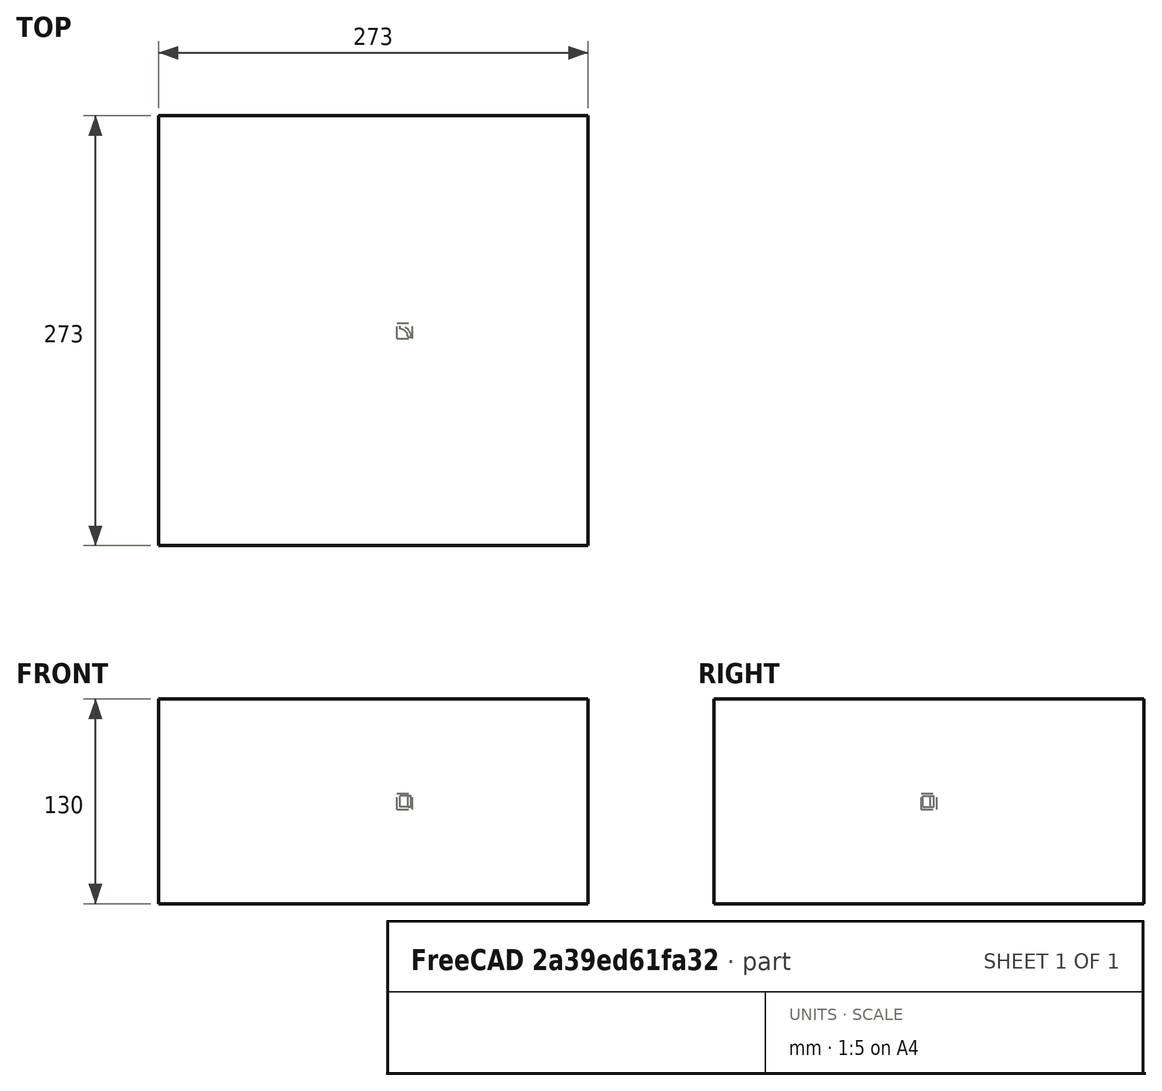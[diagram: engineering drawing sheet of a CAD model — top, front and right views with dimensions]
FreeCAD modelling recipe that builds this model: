
FCSTD DOCUMENT  (FreeCAD 0.20RUnknown)
Label: array-of-array-a
License: All rights reserved
LicenseURL: http://en.wikipedia.org/wiki/All_rights_reserved
objects: App::DocumentObjectGroupPython×1251, Part::FeaturePython×5, App::Part×4
note: 3 computed .brp shape members not serialized (recipe doc carries the construction recipe); baked Part::Feature solids carry a one-line shape summary decoded from their .brp

FEATURE [App::DocumentObjectGroupPython] HALFPI  # scripted group (container) (typed FeaturePython)
  name = HALFPI
  value = pi/2.
FEATURE [App::DocumentObjectGroupPython] PI  # scripted group (container) (typed FeaturePython)
  name = PI
  value = 1.*pi
FEATURE [App::DocumentObjectGroupPython] TWOPI  # scripted group (container) (typed FeaturePython)
  name = TWOPI
  value = 2.*pi
FEATURE [App::DocumentObjectGroupPython] Constants  # scripted group (container) (typed FeaturePython)
  Group = -> [HALFPI,PI,TWOPI]
FEATURE [App::DocumentObjectGroupPython] Variables  # scripted group (container) (typed FeaturePython)
FEATURE [App::DocumentObjectGroupPython] Quantities  # scripted group (container) (typed FeaturePython)
FEATURE [App::DocumentObjectGroupPython] Isotopes  # scripted group (container) (typed FeaturePython)
FEATURE [App::DocumentObjectGroupPython] Elements  # scripted group (container) (typed FeaturePython)
FEATURE [App::DocumentObjectGroupPython] Matrix  # scripted group (container) (typed FeaturePython)
FEATURE [App::DocumentObjectGroupPython] Surfaces  # scripted group (container) (typed FeaturePython)
FEATURE [App::DocumentObjectGroupPython] Opticals  # scripted group (container) (typed FeaturePython)
  Group = -> [Matrix,Surfaces]
FEATURE [App::DocumentObjectGroupPython] G4Isotopes  # scripted group (container) (typed FeaturePython)
FEATURE [App::DocumentObjectGroupPython] H_element  # scripted group (container) (typed FeaturePython)
  Z = 1
  atom_value = 1.008
  formula = H
  name = H_element
FEATURE [App::DocumentObjectGroupPython] He_element  # scripted group (container) (typed FeaturePython)
  Z = 2
  atom_value = 4.0026
  formula = He
  name = He_element
FEATURE [App::DocumentObjectGroupPython] Li_element  # scripted group (container) (typed FeaturePython)
  Z = 3
  atom_value = 6.94
  formula = Li
  name = Li_element
FEATURE [App::DocumentObjectGroupPython] Be_element  # scripted group (container) (typed FeaturePython)
  Z = 4
  atom_value = 9.01218
  formula = Be
  name = Be_element
FEATURE [App::DocumentObjectGroupPython] B_element  # scripted group (container) (typed FeaturePython)
  Z = 5
  atom_value = 10.81
  formula = B
  name = B_element
FEATURE [App::DocumentObjectGroupPython] C_element  # scripted group (container) (typed FeaturePython)
  Z = 6
  atom_value = 12.011
  formula = C
  name = C_element
FEATURE [App::DocumentObjectGroupPython] N_element  # scripted group (container) (typed FeaturePython)
  Z = 7
  atom_value = 14.007
  formula = N
  name = N_element
FEATURE [App::DocumentObjectGroupPython] O_element  # scripted group (container) (typed FeaturePython)
  Z = 8
  atom_value = 15.999
  formula = O
  name = O_element
FEATURE [App::DocumentObjectGroupPython] F_element  # scripted group (container) (typed FeaturePython)
  Z = 9
  atom_value = 18.9984
  formula = F
  name = F_element
FEATURE [App::DocumentObjectGroupPython] Ne_element  # scripted group (container) (typed FeaturePython)
  Z = 10
  atom_value = 20.1797
  formula = Ne
  name = Ne_element
FEATURE [App::DocumentObjectGroupPython] Na_element  # scripted group (container) (typed FeaturePython)
  Z = 11
  atom_value = 22.9898
  formula = Na
  name = Na_element
FEATURE [App::DocumentObjectGroupPython] Mg_element  # scripted group (container) (typed FeaturePython)
  Z = 12
  atom_value = 24.305
  formula = Mg
  name = Mg_element
FEATURE [App::DocumentObjectGroupPython] Al_element  # scripted group (container) (typed FeaturePython)
  Z = 13
  atom_value = 26.9815
  formula = Al
  name = Al_element
FEATURE [App::DocumentObjectGroupPython] Si_element  # scripted group (container) (typed FeaturePython)
  Z = 14
  atom_value = 28.085
  formula = Si
  name = Si_element
FEATURE [App::DocumentObjectGroupPython] P_element  # scripted group (container) (typed FeaturePython)
  Z = 15
  atom_value = 30.9738
  formula = P
  name = P_element
FEATURE [App::DocumentObjectGroupPython] S_element  # scripted group (container) (typed FeaturePython)
  Z = 16
  atom_value = 32.06
  formula = S
  name = S_element
FEATURE [App::DocumentObjectGroupPython] Cl_element  # scripted group (container) (typed FeaturePython)
  Z = 17
  atom_value = 35.45
  formula = Cl
  name = Cl_element
FEATURE [App::DocumentObjectGroupPython] Ar_element  # scripted group (container) (typed FeaturePython)
  Z = 18
  atom_value = 39.95
  formula = Ar
  name = Ar_element
FEATURE [App::DocumentObjectGroupPython] K_element  # scripted group (container) (typed FeaturePython)
  Z = 19
  atom_value = 39.0983
  formula = K
  name = K_element
FEATURE [App::DocumentObjectGroupPython] Ca_element  # scripted group (container) (typed FeaturePython)
  Z = 20
  atom_value = 40.078
  formula = Ca
  name = Ca_element
FEATURE [App::DocumentObjectGroupPython] Sc_element  # scripted group (container) (typed FeaturePython)
  Z = 21
  atom_value = 44.9559
  formula = Sc
  name = Sc_element
FEATURE [App::DocumentObjectGroupPython] Ti_element  # scripted group (container) (typed FeaturePython)
  Z = 22
  atom_value = 47.867
  formula = Ti
  name = Ti_element
FEATURE [App::DocumentObjectGroupPython] V_element  # scripted group (container) (typed FeaturePython)
  Z = 23
  atom_value = 50.9415
  formula = V
  name = V_element
FEATURE [App::DocumentObjectGroupPython] Cr_element  # scripted group (container) (typed FeaturePython)
  Z = 24
  atom_value = 51.9961
  formula = Cr
  name = Cr_element
FEATURE [App::DocumentObjectGroupPython] Mn_element  # scripted group (container) (typed FeaturePython)
  Z = 25
  atom_value = 54.938
  formula = Mn
  name = Mn_element
FEATURE [App::DocumentObjectGroupPython] Fe_element  # scripted group (container) (typed FeaturePython)
  Z = 26
  atom_value = 55.845
  formula = Fe
  name = Fe_element
FEATURE [App::DocumentObjectGroupPython] Co_element  # scripted group (container) (typed FeaturePython)
  Z = 27
  atom_value = 58.9332
  formula = Co
  name = Co_element
FEATURE [App::DocumentObjectGroupPython] Ni_element  # scripted group (container) (typed FeaturePython)
  Z = 28
  atom_value = 58.6934
  formula = Ni
  name = Ni_element
FEATURE [App::DocumentObjectGroupPython] Cu_element  # scripted group (container) (typed FeaturePython)
  Z = 29
  atom_value = 63.546
  formula = Cu
  name = Cu_element
FEATURE [App::DocumentObjectGroupPython] Zn_element  # scripted group (container) (typed FeaturePython)
  Z = 30
  atom_value = 65.38
  formula = Zn
  name = Zn_element
FEATURE [App::DocumentObjectGroupPython] Ga_element  # scripted group (container) (typed FeaturePython)
  Z = 31
  atom_value = 69.723
  formula = Ga
  name = Ga_element
FEATURE [App::DocumentObjectGroupPython] Ge_element  # scripted group (container) (typed FeaturePython)
  Z = 32
  atom_value = 72.63
  formula = Ge
  name = Ge_element
FEATURE [App::DocumentObjectGroupPython] As_element  # scripted group (container) (typed FeaturePython)
  Z = 33
  atom_value = 74.9216
  formula = As
  name = As_element
FEATURE [App::DocumentObjectGroupPython] Se_element  # scripted group (container) (typed FeaturePython)
  Z = 34
  atom_value = 78.971
  formula = Se
  name = Se_element
FEATURE [App::DocumentObjectGroupPython] Br_element  # scripted group (container) (typed FeaturePython)
  Z = 35
  atom_value = 79.904
  formula = Br
  name = Br_element
FEATURE [App::DocumentObjectGroupPython] Kr_element  # scripted group (container) (typed FeaturePython)
  Z = 36
  atom_value = 83.798
  formula = Kr
  name = Kr_element
FEATURE [App::DocumentObjectGroupPython] Rb_element  # scripted group (container) (typed FeaturePython)
  Z = 37
  atom_value = 85.4678
  formula = Rb
  name = Rb_element
FEATURE [App::DocumentObjectGroupPython] Sr_element  # scripted group (container) (typed FeaturePython)
  Z = 38
  atom_value = 87.62
  formula = Sr
  name = Sr_element
FEATURE [App::DocumentObjectGroupPython] Y_element  # scripted group (container) (typed FeaturePython)
  Z = 39
  atom_value = 88.9058
  formula = Y
  name = Y_element
FEATURE [App::DocumentObjectGroupPython] Zr_element  # scripted group (container) (typed FeaturePython)
  Z = 40
  atom_value = 91.224
  formula = Zr
  name = Zr_element
FEATURE [App::DocumentObjectGroupPython] Nb_element  # scripted group (container) (typed FeaturePython)
  Z = 41
  atom_value = 92.9064
  formula = Nb
  name = Nb_element
FEATURE [App::DocumentObjectGroupPython] Mo_element  # scripted group (container) (typed FeaturePython)
  Z = 42
  atom_value = 95.95
  formula = Mo
  name = Mo_element
FEATURE [App::DocumentObjectGroupPython] Tc_element  # scripted group (container) (typed FeaturePython)
  Z = 43
  atom_value = 97
  formula = Tc
  name = Tc_element
FEATURE [App::DocumentObjectGroupPython] Ru_element  # scripted group (container) (typed FeaturePython)
  Z = 44
  atom_value = 101.07
  formula = Ru
  name = Ru_element
FEATURE [App::DocumentObjectGroupPython] Rh_element  # scripted group (container) (typed FeaturePython)
  Z = 45
  atom_value = 102.905
  formula = Rh
  name = Rh_element
FEATURE [App::DocumentObjectGroupPython] Pd_element  # scripted group (container) (typed FeaturePython)
  Z = 46
  atom_value = 106.42
  formula = Pd
  name = Pd_element
FEATURE [App::DocumentObjectGroupPython] Ag_element  # scripted group (container) (typed FeaturePython)
  Z = 47
  atom_value = 107.868
  formula = Ag
  name = Ag_element
FEATURE [App::DocumentObjectGroupPython] Cd_element  # scripted group (container) (typed FeaturePython)
  Z = 48
  atom_value = 112.414
  formula = Cd
  name = Cd_element
FEATURE [App::DocumentObjectGroupPython] In_element  # scripted group (container) (typed FeaturePython)
  Z = 49
  atom_value = 114.818
  formula = In
  name = In_element
FEATURE [App::DocumentObjectGroupPython] Sn_element  # scripted group (container) (typed FeaturePython)
  Z = 50
  atom_value = 118.71
  formula = Sn
  name = Sn_element
FEATURE [App::DocumentObjectGroupPython] Sb_element  # scripted group (container) (typed FeaturePython)
  Z = 51
  atom_value = 121.76
  formula = Sb
  name = Sb_element
FEATURE [App::DocumentObjectGroupPython] Te_element  # scripted group (container) (typed FeaturePython)
  Z = 52
  atom_value = 127.6
  formula = Te
  name = Te_element
FEATURE [App::DocumentObjectGroupPython] I_element  # scripted group (container) (typed FeaturePython)
  Z = 53
  atom_value = 126.904
  formula = I
  name = I_element
FEATURE [App::DocumentObjectGroupPython] Xe_element  # scripted group (container) (typed FeaturePython)
  Z = 54
  atom_value = 131.293
  formula = Xe
  name = Xe_element
FEATURE [App::DocumentObjectGroupPython] Cs_element  # scripted group (container) (typed FeaturePython)
  Z = 55
  atom_value = 132.905
  formula = Cs
  name = Cs_element
FEATURE [App::DocumentObjectGroupPython] Ba_element  # scripted group (container) (typed FeaturePython)
  Z = 56
  atom_value = 137.327
  formula = Ba
  name = Ba_element
FEATURE [App::DocumentObjectGroupPython] La_element  # scripted group (container) (typed FeaturePython)
  Z = 57
  atom_value = 138.905
  formula = La
  name = La_element
FEATURE [App::DocumentObjectGroupPython] Ce_element  # scripted group (container) (typed FeaturePython)
  Z = 58
  atom_value = 140.116
  formula = Ce
  name = Ce_element
FEATURE [App::DocumentObjectGroupPython] Pr_element  # scripted group (container) (typed FeaturePython)
  Z = 59
  atom_value = 140.908
  formula = Pr
  name = Pr_element
FEATURE [App::DocumentObjectGroupPython] Nd_element  # scripted group (container) (typed FeaturePython)
  Z = 60
  atom_value = 144.242
  formula = Nd
  name = Nd_element
FEATURE [App::DocumentObjectGroupPython] Pm_element  # scripted group (container) (typed FeaturePython)
  Z = 61
  atom_value = 145
  formula = Pm
  name = Pm_element
FEATURE [App::DocumentObjectGroupPython] Sm_element  # scripted group (container) (typed FeaturePython)
  Z = 62
  atom_value = 150.36
  formula = Sm
  name = Sm_element
FEATURE [App::DocumentObjectGroupPython] Eu_element  # scripted group (container) (typed FeaturePython)
  Z = 63
  atom_value = 151.964
  formula = Eu
  name = Eu_element
FEATURE [App::DocumentObjectGroupPython] Gd_element  # scripted group (container) (typed FeaturePython)
  Z = 64
  atom_value = 157.25
  formula = Gd
  name = Gd_element
FEATURE [App::DocumentObjectGroupPython] Tb_element  # scripted group (container) (typed FeaturePython)
  Z = 65
  atom_value = 158.925
  formula = Tb
  name = Tb_element
FEATURE [App::DocumentObjectGroupPython] Dy_element  # scripted group (container) (typed FeaturePython)
  Z = 66
  atom_value = 162.5
  formula = Dy
  name = Dy_element
FEATURE [App::DocumentObjectGroupPython] Ho_element  # scripted group (container) (typed FeaturePython)
  Z = 67
  atom_value = 164.93
  formula = Ho
  name = Ho_element
FEATURE [App::DocumentObjectGroupPython] Er_element  # scripted group (container) (typed FeaturePython)
  Z = 68
  atom_value = 167.259
  formula = Er
  name = Er_element
FEATURE [App::DocumentObjectGroupPython] Tm_element  # scripted group (container) (typed FeaturePython)
  Z = 69
  atom_value = 168.934
  formula = Tm
  name = Tm_element
FEATURE [App::DocumentObjectGroupPython] Yb_element  # scripted group (container) (typed FeaturePython)
  Z = 70
  atom_value = 173.045
  formula = Yb
  name = Yb_element
FEATURE [App::DocumentObjectGroupPython] Lu_element  # scripted group (container) (typed FeaturePython)
  Z = 71
  atom_value = 174.967
  formula = Lu
  name = Lu_element
FEATURE [App::DocumentObjectGroupPython] Hf_element  # scripted group (container) (typed FeaturePython)
  Z = 72
  atom_value = 178.49
  formula = Hf
  name = Hf_element
FEATURE [App::DocumentObjectGroupPython] Ta_element  # scripted group (container) (typed FeaturePython)
  Z = 73
  atom_value = 180.948
  formula = Ta
  name = Ta_element
FEATURE [App::DocumentObjectGroupPython] W_element  # scripted group (container) (typed FeaturePython)
  Z = 74
  atom_value = 183.84
  formula = W
  name = W_element
FEATURE [App::DocumentObjectGroupPython] Re_element  # scripted group (container) (typed FeaturePython)
  Z = 75
  atom_value = 186.207
  formula = Re
  name = Re_element
FEATURE [App::DocumentObjectGroupPython] Os_element  # scripted group (container) (typed FeaturePython)
  Z = 76
  atom_value = 190.23
  formula = Os
  name = Os_element
FEATURE [App::DocumentObjectGroupPython] Ir_element  # scripted group (container) (typed FeaturePython)
  Z = 77
  atom_value = 192.217
  formula = Ir
  name = Ir_element
FEATURE [App::DocumentObjectGroupPython] Pt_element  # scripted group (container) (typed FeaturePython)
  Z = 78
  atom_value = 195.084
  formula = Pt
  name = Pt_element
FEATURE [App::DocumentObjectGroupPython] Au_element  # scripted group (container) (typed FeaturePython)
  Z = 79
  atom_value = 196.967
  formula = Au
  name = Au_element
FEATURE [App::DocumentObjectGroupPython] Hg_element  # scripted group (container) (typed FeaturePython)
  Z = 80
  atom_value = 200.592
  formula = Hg
  name = Hg_element
FEATURE [App::DocumentObjectGroupPython] Tl_element  # scripted group (container) (typed FeaturePython)
  Z = 81
  atom_value = 204.38
  formula = Tl
  name = Tl_element
FEATURE [App::DocumentObjectGroupPython] Pb_element  # scripted group (container) (typed FeaturePython)
  Z = 82
  atom_value = 207.2
  formula = Pb
  name = Pb_element
FEATURE [App::DocumentObjectGroupPython] Bi_element  # scripted group (container) (typed FeaturePython)
  Z = 83
  atom_value = 208.98
  formula = Bi
  name = Bi_element
FEATURE [App::DocumentObjectGroupPython] Po_element  # scripted group (container) (typed FeaturePython)
  Z = 84
  atom_value = 209
  formula = Po
  name = Po_element
FEATURE [App::DocumentObjectGroupPython] At_element  # scripted group (container) (typed FeaturePython)
  Z = 85
  atom_value = 210
  formula = At
  name = At_element
FEATURE [App::DocumentObjectGroupPython] Rn_element  # scripted group (container) (typed FeaturePython)
  Z = 86
  atom_value = 222
  formula = Rn
  name = Rn_element
FEATURE [App::DocumentObjectGroupPython] Fr_element  # scripted group (container) (typed FeaturePython)
  Z = 87
  atom_value = 223
  formula = Fr
  name = Fr_element
FEATURE [App::DocumentObjectGroupPython] Ra_element  # scripted group (container) (typed FeaturePython)
  Z = 88
  atom_value = 226
  formula = Ra
  name = Ra_element
FEATURE [App::DocumentObjectGroupPython] Ac_element  # scripted group (container) (typed FeaturePython)
  Z = 89
  atom_value = 227
  formula = Ac
  name = Ac_element
FEATURE [App::DocumentObjectGroupPython] Th_element  # scripted group (container) (typed FeaturePython)
  Z = 90
  atom_value = 232.038
  formula = Th
  name = Th_element
FEATURE [App::DocumentObjectGroupPython] Pa_element  # scripted group (container) (typed FeaturePython)
  Z = 91
  atom_value = 231.036
  formula = Pa
  name = Pa_element
FEATURE [App::DocumentObjectGroupPython] U_element  # scripted group (container) (typed FeaturePython)
  Z = 92
  atom_value = 238.029
  formula = U
  name = U_element
FEATURE [App::DocumentObjectGroupPython] Np_element  # scripted group (container) (typed FeaturePython)
  Z = 93
  atom_value = 237
  formula = Np
  name = Np_element
FEATURE [App::DocumentObjectGroupPython] Pu_element  # scripted group (container) (typed FeaturePython)
  Z = 94
  atom_value = 244
  formula = Pu
  name = Pu_element
FEATURE [App::DocumentObjectGroupPython] Am_element  # scripted group (container) (typed FeaturePython)
  Z = 95
  atom_value = 243
  formula = Am
  name = Am_element
FEATURE [App::DocumentObjectGroupPython] Cm_element  # scripted group (container) (typed FeaturePython)
  Z = 96
  atom_value = 247
  formula = Cm
  name = Cm_element
FEATURE [App::DocumentObjectGroupPython] Bk_element  # scripted group (container) (typed FeaturePython)
  Z = 97
  atom_value = 247
  formula = Bk
  name = Bk_element
FEATURE [App::DocumentObjectGroupPython] Cf_element  # scripted group (container) (typed FeaturePython)
  Z = 98
  atom_value = 251
  formula = Cf
  name = Cf_element
FEATURE [App::DocumentObjectGroupPython] G4Elements  # scripted group (container) (typed FeaturePython)
  Group = -> [H_element,He_element,Li_element,Be_element,B_element,C_element,N_element,O_element,F_element,Ne_element,Na_element,Mg_element,Al_element,Si_element,P_element,S_element,Cl_element,Ar_element,K_element,Ca_element,Sc_element,Ti_element,V_element,Cr_element,Mn_element,Fe_element,Co_element,Ni_element,Cu_element,Zn_element,Ga_element,Ge_element,As_element,Se_element,Br_element,Kr_element,Rb_element,+61 more]
FEATURE [App::DocumentObjectGroupPython] H_element001  label="H_element : 0.101"  # scripted group (container) (typed FeaturePython)
  n = 0.101327
FEATURE [App::DocumentObjectGroupPython] C_element001  label="C_element : 0.775"  # scripted group (container) (typed FeaturePython)
  n = 0.7755
FEATURE [App::DocumentObjectGroupPython] N_element001  label="N_element : 0.035"  # scripted group (container) (typed FeaturePython)
  n = 0.035057
FEATURE [App::DocumentObjectGroupPython] O_element001  label="O_element : 0.052"  # scripted group (container) (typed FeaturePython)
  n = 0.0523159
FEATURE [App::DocumentObjectGroupPython] F_element001  label="F_element : 0.017"  # scripted group (container) (typed FeaturePython)
  n = 0.017422
FEATURE [App::DocumentObjectGroupPython] Ca_element001  label="Ca_element : 0.018"  # scripted group (container) (typed FeaturePython)
  n = 0.018378
FEATURE [App::DocumentObjectGroupPython] G4_A_150_TISSUE  label="G4_A-150_TISSUE"  # scripted group (container) (typed FeaturePython)
  Dunit = g/cm3
  Dvalue = 1.127
  Group = -> [H_element001,C_element001,N_element001,O_element001,F_element001,Ca_element001]
  conduct = 2
  density = 1
  expand = 3
  formula = G4_A-150_TISSUE
  name = G4_A-150_TISSUE
  specific = 4
FEATURE [App::DocumentObjectGroupPython] C_element002  label="C_element : 3"  # scripted group (container) (typed FeaturePython)
  n = 3
  ref = C_element
FEATURE [App::DocumentObjectGroupPython] H_element002  label="H_element : 6"  # scripted group (container) (typed FeaturePython)
  n = 6
  ref = H_element
FEATURE [App::DocumentObjectGroupPython] O_element002  label="O_element : 1"  # scripted group (container) (typed FeaturePython)
  n = 1
  ref = O_element
FEATURE [App::DocumentObjectGroupPython] G4_ACETONE  # scripted group (container) (typed FeaturePython)
  Dunit = g/cm3
  Dvalue = 0.7899
  Group = -> [C_element002,H_element002,O_element002]
  conduct = 2
  density = 1
  expand = 3
  formula = G4_ACETONE
  name = G4_ACETONE
  specific = 4
FEATURE [App::DocumentObjectGroupPython] C_element003  label="C_element : 2"  # scripted group (container) (typed FeaturePython)
  n = 2
  ref = C_element
FEATURE [App::DocumentObjectGroupPython] H_element003  label="H_element : 2"  # scripted group (container) (typed FeaturePython)
  n = 2
  ref = H_element
FEATURE [App::DocumentObjectGroupPython] G4_ACETYLENE  # scripted group (container) (typed FeaturePython)
  Dunit = g/cm3
  Dvalue = 0.0010967
  Group = -> [C_element003,H_element003]
  conduct = 2
  density = 1
  expand = 3
  formula = G4_ACETYLENE
  name = G4_ACETYLENE
  specific = 4
FEATURE [App::DocumentObjectGroupPython] C_element004  label="C_element : 5"  # scripted group (container) (typed FeaturePython)
  n = 5
  ref = C_element
FEATURE [App::DocumentObjectGroupPython] H_element004  label="H_element : 5"  # scripted group (container) (typed FeaturePython)
  n = 5
  ref = H_element
FEATURE [App::DocumentObjectGroupPython] N_element002  label="N_element : 5"  # scripted group (container) (typed FeaturePython)
  n = 5
  ref = N_element
FEATURE [App::DocumentObjectGroupPython] G4_ADENINE  # scripted group (container) (typed FeaturePython)
  Dunit = g/cm3
  Dvalue = 1.6
  Group = -> [C_element004,H_element004,N_element002]
  conduct = 2
  density = 1
  expand = 3
  formula = G4_ADENINE
  name = G4_ADENINE
  specific = 4
FEATURE [App::DocumentObjectGroupPython] H_element005  label="H_element : 0.114"  # scripted group (container) (typed FeaturePython)
  n = 0.114
FEATURE [App::DocumentObjectGroupPython] C_element005  label="C_element : 0.598"  # scripted group (container) (typed FeaturePython)
  n = 0.598
FEATURE [App::DocumentObjectGroupPython] N_element003  label="N_element : 0.007"  # scripted group (container) (typed FeaturePython)
  n = 0.007
FEATURE [App::DocumentObjectGroupPython] O_element003  label="O_element : 0.278"  # scripted group (container) (typed FeaturePython)
  n = 0.278
FEATURE [App::DocumentObjectGroupPython] Na_element001  label="Na_element : 0.001"  # scripted group (container) (typed FeaturePython)
  n = 0.001
FEATURE [App::DocumentObjectGroupPython] S_element001  label="S_element : 0.001"  # scripted group (container) (typed FeaturePython)
  n = 0.001
FEATURE [App::DocumentObjectGroupPython] Cl_element001  label="Cl_element : 0.001"  # scripted group (container) (typed FeaturePython)
  n = 0.001
FEATURE [App::DocumentObjectGroupPython] G4_ADIPOSE_TISSUE_ICRP  # scripted group (container) (typed FeaturePython)
  Dunit = g/cm3
  Dvalue = 0.95
  Group = -> [H_element005,C_element005,N_element003,O_element003,Na_element001,S_element001,Cl_element001]
  conduct = 2
  density = 1
  expand = 3
  formula = G4_ADIPOSE_TISSUE_ICRP
  name = G4_ADIPOSE_TISSUE_ICRP
  specific = 4
FEATURE [App::DocumentObjectGroupPython] C_element006  label="C_element : 0.000"  # scripted group (container) (typed FeaturePython)
  n = 0.000124
FEATURE [App::DocumentObjectGroupPython] N_element004  label="N_element : 0.755"  # scripted group (container) (typed FeaturePython)
  n = 0.755268
FEATURE [App::DocumentObjectGroupPython] O_element004  label="O_element : 0.232"  # scripted group (container) (typed FeaturePython)
  n = 0.231781
FEATURE [App::DocumentObjectGroupPython] Ar_element001  label="Ar_element : 0.013"  # scripted group (container) (typed FeaturePython)
  n = 0.012827
FEATURE [App::DocumentObjectGroupPython] G4_AIR  # scripted group (container) (typed FeaturePython)
  Dunit = g/cm3
  Dvalue = 0.00120479
  Group = -> [C_element006,N_element004,O_element004,Ar_element001]
  conduct = 2
  density = 1
  expand = 3
  formula = G4_AIR
  name = G4_AIR
  specific = 4
FEATURE [App::DocumentObjectGroupPython] C_element007  label="C_element : 006"  # scripted group (container) (typed FeaturePython)
  n = 3
  ref = C_element
FEATURE [App::DocumentObjectGroupPython] H_element006  label="H_element : 7"  # scripted group (container) (typed FeaturePython)
  n = 7
  ref = H_element
FEATURE [App::DocumentObjectGroupPython] N_element005  label="N_element : 1"  # scripted group (container) (typed FeaturePython)
  n = 1
  ref = N_element
FEATURE [App::DocumentObjectGroupPython] O_element005  label="O_element : 2"  # scripted group (container) (typed FeaturePython)
  n = 2
  ref = O_element
FEATURE [App::DocumentObjectGroupPython] G4_ALANINE  # scripted group (container) (typed FeaturePython)
  Dunit = g/cm3
  Dvalue = 1.42
  Group = -> [C_element007,H_element006,N_element005,O_element005]
  conduct = 2
  density = 1
  expand = 3
  formula = G4_ALANINE
  name = G4_ALANINE
  specific = 4
FEATURE [App::DocumentObjectGroupPython] Al_element001  label="Al_element : 2"  # scripted group (container) (typed FeaturePython)
  n = 2
  ref = Al_element
FEATURE [App::DocumentObjectGroupPython] O_element006  label="O_element : 3"  # scripted group (container) (typed FeaturePython)
  n = 3
  ref = O_element
FEATURE [App::DocumentObjectGroupPython] G4_ALUMINUM_OXIDE  # scripted group (container) (typed FeaturePython)
  Dunit = g/cm3
  Dvalue = 3.97
  Group = -> [Al_element001,O_element006]
  conduct = 2
  density = 1
  expand = 3
  formula = G4_ALUMINUM_OXIDE
  name = G4_ALUMINUM_OXIDE
  specific = 4
FEATURE [App::DocumentObjectGroupPython] H_element007  label="H_element : 0.106"  # scripted group (container) (typed FeaturePython)
  n = 0.10593
FEATURE [App::DocumentObjectGroupPython] C_element008  label="C_element : 0.789"  # scripted group (container) (typed FeaturePython)
  n = 0.788974
FEATURE [App::DocumentObjectGroupPython] O_element007  label="O_element : 0.105"  # scripted group (container) (typed FeaturePython)
  n = 0.105096
FEATURE [App::DocumentObjectGroupPython] G4_AMBER  # scripted group (container) (typed FeaturePython)
  Dunit = g/cm3
  Dvalue = 1.1
  Group = -> [H_element007,C_element008,O_element007]
  conduct = 2
  density = 1
  expand = 3
  formula = G4_AMBER
  name = G4_AMBER
  specific = 4
FEATURE [App::DocumentObjectGroupPython] N_element006  label="N_element : 006"  # scripted group (container) (typed FeaturePython)
  n = 1
  ref = N_element
FEATURE [App::DocumentObjectGroupPython] H_element008  label="H_element : 3"  # scripted group (container) (typed FeaturePython)
  n = 3
  ref = H_element
FEATURE [App::DocumentObjectGroupPython] G4_AMMONIA  # scripted group (container) (typed FeaturePython)
  Dunit = g/cm3
  Dvalue = 0.000826019
  Group = -> [N_element006,H_element008]
  conduct = 2
  density = 1
  expand = 3
  formula = G4_AMMONIA
  name = G4_AMMONIA
  specific = 4
FEATURE [App::DocumentObjectGroupPython] C_element009  label="C_element : 6"  # scripted group (container) (typed FeaturePython)
  n = 6
  ref = C_element
FEATURE [App::DocumentObjectGroupPython] H_element009  label="H_element : 008"  # scripted group (container) (typed FeaturePython)
  n = 7
  ref = H_element
FEATURE [App::DocumentObjectGroupPython] N_element007  label="N_element : 007"  # scripted group (container) (typed FeaturePython)
  n = 1
  ref = N_element
FEATURE [App::DocumentObjectGroupPython] G4_ANILINE  # scripted group (container) (typed FeaturePython)
  Dunit = g/cm3
  Dvalue = 1.0235
  Group = -> [C_element009,H_element009,N_element007]
  conduct = 2
  density = 1
  expand = 3
  formula = G4_ANILINE
  name = G4_ANILINE
  specific = 4
FEATURE [App::DocumentObjectGroupPython] C_element010  label="C_element : 14"  # scripted group (container) (typed FeaturePython)
  n = 14
  ref = C_element
FEATURE [App::DocumentObjectGroupPython] H_element010  label="H_element : 10"  # scripted group (container) (typed FeaturePython)
  n = 10
  ref = H_element
FEATURE [App::DocumentObjectGroupPython] G4_ANTHRACENE  # scripted group (container) (typed FeaturePython)
  Dunit = g/cm3
  Dvalue = 1.283
  Group = -> [C_element010,H_element010]
  conduct = 2
  density = 1
  expand = 3
  formula = G4_ANTHRACENE
  name = G4_ANTHRACENE
  specific = 4
FEATURE [App::DocumentObjectGroupPython] H_element011  label="H_element : 0.065"  # scripted group (container) (typed FeaturePython)
  n = 0.0654709
FEATURE [App::DocumentObjectGroupPython] C_element011  label="C_element : 0.537"  # scripted group (container) (typed FeaturePython)
  n = 0.536944
FEATURE [App::DocumentObjectGroupPython] N_element008  label="N_element : 0.021"  # scripted group (container) (typed FeaturePython)
  n = 0.0215
FEATURE [App::DocumentObjectGroupPython] O_element008  label="O_element : 0.032"  # scripted group (container) (typed FeaturePython)
  n = 0.032085
FEATURE [App::DocumentObjectGroupPython] F_element002  label="F_element : 0.167"  # scripted group (container) (typed FeaturePython)
  n = 0.167411
FEATURE [App::DocumentObjectGroupPython] Ca_element002  label="Ca_element : 0.177"  # scripted group (container) (typed FeaturePython)
  n = 0.176589
FEATURE [App::DocumentObjectGroupPython] G4_B_100_BONE  label="G4_B-100_BONE"  # scripted group (container) (typed FeaturePython)
  Dunit = g/cm3
  Dvalue = 1.45
  Group = -> [H_element011,C_element011,N_element008,O_element008,F_element002,Ca_element002]
  conduct = 2
  density = 1
  expand = 3
  formula = G4_B-100_BONE
  name = G4_B-100_BONE
  specific = 4
FEATURE [App::DocumentObjectGroupPython] H_element012  label="H_element : 0.057"  # scripted group (container) (typed FeaturePython)
  n = 0.057441
FEATURE [App::DocumentObjectGroupPython] C_element012  label="C_element : 0.790"  # scripted group (container) (typed FeaturePython)
  n = 0.774591
FEATURE [App::DocumentObjectGroupPython] O_element009  label="O_element : 0.168"  # scripted group (container) (typed FeaturePython)
  n = 0.167968
FEATURE [App::DocumentObjectGroupPython] G4_BAKELITE  # scripted group (container) (typed FeaturePython)
  Dunit = g/cm3
  Dvalue = 1.25
  Group = -> [H_element012,C_element012,O_element009]
  conduct = 2
  density = 1
  expand = 3
  formula = G4_BAKELITE
  name = G4_BAKELITE
  specific = 4
FEATURE [App::DocumentObjectGroupPython] Ba_element001  label="Ba_element : 1"  # scripted group (container) (typed FeaturePython)
  n = 1
  ref = Ba_element
FEATURE [App::DocumentObjectGroupPython] F_element003  label="F_element : 2"  # scripted group (container) (typed FeaturePython)
  n = 2
  ref = F_element
FEATURE [App::DocumentObjectGroupPython] G4_BARIUM_FLUORIDE  # scripted group (container) (typed FeaturePython)
  Dunit = g/cm3
  Dvalue = 4.89
  Group = -> [Ba_element001,F_element003]
  conduct = 2
  density = 1
  expand = 3
  formula = G4_BARIUM_FLUORIDE
  name = G4_BARIUM_FLUORIDE
  specific = 4
FEATURE [App::DocumentObjectGroupPython] Ba_element002  label="Ba_element : 002"  # scripted group (container) (typed FeaturePython)
  n = 1
  ref = Ba_element
FEATURE [App::DocumentObjectGroupPython] S_element002  label="S_element : 1"  # scripted group (container) (typed FeaturePython)
  n = 1
  ref = S_element
FEATURE [App::DocumentObjectGroupPython] O_element010  label="O_element : 4"  # scripted group (container) (typed FeaturePython)
  n = 4
  ref = O_element
FEATURE [App::DocumentObjectGroupPython] G4_BARIUM_SULFATE  # scripted group (container) (typed FeaturePython)
  Dunit = g/cm3
  Dvalue = 4.5
  Group = -> [Ba_element002,S_element002,O_element010]
  conduct = 2
  density = 1
  expand = 3
  formula = G4_BARIUM_SULFATE
  name = G4_BARIUM_SULFATE
  specific = 4
FEATURE [App::DocumentObjectGroupPython] C_element013  label="C_element : 007"  # scripted group (container) (typed FeaturePython)
  n = 6
  ref = C_element
FEATURE [App::DocumentObjectGroupPython] H_element013  label="H_element : 009"  # scripted group (container) (typed FeaturePython)
  n = 6
  ref = H_element
FEATURE [App::DocumentObjectGroupPython] G4_BENZENE  # scripted group (container) (typed FeaturePython)
  Dunit = g/cm3
  Dvalue = 0.87865
  Group = -> [C_element013,H_element013]
  conduct = 2
  density = 1
  expand = 3
  formula = G4_BENZENE
  name = G4_BENZENE
  specific = 4
FEATURE [App::DocumentObjectGroupPython] Be_element001  label="Be_element : 1"  # scripted group (container) (typed FeaturePython)
  n = 1
  ref = Be_element
FEATURE [App::DocumentObjectGroupPython] O_element011  label="O_element : 005"  # scripted group (container) (typed FeaturePython)
  n = 1
  ref = O_element
FEATURE [App::DocumentObjectGroupPython] G4_BERYLLIUM_OXIDE  # scripted group (container) (typed FeaturePython)
  Dunit = g/cm3
  Dvalue = 3.01
  Group = -> [Be_element001,O_element011]
  conduct = 2
  density = 1
  expand = 3
  formula = G4_BERYLLIUM_OXIDE
  name = G4_BERYLLIUM_OXIDE
  specific = 4
FEATURE [App::DocumentObjectGroupPython] Bi_element001  label="Bi_element : 4"  # scripted group (container) (typed FeaturePython)
  n = 4
  ref = Bi_element
FEATURE [App::DocumentObjectGroupPython] Ge_element001  label="Ge_element : 3"  # scripted group (container) (typed FeaturePython)
  n = 3
  ref = Ge_element
FEATURE [App::DocumentObjectGroupPython] O_element012  label="O_element : 12"  # scripted group (container) (typed FeaturePython)
  n = 12
  ref = O_element
FEATURE [App::DocumentObjectGroupPython] G4_BGO  # scripted group (container) (typed FeaturePython)
  Dunit = g/cm3
  Dvalue = 7.13
  Group = -> [Bi_element001,Ge_element001,O_element012]
  conduct = 2
  density = 1
  expand = 3
  formula = G4_BGO
  name = G4_BGO
  specific = 4
FEATURE [App::DocumentObjectGroupPython] H_element014  label="H_element : 0.102"  # scripted group (container) (typed FeaturePython)
  n = 0.102
FEATURE [App::DocumentObjectGroupPython] C_element014  label="C_element : 0.110"  # scripted group (container) (typed FeaturePython)
  n = 0.11
FEATURE [App::DocumentObjectGroupPython] N_element009  label="N_element : 0.033"  # scripted group (container) (typed FeaturePython)
  n = 0.033
FEATURE [App::DocumentObjectGroupPython] O_element013  label="O_element : 0.745"  # scripted group (container) (typed FeaturePython)
  n = 0.745
FEATURE [App::DocumentObjectGroupPython] Na_element002  label="Na_element : 0.002"  # scripted group (container) (typed FeaturePython)
  n = 0.001
FEATURE [App::DocumentObjectGroupPython] P_element001  label="P_element : 0.001"  # scripted group (container) (typed FeaturePython)
  n = 0.001
FEATURE [App::DocumentObjectGroupPython] S_element003  label="S_element : 0.002"  # scripted group (container) (typed FeaturePython)
  n = 0.002
FEATURE [App::DocumentObjectGroupPython] Cl_element002  label="Cl_element : 0.003"  # scripted group (container) (typed FeaturePython)
  n = 0.003
FEATURE [App::DocumentObjectGroupPython] K_element001  label="K_element : 0.002"  # scripted group (container) (typed FeaturePython)
  n = 0.002
FEATURE [App::DocumentObjectGroupPython] Fe_element001  label="Fe_element : 0.001"  # scripted group (container) (typed FeaturePython)
  n = 0.001
FEATURE [App::DocumentObjectGroupPython] G4_BLOOD_ICRP  # scripted group (container) (typed FeaturePython)
  Dunit = g/cm3
  Dvalue = 1.06
  Group = -> [H_element014,C_element014,N_element009,O_element013,Na_element002,P_element001,S_element003,Cl_element002,K_element001,Fe_element001]
  conduct = 2
  density = 1
  expand = 3
  formula = G4_BLOOD_ICRP
  name = G4_BLOOD_ICRP
  specific = 4
FEATURE [App::DocumentObjectGroupPython] H_element015  label="H_element : 0.064"  # scripted group (container) (typed FeaturePython)
  n = 0.064
FEATURE [App::DocumentObjectGroupPython] C_element015  label="C_element : 0.278"  # scripted group (container) (typed FeaturePython)
  n = 0.278
FEATURE [App::DocumentObjectGroupPython] N_element010  label="N_element : 0.027"  # scripted group (container) (typed FeaturePython)
  n = 0.027
FEATURE [App::DocumentObjectGroupPython] O_element014  label="O_element : 0.410"  # scripted group (container) (typed FeaturePython)
  n = 0.41
FEATURE [App::DocumentObjectGroupPython] Mg_element001  label="Mg_element : 0.002"  # scripted group (container) (typed FeaturePython)
  n = 0.002
FEATURE [App::DocumentObjectGroupPython] P_element002  label="P_element : 0.070"  # scripted group (container) (typed FeaturePython)
  n = 0.07
FEATURE [App::DocumentObjectGroupPython] S_element004  label="S_element : 0.003"  # scripted group (container) (typed FeaturePython)
  n = 0.002
FEATURE [App::DocumentObjectGroupPython] Ca_element003  label="Ca_element : 0.147"  # scripted group (container) (typed FeaturePython)
  n = 0.147
FEATURE [App::DocumentObjectGroupPython] G4_BONE_COMPACT_ICRU  # scripted group (container) (typed FeaturePython)
  Dunit = g/cm3
  Dvalue = 1.85
  Group = -> [H_element015,C_element015,N_element010,O_element014,Mg_element001,P_element002,S_element004,Ca_element003]
  conduct = 2
  density = 1
  expand = 3
  formula = G4_BONE_COMPACT_ICRU
  name = G4_BONE_COMPACT_ICRU
  specific = 4
FEATURE [App::DocumentObjectGroupPython] H_element016  label="H_element : 0.034"  # scripted group (container) (typed FeaturePython)
  n = 0.034
FEATURE [App::DocumentObjectGroupPython] C_element016  label="C_element : 0.155"  # scripted group (container) (typed FeaturePython)
  n = 0.155
FEATURE [App::DocumentObjectGroupPython] N_element011  label="N_element : 0.042"  # scripted group (container) (typed FeaturePython)
  n = 0.042
FEATURE [App::DocumentObjectGroupPython] O_element015  label="O_element : 0.435"  # scripted group (container) (typed FeaturePython)
  n = 0.435
FEATURE [App::DocumentObjectGroupPython] Na_element003  label="Na_element : 0.003"  # scripted group (container) (typed FeaturePython)
  n = 0.001
FEATURE [App::DocumentObjectGroupPython] Mg_element002  label="Mg_element : 0.003"  # scripted group (container) (typed FeaturePython)
  n = 0.002
FEATURE [App::DocumentObjectGroupPython] P_element003  label="P_element : 0.103"  # scripted group (container) (typed FeaturePython)
  n = 0.103
FEATURE [App::DocumentObjectGroupPython] S_element005  label="S_element : 0.004"  # scripted group (container) (typed FeaturePython)
  n = 0.003
FEATURE [App::DocumentObjectGroupPython] Ca_element004  label="Ca_element : 0.225"  # scripted group (container) (typed FeaturePython)
  n = 0.225
FEATURE [App::DocumentObjectGroupPython] G4_BONE_CORTICAL_ICRP  # scripted group (container) (typed FeaturePython)
  Dunit = g/cm3
  Dvalue = 1.92
  Group = -> [H_element016,C_element016,N_element011,O_element015,Na_element003,Mg_element002,P_element003,S_element005,Ca_element004]
  conduct = 2
  density = 1
  expand = 3
  formula = G4_BONE_CORTICAL_ICRP
  name = G4_BONE_CORTICAL_ICRP
  specific = 4
FEATURE [App::DocumentObjectGroupPython] B_element001  label="B_element : 4"  # scripted group (container) (typed FeaturePython)
  n = 4
  ref = B_element
FEATURE [App::DocumentObjectGroupPython] C_element017  label="C_element : 1"  # scripted group (container) (typed FeaturePython)
  n = 1
  ref = C_element
FEATURE [App::DocumentObjectGroupPython] G4_BORON_CARBIDE  # scripted group (container) (typed FeaturePython)
  Dunit = g/cm3
  Dvalue = 2.52
  Group = -> [B_element001,C_element017]
  conduct = 2
  density = 1
  expand = 3
  formula = G4_BORON_CARBIDE
  name = G4_BORON_CARBIDE
  specific = 4
FEATURE [App::DocumentObjectGroupPython] B_element002  label="B_element : 2"  # scripted group (container) (typed FeaturePython)
  n = 2
  ref = B_element
FEATURE [App::DocumentObjectGroupPython] O_element016  label="O_element : 006"  # scripted group (container) (typed FeaturePython)
  n = 3
  ref = O_element
FEATURE [App::DocumentObjectGroupPython] G4_BORON_OXIDE  # scripted group (container) (typed FeaturePython)
  Dunit = g/cm3
  Dvalue = 1.812
  Group = -> [B_element002,O_element016]
  conduct = 2
  density = 1
  expand = 3
  formula = G4_BORON_OXIDE
  name = G4_BORON_OXIDE
  specific = 4
FEATURE [App::DocumentObjectGroupPython] H_element017  label="H_element : 0.107"  # scripted group (container) (typed FeaturePython)
  n = 0.107
FEATURE [App::DocumentObjectGroupPython] C_element018  label="C_element : 0.145"  # scripted group (container) (typed FeaturePython)
  n = 0.145
FEATURE [App::DocumentObjectGroupPython] N_element012  label="N_element : 0.022"  # scripted group (container) (typed FeaturePython)
  n = 0.022
FEATURE [App::DocumentObjectGroupPython] O_element017  label="O_element : 0.712"  # scripted group (container) (typed FeaturePython)
  n = 0.712
FEATURE [App::DocumentObjectGroupPython] Na_element004  label="Na_element : 0.004"  # scripted group (container) (typed FeaturePython)
  n = 0.002
FEATURE [App::DocumentObjectGroupPython] P_element004  label="P_element : 0.004"  # scripted group (container) (typed FeaturePython)
  n = 0.004
FEATURE [App::DocumentObjectGroupPython] S_element006  label="S_element : 0.005"  # scripted group (container) (typed FeaturePython)
  n = 0.002
FEATURE [App::DocumentObjectGroupPython] Cl_element003  label="Cl_element : 0.004"  # scripted group (container) (typed FeaturePython)
  n = 0.003
FEATURE [App::DocumentObjectGroupPython] K_element002  label="K_element : 0.003"  # scripted group (container) (typed FeaturePython)
  n = 0.003
FEATURE [App::DocumentObjectGroupPython] G4_BRAIN_ICRP  # scripted group (container) (typed FeaturePython)
  Dunit = g/cm3
  Dvalue = 1.04
  Group = -> [H_element017,C_element018,N_element012,O_element017,Na_element004,P_element004,S_element006,Cl_element003,K_element002]
  conduct = 2
  density = 1
  expand = 3
  formula = G4_BRAIN_ICRP
  name = G4_BRAIN_ICRP
  specific = 4
FEATURE [App::DocumentObjectGroupPython] C_element019  label="C_element : 4"  # scripted group (container) (typed FeaturePython)
  n = 4
  ref = C_element
FEATURE [App::DocumentObjectGroupPython] H_element018  label="H_element : 010"  # scripted group (container) (typed FeaturePython)
  n = 10
  ref = H_element
FEATURE [App::DocumentObjectGroupPython] G4_BUTANE  # scripted group (container) (typed FeaturePython)
  Dunit = g/cm3
  Dvalue = 0.00249343
  Group = -> [C_element019,H_element018]
  conduct = 2
  density = 1
  expand = 3
  formula = G4_BUTANE
  name = G4_BUTANE
  specific = 4
FEATURE [App::DocumentObjectGroupPython] C_element020  label="C_element : 008"  # scripted group (container) (typed FeaturePython)
  n = 4
  ref = C_element
FEATURE [App::DocumentObjectGroupPython] H_element019  label="H_element : 011"  # scripted group (container) (typed FeaturePython)
  n = 10
  ref = H_element
FEATURE [App::DocumentObjectGroupPython] O_element018  label="O_element : 007"  # scripted group (container) (typed FeaturePython)
  n = 1
  ref = O_element
FEATURE [App::DocumentObjectGroupPython] G4_N_BUTYL_ALCOHOL  label="G4_N-BUTYL_ALCOHOL"  # scripted group (container) (typed FeaturePython)
  Dunit = g/cm3
  Dvalue = 0.8098
  Group = -> [C_element020,H_element019,O_element018]
  conduct = 2
  density = 1
  expand = 3
  formula = G4_N-BUTYL_ALCOHOL
  name = G4_N-BUTYL_ALCOHOL
  specific = 4
FEATURE [App::DocumentObjectGroupPython] H_element020  label="H_element : 0.025"  # scripted group (container) (typed FeaturePython)
  n = 0.02468
FEATURE [App::DocumentObjectGroupPython] C_element021  label="C_element : 0.502"  # scripted group (container) (typed FeaturePython)
  n = 0.501611
FEATURE [App::DocumentObjectGroupPython] O_element019  label="O_element : 0.005"  # scripted group (container) (typed FeaturePython)
  n = 0.004527
FEATURE [App::DocumentObjectGroupPython] F_element004  label="F_element : 0.465"  # scripted group (container) (typed FeaturePython)
  n = 0.465209
FEATURE [App::DocumentObjectGroupPython] Si_element001  label="Si_element : 0.004"  # scripted group (container) (typed FeaturePython)
  n = 0.003973
FEATURE [App::DocumentObjectGroupPython] G4_C_552  label="G4_C-552"  # scripted group (container) (typed FeaturePython)
  Dunit = g/cm3
  Dvalue = 1.76
  Group = -> [H_element020,C_element021,O_element019,F_element004,Si_element001]
  conduct = 2
  density = 1
  expand = 3
  formula = G4_C-552
  name = G4_C-552
  specific = 4
FEATURE [App::DocumentObjectGroupPython] Cd_element001  label="Cd_element : 1"  # scripted group (container) (typed FeaturePython)
  n = 1
  ref = Cd_element
FEATURE [App::DocumentObjectGroupPython] Te_element001  label="Te_element : 1"  # scripted group (container) (typed FeaturePython)
  n = 1
  ref = Te_element
FEATURE [App::DocumentObjectGroupPython] G4_CADMIUM_TELLURIDE  # scripted group (container) (typed FeaturePython)
  Dunit = g/cm3
  Dvalue = 6.2
  Group = -> [Cd_element001,Te_element001]
  conduct = 2
  density = 1
  expand = 3
  formula = G4_CADMIUM_TELLURIDE
  name = G4_CADMIUM_TELLURIDE
  specific = 4
FEATURE [App::DocumentObjectGroupPython] Cd_element002  label="Cd_element : 002"  # scripted group (container) (typed FeaturePython)
  n = 1
  ref = Cd_element
FEATURE [App::DocumentObjectGroupPython] W_element001  label="W_element : 1"  # scripted group (container) (typed FeaturePython)
  n = 1
  ref = W_element
FEATURE [App::DocumentObjectGroupPython] O_element020  label="O_element : 008"  # scripted group (container) (typed FeaturePython)
  n = 4
  ref = O_element
FEATURE [App::DocumentObjectGroupPython] G4_CADMIUM_TUNGSTATE  # scripted group (container) (typed FeaturePython)
  Dunit = g/cm3
  Dvalue = 7.9
  Group = -> [Cd_element002,W_element001,O_element020]
  conduct = 2
  density = 1
  expand = 3
  formula = G4_CADMIUM_TUNGSTATE
  name = G4_CADMIUM_TUNGSTATE
  specific = 4
FEATURE [App::DocumentObjectGroupPython] Ca_element005  label="Ca_element : 1"  # scripted group (container) (typed FeaturePython)
  n = 1
  ref = Ca_element
FEATURE [App::DocumentObjectGroupPython] C_element022  label="C_element : 009"  # scripted group (container) (typed FeaturePython)
  n = 1
  ref = C_element
FEATURE [App::DocumentObjectGroupPython] O_element021  label="O_element : 009"  # scripted group (container) (typed FeaturePython)
  n = 3
  ref = O_element
FEATURE [App::DocumentObjectGroupPython] G4_CALCIUM_CARBONATE  # scripted group (container) (typed FeaturePython)
  Dunit = g/cm3
  Dvalue = 2.8
  Group = -> [Ca_element005,C_element022,O_element021]
  conduct = 2
  density = 1
  expand = 3
  formula = G4_CALCIUM_CARBONATE
  name = G4_CALCIUM_CARBONATE
  specific = 4
FEATURE [App::DocumentObjectGroupPython] Ca_element006  label="Ca_element : 002"  # scripted group (container) (typed FeaturePython)
  n = 1
  ref = Ca_element
FEATURE [App::DocumentObjectGroupPython] F_element005  label="F_element : 003"  # scripted group (container) (typed FeaturePython)
  n = 2
  ref = F_element
FEATURE [App::DocumentObjectGroupPython] G4_CALCIUM_FLUORIDE  # scripted group (container) (typed FeaturePython)
  Dunit = g/cm3
  Dvalue = 3.18
  Group = -> [Ca_element006,F_element005]
  conduct = 2
  density = 1
  expand = 3
  formula = G4_CALCIUM_FLUORIDE
  name = G4_CALCIUM_FLUORIDE
  specific = 4
FEATURE [App::DocumentObjectGroupPython] Ca_element007  label="Ca_element : 003"  # scripted group (container) (typed FeaturePython)
  n = 1
  ref = Ca_element
FEATURE [App::DocumentObjectGroupPython] O_element022  label="O_element : 010"  # scripted group (container) (typed FeaturePython)
  n = 1
  ref = O_element
FEATURE [App::DocumentObjectGroupPython] G4_CALCIUM_OXIDE  # scripted group (container) (typed FeaturePython)
  Dunit = g/cm3
  Dvalue = 3.3
  Group = -> [Ca_element007,O_element022]
  conduct = 2
  density = 1
  expand = 3
  formula = G4_CALCIUM_OXIDE
  name = G4_CALCIUM_OXIDE
  specific = 4
FEATURE [App::DocumentObjectGroupPython] Ca_element008  label="Ca_element : 004"  # scripted group (container) (typed FeaturePython)
  n = 1
  ref = Ca_element
FEATURE [App::DocumentObjectGroupPython] S_element007  label="S_element : 002"  # scripted group (container) (typed FeaturePython)
  n = 1
  ref = S_element
FEATURE [App::DocumentObjectGroupPython] O_element023  label="O_element : 011"  # scripted group (container) (typed FeaturePython)
  n = 4
  ref = O_element
FEATURE [App::DocumentObjectGroupPython] G4_CALCIUM_SULFATE  # scripted group (container) (typed FeaturePython)
  Dunit = g/cm3
  Dvalue = 2.96
  Group = -> [Ca_element008,S_element007,O_element023]
  conduct = 2
  density = 1
  expand = 3
  formula = G4_CALCIUM_SULFATE
  name = G4_CALCIUM_SULFATE
  specific = 4
FEATURE [App::DocumentObjectGroupPython] Ca_element009  label="Ca_element : 005"  # scripted group (container) (typed FeaturePython)
  n = 1
  ref = Ca_element
FEATURE [App::DocumentObjectGroupPython] W_element002  label="W_element : 002"  # scripted group (container) (typed FeaturePython)
  n = 1
  ref = W_element
FEATURE [App::DocumentObjectGroupPython] O_element024  label="O_element : 012"  # scripted group (container) (typed FeaturePython)
  n = 4
  ref = O_element
FEATURE [App::DocumentObjectGroupPython] G4_CALCIUM_TUNGSTATE  # scripted group (container) (typed FeaturePython)
  Dunit = g/cm3
  Dvalue = 6.062
  Group = -> [Ca_element009,W_element002,O_element024]
  conduct = 2
  density = 1
  expand = 3
  formula = G4_CALCIUM_TUNGSTATE
  name = G4_CALCIUM_TUNGSTATE
  specific = 4
FEATURE [App::DocumentObjectGroupPython] C_element023  label="C_element : 010"  # scripted group (container) (typed FeaturePython)
  n = 1
  ref = C_element
FEATURE [App::DocumentObjectGroupPython] O_element025  label="O_element : 013"  # scripted group (container) (typed FeaturePython)
  n = 2
  ref = O_element
FEATURE [App::DocumentObjectGroupPython] G4_CARBON_DIOXIDE  # scripted group (container) (typed FeaturePython)
  Dunit = g/cm3
  Dvalue = 0.00184212
  Group = -> [C_element023,O_element025]
  conduct = 2
  density = 1
  expand = 3
  formula = G4_CARBON_DIOXIDE
  name = G4_CARBON_DIOXIDE
  specific = 4
FEATURE [App::DocumentObjectGroupPython] C_element024  label="C_element : 011"  # scripted group (container) (typed FeaturePython)
  n = 1
  ref = C_element
FEATURE [App::DocumentObjectGroupPython] Cl_element004  label="Cl_element : 4"  # scripted group (container) (typed FeaturePython)
  n = 4
  ref = Cl_element
FEATURE [App::DocumentObjectGroupPython] G4_CARBON_TETRACHLORIDE  # scripted group (container) (typed FeaturePython)
  Dunit = g/cm3
  Dvalue = 1.594
  Group = -> [C_element024,Cl_element004]
  conduct = 2
  density = 1
  expand = 3
  formula = G4_CARBON_TETRACHLORIDE
  name = G4_CARBON_TETRACHLORIDE
  specific = 4
FEATURE [App::DocumentObjectGroupPython] C_element025  label="C_element : 012"  # scripted group (container) (typed FeaturePython)
  n = 6
  ref = C_element
FEATURE [App::DocumentObjectGroupPython] H_element021  label="H_element : 012"  # scripted group (container) (typed FeaturePython)
  n = 10
  ref = H_element
FEATURE [App::DocumentObjectGroupPython] O_element026  label="O_element : 5"  # scripted group (container) (typed FeaturePython)
  n = 5
  ref = O_element
FEATURE [App::DocumentObjectGroupPython] G4_CELLULOSE_CELLOPHANE  # scripted group (container) (typed FeaturePython)
  Dunit = g/cm3
  Dvalue = 1.42
  Group = -> [C_element025,H_element021,O_element026]
  conduct = 2
  density = 1
  expand = 3
  formula = G4_CELLULOSE_CELLOPHANE
  name = G4_CELLULOSE_CELLOPHANE
  specific = 4
FEATURE [App::DocumentObjectGroupPython] H_element022  label="H_element : 0.067"  # scripted group (container) (typed FeaturePython)
  n = 0.067125
FEATURE [App::DocumentObjectGroupPython] C_element026  label="C_element : 0.545"  # scripted group (container) (typed FeaturePython)
  n = 0.545403
FEATURE [App::DocumentObjectGroupPython] O_element027  label="O_element : 0.387"  # scripted group (container) (typed FeaturePython)
  n = 0.387472
FEATURE [App::DocumentObjectGroupPython] G4_CELLULOSE_BUTYRATE  # scripted group (container) (typed FeaturePython)
  Dunit = g/cm3
  Dvalue = 1.2
  Group = -> [H_element022,C_element026,O_element027]
  conduct = 2
  density = 1
  expand = 3
  formula = G4_CELLULOSE_BUTYRATE
  name = G4_CELLULOSE_BUTYRATE
  specific = 4
FEATURE [App::DocumentObjectGroupPython] H_element023  label="H_element : 0.029"  # scripted group (container) (typed FeaturePython)
  n = 0.029216
FEATURE [App::DocumentObjectGroupPython] C_element027  label="C_element : 0.271"  # scripted group (container) (typed FeaturePython)
  n = 0.271296
FEATURE [App::DocumentObjectGroupPython] N_element013  label="N_element : 0.121"  # scripted group (container) (typed FeaturePython)
  n = 0.121276
FEATURE [App::DocumentObjectGroupPython] O_element028  label="O_element : 0.578"  # scripted group (container) (typed FeaturePython)
  n = 0.578212
FEATURE [App::DocumentObjectGroupPython] G4_CELLULOSE_NITRATE  # scripted group (container) (typed FeaturePython)
  Dunit = g/cm3
  Dvalue = 1.49
  Group = -> [H_element023,C_element027,N_element013,O_element028]
  conduct = 2
  density = 1
  expand = 3
  formula = G4_CELLULOSE_NITRATE
  name = G4_CELLULOSE_NITRATE
  specific = 4
FEATURE [App::DocumentObjectGroupPython] H_element024  label="H_element : 0.108"  # scripted group (container) (typed FeaturePython)
  n = 0.107596
FEATURE [App::DocumentObjectGroupPython] N_element014  label="N_element : 0.001"  # scripted group (container) (typed FeaturePython)
  n = 0.0008
FEATURE [App::DocumentObjectGroupPython] O_element029  label="O_element : 0.875"  # scripted group (container) (typed FeaturePython)
  n = 0.874976
FEATURE [App::DocumentObjectGroupPython] S_element008  label="S_element : 0.015"  # scripted group (container) (typed FeaturePython)
  n = 0.014627
FEATURE [App::DocumentObjectGroupPython] Ce_element001  label="Ce_element : 0.002"  # scripted group (container) (typed FeaturePython)
  n = 0.002001
FEATURE [App::DocumentObjectGroupPython] G4_CERIC_SULFATE  # scripted group (container) (typed FeaturePython)
  Dunit = g/cm3
  Dvalue = 1.03
  Group = -> [H_element024,N_element014,O_element029,S_element008,Ce_element001]
  conduct = 2
  density = 1
  expand = 3
  formula = G4_CERIC_SULFATE
  name = G4_CERIC_SULFATE
  specific = 4
FEATURE [App::DocumentObjectGroupPython] Cs_element001  label="Cs_element : 1"  # scripted group (container) (typed FeaturePython)
  n = 1
  ref = Cs_element
FEATURE [App::DocumentObjectGroupPython] F_element006  label="F_element : 1"  # scripted group (container) (typed FeaturePython)
  n = 1
  ref = F_element
FEATURE [App::DocumentObjectGroupPython] G4_CESIUM_FLUORIDE  # scripted group (container) (typed FeaturePython)
  Dunit = g/cm3
  Dvalue = 4.115
  Group = -> [Cs_element001,F_element006]
  conduct = 2
  density = 1
  expand = 3
  formula = G4_CESIUM_FLUORIDE
  name = G4_CESIUM_FLUORIDE
  specific = 4
FEATURE [App::DocumentObjectGroupPython] Cs_element002  label="Cs_element : 002"  # scripted group (container) (typed FeaturePython)
  n = 1
  ref = Cs_element
FEATURE [App::DocumentObjectGroupPython] I_element001  label="I_element : 1"  # scripted group (container) (typed FeaturePython)
  n = 1
  ref = I_element
FEATURE [App::DocumentObjectGroupPython] G4_CESIUM_IODIDE  # scripted group (container) (typed FeaturePython)
  Dunit = g/cm3
  Dvalue = 4.51
  Group = -> [Cs_element002,I_element001]
  conduct = 2
  density = 1
  expand = 3
  formula = G4_CESIUM_IODIDE
  name = G4_CESIUM_IODIDE
  specific = 4
FEATURE [App::DocumentObjectGroupPython] C_element028  label="C_element : 013"  # scripted group (container) (typed FeaturePython)
  n = 6
  ref = C_element
FEATURE [App::DocumentObjectGroupPython] H_element025  label="H_element : 013"  # scripted group (container) (typed FeaturePython)
  n = 5
  ref = H_element
FEATURE [App::DocumentObjectGroupPython] Cl_element005  label="Cl_element : 1"  # scripted group (container) (typed FeaturePython)
  n = 1
  ref = Cl_element
FEATURE [App::DocumentObjectGroupPython] G4_CHLOROBENZENE  # scripted group (container) (typed FeaturePython)
  Dunit = g/cm3
  Dvalue = 1.1058
  Group = -> [C_element028,H_element025,Cl_element005]
  conduct = 2
  density = 1
  expand = 3
  formula = G4_CHLOROBENZENE
  name = G4_CHLOROBENZENE
  specific = 4
FEATURE [App::DocumentObjectGroupPython] C_element029  label="C_element : 014"  # scripted group (container) (typed FeaturePython)
  n = 1
  ref = C_element
FEATURE [App::DocumentObjectGroupPython] H_element026  label="H_element : 1"  # scripted group (container) (typed FeaturePython)
  n = 1
  ref = H_element
FEATURE [App::DocumentObjectGroupPython] Cl_element006  label="Cl_element : 3"  # scripted group (container) (typed FeaturePython)
  n = 3
  ref = Cl_element
FEATURE [App::DocumentObjectGroupPython] G4_CHLOROFORM  # scripted group (container) (typed FeaturePython)
  Dunit = g/cm3
  Dvalue = 1.4832
  Group = -> [C_element029,H_element026,Cl_element006]
  conduct = 2
  density = 1
  expand = 3
  formula = G4_CHLOROFORM
  name = G4_CHLOROFORM
  specific = 4
FEATURE [App::DocumentObjectGroupPython] H_element027  label="H_element : 0.010"  # scripted group (container) (typed FeaturePython)
  n = 0.01
FEATURE [App::DocumentObjectGroupPython] C_element030  label="C_element : 0.001"  # scripted group (container) (typed FeaturePython)
  n = 0.001
FEATURE [App::DocumentObjectGroupPython] O_element030  label="O_element : 0.529"  # scripted group (container) (typed FeaturePython)
  n = 0.529107
FEATURE [App::DocumentObjectGroupPython] Na_element005  label="Na_element : 0.016"  # scripted group (container) (typed FeaturePython)
  n = 0.016
FEATURE [App::DocumentObjectGroupPython] Mg_element003  label="Mg_element : 0.004"  # scripted group (container) (typed FeaturePython)
  n = 0.002
FEATURE [App::DocumentObjectGroupPython] Al_element002  label="Al_element : 0.034"  # scripted group (container) (typed FeaturePython)
  n = 0.033872
FEATURE [App::DocumentObjectGroupPython] Si_element002  label="Si_element : 0.337"  # scripted group (container) (typed FeaturePython)
  n = 0.337021
FEATURE [App::DocumentObjectGroupPython] K_element003  label="K_element : 0.013"  # scripted group (container) (typed FeaturePython)
  n = 0.013
FEATURE [App::DocumentObjectGroupPython] Ca_element010  label="Ca_element : 0.044"  # scripted group (container) (typed FeaturePython)
  n = 0.044
FEATURE [App::DocumentObjectGroupPython] Fe_element002  label="Fe_element : 0.014"  # scripted group (container) (typed FeaturePython)
  n = 0.014
FEATURE [App::DocumentObjectGroupPython] G4_CONCRETE  # scripted group (container) (typed FeaturePython)
  Dunit = g/cm3
  Dvalue = 2.3
  Group = -> [H_element027,C_element030,O_element030,Na_element005,Mg_element003,Al_element002,Si_element002,K_element003,Ca_element010,Fe_element002]
  conduct = 2
  density = 1
  expand = 3
  formula = G4_CONCRETE
  name = G4_CONCRETE
  specific = 4
FEATURE [App::DocumentObjectGroupPython] C_element031  label="C_element : 015"  # scripted group (container) (typed FeaturePython)
  n = 6
  ref = C_element
FEATURE [App::DocumentObjectGroupPython] H_element028  label="H_element : 12"  # scripted group (container) (typed FeaturePython)
  n = 12
  ref = H_element
FEATURE [App::DocumentObjectGroupPython] G4_CYCLOHEXANE  # scripted group (container) (typed FeaturePython)
  Dunit = g/cm3
  Dvalue = 0.779
  Group = -> [C_element031,H_element028]
  conduct = 2
  density = 1
  expand = 3
  formula = G4_CYCLOHEXANE
  name = G4_CYCLOHEXANE
  specific = 4
FEATURE [App::DocumentObjectGroupPython] C_element032  label="C_element : 016"  # scripted group (container) (typed FeaturePython)
  n = 6
  ref = C_element
FEATURE [App::DocumentObjectGroupPython] H_element029  label="H_element : 4"  # scripted group (container) (typed FeaturePython)
  n = 4
  ref = H_element
FEATURE [App::DocumentObjectGroupPython] Cl_element007  label="Cl_element : 2"  # scripted group (container) (typed FeaturePython)
  n = 2
  ref = Cl_element
FEATURE [App::DocumentObjectGroupPython] G4_1_2_DICHLOROBENZENE  label="G4_1.2-DICHLOROBENZENE"  # scripted group (container) (typed FeaturePython)
  Dunit = g/cm3
  Dvalue = 1.3048
  Group = -> [C_element032,H_element029,Cl_element007]
  conduct = 2
  density = 1
  expand = 3
  formula = G4_1.2-DICHLOROBENZENE
  name = G4_1.2-DICHLOROBENZENE
  specific = 4
FEATURE [App::DocumentObjectGroupPython] C_element033  label="C_element : 017"  # scripted group (container) (typed FeaturePython)
  n = 4
  ref = C_element
FEATURE [App::DocumentObjectGroupPython] H_element030  label="H_element : 8"  # scripted group (container) (typed FeaturePython)
  n = 8
  ref = H_element
FEATURE [App::DocumentObjectGroupPython] O_element031  label="O_element : 014"  # scripted group (container) (typed FeaturePython)
  n = 1
  ref = O_element
FEATURE [App::DocumentObjectGroupPython] Cl_element008  label="Cl_element : 005"  # scripted group (container) (typed FeaturePython)
  n = 2
  ref = Cl_element
FEATURE [App::DocumentObjectGroupPython] G4_DICHLORODIETHYL_ETHER  # scripted group (container) (typed FeaturePython)
  Dunit = g/cm3
  Dvalue = 1.2199
  Group = -> [C_element033,H_element030,O_element031,Cl_element008]
  conduct = 2
  density = 1
  expand = 3
  formula = G4_DICHLORODIETHYL_ETHER
  name = G4_DICHLORODIETHYL_ETHER
  specific = 4
FEATURE [App::DocumentObjectGroupPython] C_element034  label="C_element : 018"  # scripted group (container) (typed FeaturePython)
  n = 2
  ref = C_element
FEATURE [App::DocumentObjectGroupPython] H_element031  label="H_element : 014"  # scripted group (container) (typed FeaturePython)
  n = 4
  ref = H_element
FEATURE [App::DocumentObjectGroupPython] Cl_element009  label="Cl_element : 006"  # scripted group (container) (typed FeaturePython)
  n = 2
  ref = Cl_element
FEATURE [App::DocumentObjectGroupPython] G4_1_2_DICHLOROETHANE  label="G4_1.2-DICHLOROETHANE"  # scripted group (container) (typed FeaturePython)
  Dunit = g/cm3
  Dvalue = 1.2351
  Group = -> [C_element034,H_element031,Cl_element009]
  conduct = 2
  density = 1
  expand = 3
  formula = G4_1.2-DICHLOROETHANE
  name = G4_1.2-DICHLOROETHANE
  specific = 4
FEATURE [App::DocumentObjectGroupPython] C_element035  label="C_element : 019"  # scripted group (container) (typed FeaturePython)
  n = 4
  ref = C_element
FEATURE [App::DocumentObjectGroupPython] H_element032  label="H_element : 015"  # scripted group (container) (typed FeaturePython)
  n = 10
  ref = H_element
FEATURE [App::DocumentObjectGroupPython] O_element032  label="O_element : 015"  # scripted group (container) (typed FeaturePython)
  n = 1
  ref = O_element
FEATURE [App::DocumentObjectGroupPython] G4_DIETHYL_ETHER  # scripted group (container) (typed FeaturePython)
  Dunit = g/cm3
  Dvalue = 0.71378
  Group = -> [C_element035,H_element032,O_element032]
  conduct = 2
  density = 1
  expand = 3
  formula = G4_DIETHYL_ETHER
  name = G4_DIETHYL_ETHER
  specific = 4
FEATURE [App::DocumentObjectGroupPython] C_element036  label="C_element : 020"  # scripted group (container) (typed FeaturePython)
  n = 3
  ref = C_element
FEATURE [App::DocumentObjectGroupPython] H_element033  label="H_element : 016"  # scripted group (container) (typed FeaturePython)
  n = 7
  ref = H_element
FEATURE [App::DocumentObjectGroupPython] N_element015  label="N_element : 008"  # scripted group (container) (typed FeaturePython)
  n = 1
  ref = N_element
FEATURE [App::DocumentObjectGroupPython] O_element033  label="O_element : 016"  # scripted group (container) (typed FeaturePython)
  n = 1
  ref = O_element
FEATURE [App::DocumentObjectGroupPython] G4_N_N_DIMETHYL_FORMAMIDE  label="G4_N.N-DIMETHYL_FORMAMIDE"  # scripted group (container) (typed FeaturePython)
  Dunit = g/cm3
  Dvalue = 0.9487
  Group = -> [C_element036,H_element033,N_element015,O_element033]
  conduct = 2
  density = 1
  expand = 3
  formula = G4_N.N-DIMETHYL_FORMAMIDE
  name = G4_N.N-DIMETHYL_FORMAMIDE
  specific = 4
FEATURE [App::DocumentObjectGroupPython] C_element037  label="C_element : 021"  # scripted group (container) (typed FeaturePython)
  n = 2
  ref = C_element
FEATURE [App::DocumentObjectGroupPython] H_element034  label="H_element : 017"  # scripted group (container) (typed FeaturePython)
  n = 6
  ref = H_element
FEATURE [App::DocumentObjectGroupPython] O_element034  label="O_element : 017"  # scripted group (container) (typed FeaturePython)
  n = 1
  ref = O_element
FEATURE [App::DocumentObjectGroupPython] S_element009  label="S_element : 003"  # scripted group (container) (typed FeaturePython)
  n = 1
  ref = S_element
FEATURE [App::DocumentObjectGroupPython] G4_DIMETHYL_SULFOXIDE  # scripted group (container) (typed FeaturePython)
  Dunit = g/cm3
  Dvalue = 1.1014
  Group = -> [C_element037,H_element034,O_element034,S_element009]
  conduct = 2
  density = 1
  expand = 3
  formula = G4_DIMETHYL_SULFOXIDE
  name = G4_DIMETHYL_SULFOXIDE
  specific = 4
FEATURE [App::DocumentObjectGroupPython] C_element038  label="C_element : 022"  # scripted group (container) (typed FeaturePython)
  n = 2
  ref = C_element
FEATURE [App::DocumentObjectGroupPython] H_element035  label="H_element : 018"  # scripted group (container) (typed FeaturePython)
  n = 6
  ref = H_element
FEATURE [App::DocumentObjectGroupPython] G4_ETHANE  # scripted group (container) (typed FeaturePython)
  Dunit = g/cm3
  Dvalue = 0.00125324
  Group = -> [C_element038,H_element035]
  conduct = 2
  density = 1
  expand = 3
  formula = G4_ETHANE
  name = G4_ETHANE
  specific = 4
FEATURE [App::DocumentObjectGroupPython] C_element039  label="C_element : 023"  # scripted group (container) (typed FeaturePython)
  n = 2
  ref = C_element
FEATURE [App::DocumentObjectGroupPython] H_element036  label="H_element : 019"  # scripted group (container) (typed FeaturePython)
  n = 6
  ref = H_element
FEATURE [App::DocumentObjectGroupPython] O_element035  label="O_element : 018"  # scripted group (container) (typed FeaturePython)
  n = 1
  ref = O_element
FEATURE [App::DocumentObjectGroupPython] G4_ETHYL_ALCOHOL  # scripted group (container) (typed FeaturePython)
  Dunit = g/cm3
  Dvalue = 0.7893
  Group = -> [C_element039,H_element036,O_element035]
  conduct = 2
  density = 1
  expand = 3
  formula = G4_ETHYL_ALCOHOL
  name = G4_ETHYL_ALCOHOL
  specific = 4
FEATURE [App::DocumentObjectGroupPython] H_element037  label="H_element : 0.090"  # scripted group (container) (typed FeaturePython)
  n = 0.090027
FEATURE [App::DocumentObjectGroupPython] C_element040  label="C_element : 0.585"  # scripted group (container) (typed FeaturePython)
  n = 0.585182
FEATURE [App::DocumentObjectGroupPython] O_element036  label="O_element : 0.325"  # scripted group (container) (typed FeaturePython)
  n = 0.324791
FEATURE [App::DocumentObjectGroupPython] G4_ETHYL_CELLULOSE  # scripted group (container) (typed FeaturePython)
  Dunit = g/cm3
  Dvalue = 1.13
  Group = -> [H_element037,C_element040,O_element036]
  conduct = 2
  density = 1
  expand = 3
  formula = G4_ETHYL_CELLULOSE
  name = G4_ETHYL_CELLULOSE
  specific = 4
FEATURE [App::DocumentObjectGroupPython] C_element041  label="C_element : 024"  # scripted group (container) (typed FeaturePython)
  n = 2
  ref = C_element
FEATURE [App::DocumentObjectGroupPython] H_element038  label="H_element : 020"  # scripted group (container) (typed FeaturePython)
  n = 4
  ref = H_element
FEATURE [App::DocumentObjectGroupPython] G4_ETHYLENE  # scripted group (container) (typed FeaturePython)
  Dunit = g/cm3
  Dvalue = 0.00117497
  Group = -> [C_element041,H_element038]
  conduct = 2
  density = 1
  expand = 3
  formula = G4_ETHYLENE
  name = G4_ETHYLENE
  specific = 4
FEATURE [App::DocumentObjectGroupPython] H_element039  label="H_element : 0.096"  # scripted group (container) (typed FeaturePython)
  n = 0.096
FEATURE [App::DocumentObjectGroupPython] C_element042  label="C_element : 0.195"  # scripted group (container) (typed FeaturePython)
  n = 0.195
FEATURE [App::DocumentObjectGroupPython] N_element016  label="N_element : 0.057"  # scripted group (container) (typed FeaturePython)
  n = 0.057
FEATURE [App::DocumentObjectGroupPython] O_element037  label="O_element : 0.646"  # scripted group (container) (typed FeaturePython)
  n = 0.646
FEATURE [App::DocumentObjectGroupPython] Na_element006  label="Na_element : 0.017"  # scripted group (container) (typed FeaturePython)
  n = 0.001
FEATURE [App::DocumentObjectGroupPython] P_element005  label="P_element : 0.104"  # scripted group (container) (typed FeaturePython)
  n = 0.001
FEATURE [App::DocumentObjectGroupPython] S_element010  label="S_element : 0.016"  # scripted group (container) (typed FeaturePython)
  n = 0.003
FEATURE [App::DocumentObjectGroupPython] Cl_element010  label="Cl_element : 0.005"  # scripted group (container) (typed FeaturePython)
  n = 0.001
FEATURE [App::DocumentObjectGroupPython] G4_EYE_LENS_ICRP  # scripted group (container) (typed FeaturePython)
  Dunit = g/cm3
  Dvalue = 1.07
  Group = -> [H_element039,C_element042,N_element016,O_element037,Na_element006,P_element005,S_element010,Cl_element010]
  conduct = 2
  density = 1
  expand = 3
  formula = G4_EYE_LENS_ICRP
  name = G4_EYE_LENS_ICRP
  specific = 4
FEATURE [App::DocumentObjectGroupPython] Fe_element003  label="Fe_element : 2"  # scripted group (container) (typed FeaturePython)
  n = 2
  ref = Fe_element
FEATURE [App::DocumentObjectGroupPython] O_element038  label="O_element : 019"  # scripted group (container) (typed FeaturePython)
  n = 3
  ref = O_element
FEATURE [App::DocumentObjectGroupPython] G4_FERRIC_OXIDE  # scripted group (container) (typed FeaturePython)
  Dunit = g/cm3
  Dvalue = 5.2
  Group = -> [Fe_element003,O_element038]
  conduct = 2
  density = 1
  expand = 3
  formula = G4_FERRIC_OXIDE
  name = G4_FERRIC_OXIDE
  specific = 4
FEATURE [App::DocumentObjectGroupPython] Fe_element004  label="Fe_element : 1"  # scripted group (container) (typed FeaturePython)
  n = 1
  ref = Fe_element
FEATURE [App::DocumentObjectGroupPython] B_element003  label="B_element : 1"  # scripted group (container) (typed FeaturePython)
  n = 1
  ref = B_element
FEATURE [App::DocumentObjectGroupPython] G4_FERROBORIDE  # scripted group (container) (typed FeaturePython)
  Dunit = g/cm3
  Dvalue = 7.15
  Group = -> [Fe_element004,B_element003]
  conduct = 2
  density = 1
  expand = 3
  formula = G4_FERROBORIDE
  name = G4_FERROBORIDE
  specific = 4
FEATURE [App::DocumentObjectGroupPython] Fe_element005  label="Fe_element : 003"  # scripted group (container) (typed FeaturePython)
  n = 1
  ref = Fe_element
FEATURE [App::DocumentObjectGroupPython] O_element039  label="O_element : 020"  # scripted group (container) (typed FeaturePython)
  n = 1
  ref = O_element
FEATURE [App::DocumentObjectGroupPython] G4_FERROUS_OXIDE  # scripted group (container) (typed FeaturePython)
  Dunit = g/cm3
  Dvalue = 5.7
  Group = -> [Fe_element005,O_element039]
  conduct = 2
  density = 1
  expand = 3
  formula = G4_FERROUS_OXIDE
  name = G4_FERROUS_OXIDE
  specific = 4
FEATURE [App::DocumentObjectGroupPython] H_element040  label="H_element : 0.115"  # scripted group (container) (typed FeaturePython)
  n = 0.108259
FEATURE [App::DocumentObjectGroupPython] N_element017  label="N_element : 0.000"  # scripted group (container) (typed FeaturePython)
  n = 2.7e-05
FEATURE [App::DocumentObjectGroupPython] O_element040  label="O_element : 0.879"  # scripted group (container) (typed FeaturePython)
  n = 0.878636
FEATURE [App::DocumentObjectGroupPython] Na_element007  label="Na_element : 0.000"  # scripted group (container) (typed FeaturePython)
  n = 2.2e-05
FEATURE [App::DocumentObjectGroupPython] S_element011  label="S_element : 0.013"  # scripted group (container) (typed FeaturePython)
  n = 0.012968
FEATURE [App::DocumentObjectGroupPython] Cl_element011  label="Cl_element : 0.000"  # scripted group (container) (typed FeaturePython)
  n = 3.4e-05
FEATURE [App::DocumentObjectGroupPython] Fe_element006  label="Fe_element : 0.000"  # scripted group (container) (typed FeaturePython)
  n = 5.4e-05
FEATURE [App::DocumentObjectGroupPython] G4_FERROUS_SULFATE  # scripted group (container) (typed FeaturePython)
  Dunit = g/cm3
  Dvalue = 1.024
  Group = -> [H_element040,N_element017,O_element040,Na_element007,S_element011,Cl_element011,Fe_element006]
  conduct = 2
  density = 1
  expand = 3
  formula = G4_FERROUS_SULFATE
  name = G4_FERROUS_SULFATE
  specific = 4
FEATURE [App::DocumentObjectGroupPython] C_element043  label="C_element : 0.099"  # scripted group (container) (typed FeaturePython)
  n = 0.099335
FEATURE [App::DocumentObjectGroupPython] F_element007  label="F_element : 0.314"  # scripted group (container) (typed FeaturePython)
  n = 0.314247
FEATURE [App::DocumentObjectGroupPython] Cl_element012  label="Cl_element : 0.586"  # scripted group (container) (typed FeaturePython)
  n = 0.586418
FEATURE [App::DocumentObjectGroupPython] G4_FREON_12  label="G4_FREON-12"  # scripted group (container) (typed FeaturePython)
  Dunit = g/cm3
  Dvalue = 1.12
  Group = -> [C_element043,F_element007,Cl_element012]
  conduct = 2
  density = 1
  expand = 3
  formula = G4_FREON-12
  name = G4_FREON-12
  specific = 4
FEATURE [App::DocumentObjectGroupPython] C_element044  label="C_element : 0.057"  # scripted group (container) (typed FeaturePython)
  n = 0.057245
FEATURE [App::DocumentObjectGroupPython] F_element008  label="F_element : 0.181"  # scripted group (container) (typed FeaturePython)
  n = 0.181096
FEATURE [App::DocumentObjectGroupPython] Br_element001  label="Br_element : 0.762"  # scripted group (container) (typed FeaturePython)
  n = 0.761659
FEATURE [App::DocumentObjectGroupPython] G4_FREON_12B2  label="G4_FREON-12B2"  # scripted group (container) (typed FeaturePython)
  Dunit = g/cm3
  Dvalue = 1.8
  Group = -> [C_element044,F_element008,Br_element001]
  conduct = 2
  density = 1
  expand = 3
  formula = G4_FREON-12B2
  name = G4_FREON-12B2
  specific = 4
FEATURE [App::DocumentObjectGroupPython] C_element045  label="C_element : 0.115"  # scripted group (container) (typed FeaturePython)
  n = 0.114983
FEATURE [App::DocumentObjectGroupPython] F_element009  label="F_element : 0.546"  # scripted group (container) (typed FeaturePython)
  n = 0.545621
FEATURE [App::DocumentObjectGroupPython] Cl_element013  label="Cl_element : 0.339"  # scripted group (container) (typed FeaturePython)
  n = 0.339396
FEATURE [App::DocumentObjectGroupPython] G4_FREON_13  label="G4_FREON-13"  # scripted group (container) (typed FeaturePython)
  Dunit = g/cm3
  Dvalue = 0.95
  Group = -> [C_element045,F_element009,Cl_element013]
  conduct = 2
  density = 1
  expand = 3
  formula = G4_FREON-13
  name = G4_FREON-13
  specific = 4
FEATURE [App::DocumentObjectGroupPython] C_element046  label="C_element : 025"  # scripted group (container) (typed FeaturePython)
  n = 1
  ref = C_element
FEATURE [App::DocumentObjectGroupPython] F_element010  label="F_element : 3"  # scripted group (container) (typed FeaturePython)
  n = 3
  ref = F_element
FEATURE [App::DocumentObjectGroupPython] Br_element002  label="Br_element : 1"  # scripted group (container) (typed FeaturePython)
  n = 1
  ref = Br_element
FEATURE [App::DocumentObjectGroupPython] G4_FREON_13B1  label="G4_FREON-13B1"  # scripted group (container) (typed FeaturePython)
  Dunit = g/cm3
  Dvalue = 1.5
  Group = -> [C_element046,F_element010,Br_element002]
  conduct = 2
  density = 1
  expand = 3
  formula = G4_FREON-13B1
  name = G4_FREON-13B1
  specific = 4
FEATURE [App::DocumentObjectGroupPython] C_element047  label="C_element : 0.061"  # scripted group (container) (typed FeaturePython)
  n = 0.061309
FEATURE [App::DocumentObjectGroupPython] F_element011  label="F_element : 0.291"  # scripted group (container) (typed FeaturePython)
  n = 0.290924
FEATURE [App::DocumentObjectGroupPython] I_element002  label="I_element : 0.648"  # scripted group (container) (typed FeaturePython)
  n = 0.647767
FEATURE [App::DocumentObjectGroupPython] G4_FREON_13I1  label="G4_FREON-13I1"  # scripted group (container) (typed FeaturePython)
  Dunit = g/cm3
  Dvalue = 1.8
  Group = -> [C_element047,F_element011,I_element002]
  conduct = 2
  density = 1
  expand = 3
  formula = G4_FREON-13I1
  name = G4_FREON-13I1
  specific = 4
FEATURE [App::DocumentObjectGroupPython] Gd_element001  label="Gd_element : 2"  # scripted group (container) (typed FeaturePython)
  n = 2
  ref = Gd_element
FEATURE [App::DocumentObjectGroupPython] O_element041  label="O_element : 021"  # scripted group (container) (typed FeaturePython)
  n = 2
  ref = O_element
FEATURE [App::DocumentObjectGroupPython] S_element012  label="S_element : 004"  # scripted group (container) (typed FeaturePython)
  n = 1
  ref = S_element
FEATURE [App::DocumentObjectGroupPython] G4_GADOLINIUM_OXYSULFIDE  # scripted group (container) (typed FeaturePython)
  Dunit = g/cm3
  Dvalue = 7.44
  Group = -> [Gd_element001,O_element041,S_element012]
  conduct = 2
  density = 1
  expand = 3
  formula = G4_GADOLINIUM_OXYSULFIDE
  name = G4_GADOLINIUM_OXYSULFIDE
  specific = 4
FEATURE [App::DocumentObjectGroupPython] Ga_element001  label="Ga_element : 1"  # scripted group (container) (typed FeaturePython)
  n = 1
  ref = Ga_element
FEATURE [App::DocumentObjectGroupPython] As_element001  label="As_element : 1"  # scripted group (container) (typed FeaturePython)
  n = 1
  ref = As_element
FEATURE [App::DocumentObjectGroupPython] G4_GALLIUM_ARSENIDE  # scripted group (container) (typed FeaturePython)
  Dunit = g/cm3
  Dvalue = 5.31
  Group = -> [Ga_element001,As_element001]
  conduct = 2
  density = 1
  expand = 3
  formula = G4_GALLIUM_ARSENIDE
  name = G4_GALLIUM_ARSENIDE
  specific = 4
FEATURE [App::DocumentObjectGroupPython] H_element041  label="H_element : 0.081"  # scripted group (container) (typed FeaturePython)
  n = 0.08118
FEATURE [App::DocumentObjectGroupPython] C_element048  label="C_element : 0.416"  # scripted group (container) (typed FeaturePython)
  n = 0.41606
FEATURE [App::DocumentObjectGroupPython] N_element018  label="N_element : 0.111"  # scripted group (container) (typed FeaturePython)
  n = 0.11124
FEATURE [App::DocumentObjectGroupPython] O_element042  label="O_element : 0.381"  # scripted group (container) (typed FeaturePython)
  n = 0.38064
FEATURE [App::DocumentObjectGroupPython] S_element013  label="S_element : 0.011"  # scripted group (container) (typed FeaturePython)
  n = 0.01088
FEATURE [App::DocumentObjectGroupPython] G4_GEL_PHOTO_EMULSION  # scripted group (container) (typed FeaturePython)
  Dunit = g/cm3
  Dvalue = 1.2914
  Group = -> [H_element041,C_element048,N_element018,O_element042,S_element013]
  conduct = 2
  density = 1
  expand = 3
  formula = G4_GEL_PHOTO_EMULSION
  name = G4_GEL_PHOTO_EMULSION
  specific = 4
FEATURE [App::DocumentObjectGroupPython] B_element004  label="B_element : 0.040"  # scripted group (container) (typed FeaturePython)
  n = 0.0400639
FEATURE [App::DocumentObjectGroupPython] O_element043  label="O_element : 0.540"  # scripted group (container) (typed FeaturePython)
  n = 0.539561
FEATURE [App::DocumentObjectGroupPython] Na_element008  label="Na_element : 0.028"  # scripted group (container) (typed FeaturePython)
  n = 0.0281909
FEATURE [App::DocumentObjectGroupPython] Al_element003  label="Al_element : 0.012"  # scripted group (container) (typed FeaturePython)
  n = 0.011644
FEATURE [App::DocumentObjectGroupPython] Si_element003  label="Si_element : 0.377"  # scripted group (container) (typed FeaturePython)
  n = 0.377219
FEATURE [App::DocumentObjectGroupPython] K_element004  label="K_element : 0.014"  # scripted group (container) (typed FeaturePython)
  n = 0.00332099
FEATURE [App::DocumentObjectGroupPython] G4_Pyrex_Glass  # scripted group (container) (typed FeaturePython)
  Dunit = g/cm3
  Dvalue = 2.23
  Group = -> [B_element004,O_element043,Na_element008,Al_element003,Si_element003,K_element004]
  conduct = 2
  density = 1
  expand = 3
  formula = G4_Pyrex_Glass
  name = G4_Pyrex_Glass
  specific = 4
FEATURE [App::DocumentObjectGroupPython] O_element044  label="O_element : 0.156"  # scripted group (container) (typed FeaturePython)
  n = 0.156453
FEATURE [App::DocumentObjectGroupPython] Si_element004  label="Si_element : 0.081"  # scripted group (container) (typed FeaturePython)
  n = 0.080866
FEATURE [App::DocumentObjectGroupPython] Ti_element001  label="Ti_element : 0.008"  # scripted group (container) (typed FeaturePython)
  n = 0.008092
FEATURE [App::DocumentObjectGroupPython] As_element002  label="As_element : 0.003"  # scripted group (container) (typed FeaturePython)
  n = 0.002651
FEATURE [App::DocumentObjectGroupPython] Pb_element001  label="Pb_element : 0.752"  # scripted group (container) (typed FeaturePython)
  n = 0.751938
FEATURE [App::DocumentObjectGroupPython] G4_GLASS_LEAD  # scripted group (container) (typed FeaturePython)
  Dunit = g/cm3
  Dvalue = 6.22
  Group = -> [O_element044,Si_element004,Ti_element001,As_element002,Pb_element001]
  conduct = 2
  density = 1
  expand = 3
  formula = G4_GLASS_LEAD
  name = G4_GLASS_LEAD
  specific = 4
FEATURE [App::DocumentObjectGroupPython] O_element045  label="O_element : 0.460"  # scripted group (container) (typed FeaturePython)
  n = 0.4598
FEATURE [App::DocumentObjectGroupPython] Na_element009  label="Na_element : 0.096"  # scripted group (container) (typed FeaturePython)
  n = 0.0964411
FEATURE [App::DocumentObjectGroupPython] Si_element005  label="Si_element : 0.378"  # scripted group (container) (typed FeaturePython)
  n = 0.336553
FEATURE [App::DocumentObjectGroupPython] Ca_element011  label="Ca_element : 0.107"  # scripted group (container) (typed FeaturePython)
  n = 0.107205
FEATURE [App::DocumentObjectGroupPython] G4_GLASS_PLATE  # scripted group (container) (typed FeaturePython)
  Dunit = g/cm3
  Dvalue = 2.4
  Group = -> [O_element045,Na_element009,Si_element005,Ca_element011]
  conduct = 2
  density = 1
  expand = 3
  formula = G4_GLASS_PLATE
  name = G4_GLASS_PLATE
  specific = 4
FEATURE [App::DocumentObjectGroupPython] C_element049  label="C_element : 026"  # scripted group (container) (typed FeaturePython)
  n = 5
  ref = C_element
FEATURE [App::DocumentObjectGroupPython] H_element042  label="H_element : 021"  # scripted group (container) (typed FeaturePython)
  n = 10
  ref = H_element
FEATURE [App::DocumentObjectGroupPython] N_element019  label="N_element : 2"  # scripted group (container) (typed FeaturePython)
  n = 2
  ref = N_element
FEATURE [App::DocumentObjectGroupPython] O_element046  label="O_element : 022"  # scripted group (container) (typed FeaturePython)
  n = 3
  ref = O_element
FEATURE [App::DocumentObjectGroupPython] G4_GLUTAMINE  # scripted group (container) (typed FeaturePython)
  Dunit = g/cm3
  Dvalue = 1.46
  Group = -> [C_element049,H_element042,N_element019,O_element046]
  conduct = 2
  density = 1
  expand = 3
  formula = G4_GLUTAMINE
  name = G4_GLUTAMINE
  specific = 4
FEATURE [App::DocumentObjectGroupPython] C_element050  label="C_element : 027"  # scripted group (container) (typed FeaturePython)
  n = 3
  ref = C_element
FEATURE [App::DocumentObjectGroupPython] H_element043  label="H_element : 022"  # scripted group (container) (typed FeaturePython)
  n = 8
  ref = H_element
FEATURE [App::DocumentObjectGroupPython] O_element047  label="O_element : 023"  # scripted group (container) (typed FeaturePython)
  n = 3
  ref = O_element
FEATURE [App::DocumentObjectGroupPython] G4_GLYCEROL  # scripted group (container) (typed FeaturePython)
  Dunit = g/cm3
  Dvalue = 1.2613
  Group = -> [C_element050,H_element043,O_element047]
  conduct = 2
  density = 1
  expand = 3
  formula = G4_GLYCEROL
  name = G4_GLYCEROL
  specific = 4
FEATURE [App::DocumentObjectGroupPython] C_element051  label="C_element : 028"  # scripted group (container) (typed FeaturePython)
  n = 5
  ref = C_element
FEATURE [App::DocumentObjectGroupPython] H_element044  label="H_element : 023"  # scripted group (container) (typed FeaturePython)
  n = 5
  ref = H_element
FEATURE [App::DocumentObjectGroupPython] N_element020  label="N_element : 009"  # scripted group (container) (typed FeaturePython)
  n = 5
  ref = N_element
FEATURE [App::DocumentObjectGroupPython] O_element048  label="O_element : 024"  # scripted group (container) (typed FeaturePython)
  n = 1
  ref = O_element
FEATURE [App::DocumentObjectGroupPython] G4_GUANINE  # scripted group (container) (typed FeaturePython)
  Dunit = g/cm3
  Dvalue = 2.2
  Group = -> [C_element051,H_element044,N_element020,O_element048]
  conduct = 2
  density = 1
  expand = 3
  formula = G4_GUANINE
  name = G4_GUANINE
  specific = 4
FEATURE [App::DocumentObjectGroupPython] Ca_element012  label="Ca_element : 006"  # scripted group (container) (typed FeaturePython)
  n = 1
  ref = Ca_element
FEATURE [App::DocumentObjectGroupPython] S_element014  label="S_element : 005"  # scripted group (container) (typed FeaturePython)
  n = 1
  ref = S_element
FEATURE [App::DocumentObjectGroupPython] O_element049  label="O_element : 6"  # scripted group (container) (typed FeaturePython)
  n = 6
  ref = O_element
FEATURE [App::DocumentObjectGroupPython] H_element045  label="H_element : 024"  # scripted group (container) (typed FeaturePython)
  n = 4
  ref = H_element
FEATURE [App::DocumentObjectGroupPython] G4_GYPSUM  # scripted group (container) (typed FeaturePython)
  Dunit = g/cm3
  Dvalue = 2.32
  Group = -> [Ca_element012,S_element014,O_element049,H_element045]
  conduct = 2
  density = 1
  expand = 3
  formula = G4_GYPSUM
  name = G4_GYPSUM
  specific = 4
FEATURE [App::DocumentObjectGroupPython] C_element052  label="C_element : 7"  # scripted group (container) (typed FeaturePython)
  n = 7
  ref = C_element
FEATURE [App::DocumentObjectGroupPython] H_element046  label="H_element : 16"  # scripted group (container) (typed FeaturePython)
  n = 16
  ref = H_element
FEATURE [App::DocumentObjectGroupPython] G4_N_HEPTANE  label="G4_N-HEPTANE"  # scripted group (container) (typed FeaturePython)
  Dunit = g/cm3
  Dvalue = 0.68376
  Group = -> [C_element052,H_element046]
  conduct = 2
  density = 1
  expand = 3
  formula = G4_N-HEPTANE
  name = G4_N-HEPTANE
  specific = 4
FEATURE [App::DocumentObjectGroupPython] C_element053  label="C_element : 029"  # scripted group (container) (typed FeaturePython)
  n = 6
  ref = C_element
FEATURE [App::DocumentObjectGroupPython] H_element047  label="H_element : 14"  # scripted group (container) (typed FeaturePython)
  n = 14
  ref = H_element
FEATURE [App::DocumentObjectGroupPython] G4_N_HEXANE  label="G4_N-HEXANE"  # scripted group (container) (typed FeaturePython)
  Dunit = g/cm3
  Dvalue = 0.6603
  Group = -> [C_element053,H_element047]
  conduct = 2
  density = 1
  expand = 3
  formula = G4_N-HEXANE
  name = G4_N-HEXANE
  specific = 4
FEATURE [App::DocumentObjectGroupPython] C_element054  label="C_element : 22"  # scripted group (container) (typed FeaturePython)
  n = 22
  ref = C_element
FEATURE [App::DocumentObjectGroupPython] H_element048  label="H_element : 025"  # scripted group (container) (typed FeaturePython)
  n = 10
  ref = H_element
FEATURE [App::DocumentObjectGroupPython] N_element021  label="N_element : 010"  # scripted group (container) (typed FeaturePython)
  n = 2
  ref = N_element
FEATURE [App::DocumentObjectGroupPython] O_element050  label="O_element : 025"  # scripted group (container) (typed FeaturePython)
  n = 5
  ref = O_element
FEATURE [App::DocumentObjectGroupPython] G4_KAPTON  # scripted group (container) (typed FeaturePython)
  Dunit = g/cm3
  Dvalue = 1.42
  Group = -> [C_element054,H_element048,N_element021,O_element050]
  conduct = 2
  density = 1
  expand = 3
  formula = G4_KAPTON
  name = G4_KAPTON
  specific = 4
FEATURE [App::DocumentObjectGroupPython] La_element001  label="La_element : 1"  # scripted group (container) (typed FeaturePython)
  n = 1
  ref = La_element
FEATURE [App::DocumentObjectGroupPython] Br_element003  label="Br_element : 002"  # scripted group (container) (typed FeaturePython)
  n = 1
  ref = Br_element
FEATURE [App::DocumentObjectGroupPython] O_element051  label="O_element : 026"  # scripted group (container) (typed FeaturePython)
  n = 1
  ref = O_element
FEATURE [App::DocumentObjectGroupPython] G4_LANTHANUM_OXYBROMIDE  # scripted group (container) (typed FeaturePython)
  Dunit = g/cm3
  Dvalue = 6.28
  Group = -> [La_element001,Br_element003,O_element051]
  conduct = 2
  density = 1
  expand = 3
  formula = G4_LANTHANUM_OXYBROMIDE
  name = G4_LANTHANUM_OXYBROMIDE
  specific = 4
FEATURE [App::DocumentObjectGroupPython] La_element002  label="La_element : 2"  # scripted group (container) (typed FeaturePython)
  n = 2
  ref = La_element
FEATURE [App::DocumentObjectGroupPython] O_element052  label="O_element : 027"  # scripted group (container) (typed FeaturePython)
  n = 2
  ref = O_element
FEATURE [App::DocumentObjectGroupPython] S_element015  label="S_element : 006"  # scripted group (container) (typed FeaturePython)
  n = 1
  ref = S_element
FEATURE [App::DocumentObjectGroupPython] G4_LANTHANUM_OXYSULFIDE  # scripted group (container) (typed FeaturePython)
  Dunit = g/cm3
  Dvalue = 5.86
  Group = -> [La_element002,O_element052,S_element015]
  conduct = 2
  density = 1
  expand = 3
  formula = G4_LANTHANUM_OXYSULFIDE
  name = G4_LANTHANUM_OXYSULFIDE
  specific = 4
FEATURE [App::DocumentObjectGroupPython] O_element053  label="O_element : 0.072"  # scripted group (container) (typed FeaturePython)
  n = 0.071682
FEATURE [App::DocumentObjectGroupPython] Pb_element002  label="Pb_element : 0.928"  # scripted group (container) (typed FeaturePython)
  n = 0.928318
FEATURE [App::DocumentObjectGroupPython] G4_LEAD_OXIDE  # scripted group (container) (typed FeaturePython)
  Dunit = g/cm3
  Dvalue = 9.53
  Group = -> [O_element053,Pb_element002]
  conduct = 2
  density = 1
  expand = 3
  formula = G4_LEAD_OXIDE
  name = G4_LEAD_OXIDE
  specific = 4
FEATURE [App::DocumentObjectGroupPython] Li_element001  label="Li_element : 1"  # scripted group (container) (typed FeaturePython)
  n = 1
  ref = Li_element
FEATURE [App::DocumentObjectGroupPython] N_element022  label="N_element : 011"  # scripted group (container) (typed FeaturePython)
  n = 1
  ref = N_element
FEATURE [App::DocumentObjectGroupPython] H_element049  label="H_element : 026"  # scripted group (container) (typed FeaturePython)
  n = 2
  ref = H_element
FEATURE [App::DocumentObjectGroupPython] G4_LITHIUM_AMIDE  # scripted group (container) (typed FeaturePython)
  Dunit = g/cm3
  Dvalue = 1.178
  Group = -> [Li_element001,N_element022,H_element049]
  conduct = 2
  density = 1
  expand = 3
  formula = G4_LITHIUM_AMIDE
  name = G4_LITHIUM_AMIDE
  specific = 4
FEATURE [App::DocumentObjectGroupPython] Li_element002  label="Li_element : 2"  # scripted group (container) (typed FeaturePython)
  n = 2
  ref = Li_element
FEATURE [App::DocumentObjectGroupPython] C_element055  label="C_element : 030"  # scripted group (container) (typed FeaturePython)
  n = 1
  ref = C_element
FEATURE [App::DocumentObjectGroupPython] O_element054  label="O_element : 028"  # scripted group (container) (typed FeaturePython)
  n = 3
  ref = O_element
FEATURE [App::DocumentObjectGroupPython] G4_LITHIUM_CARBONATE  # scripted group (container) (typed FeaturePython)
  Dunit = g/cm3
  Dvalue = 2.11
  Group = -> [Li_element002,C_element055,O_element054]
  conduct = 2
  density = 1
  expand = 3
  formula = G4_LITHIUM_CARBONATE
  name = G4_LITHIUM_CARBONATE
  specific = 4
FEATURE [App::DocumentObjectGroupPython] Li_element003  label="Li_element : 003"  # scripted group (container) (typed FeaturePython)
  n = 1
  ref = Li_element
FEATURE [App::DocumentObjectGroupPython] F_element012  label="F_element : 004"  # scripted group (container) (typed FeaturePython)
  n = 1
  ref = F_element
FEATURE [App::DocumentObjectGroupPython] G4_LITHIUM_FLUORIDE  # scripted group (container) (typed FeaturePython)
  Dunit = g/cm3
  Dvalue = 2.635
  Group = -> [Li_element003,F_element012]
  conduct = 2
  density = 1
  expand = 3
  formula = G4_LITHIUM_FLUORIDE
  name = G4_LITHIUM_FLUORIDE
  specific = 4
FEATURE [App::DocumentObjectGroupPython] Li_element004  label="Li_element : 004"  # scripted group (container) (typed FeaturePython)
  n = 1
  ref = Li_element
FEATURE [App::DocumentObjectGroupPython] H_element050  label="H_element : 027"  # scripted group (container) (typed FeaturePython)
  n = 1
  ref = H_element
FEATURE [App::DocumentObjectGroupPython] G4_LITHIUM_HYDRIDE  # scripted group (container) (typed FeaturePython)
  Dunit = g/cm3
  Dvalue = 0.82
  Group = -> [Li_element004,H_element050]
  conduct = 2
  density = 1
  expand = 3
  formula = G4_LITHIUM_HYDRIDE
  name = G4_LITHIUM_HYDRIDE
  specific = 4
FEATURE [App::DocumentObjectGroupPython] Li_element005  label="Li_element : 005"  # scripted group (container) (typed FeaturePython)
  n = 1
  ref = Li_element
FEATURE [App::DocumentObjectGroupPython] I_element003  label="I_element : 002"  # scripted group (container) (typed FeaturePython)
  n = 1
  ref = I_element
FEATURE [App::DocumentObjectGroupPython] G4_LITHIUM_IODIDE  # scripted group (container) (typed FeaturePython)
  Dunit = g/cm3
  Dvalue = 3.494
  Group = -> [Li_element005,I_element003]
  conduct = 2
  density = 1
  expand = 3
  formula = G4_LITHIUM_IODIDE
  name = G4_LITHIUM_IODIDE
  specific = 4
FEATURE [App::DocumentObjectGroupPython] Li_element006  label="Li_element : 006"  # scripted group (container) (typed FeaturePython)
  n = 2
  ref = Li_element
FEATURE [App::DocumentObjectGroupPython] O_element055  label="O_element : 029"  # scripted group (container) (typed FeaturePython)
  n = 1
  ref = O_element
FEATURE [App::DocumentObjectGroupPython] G4_LITHIUM_OXIDE  # scripted group (container) (typed FeaturePython)
  Dunit = g/cm3
  Dvalue = 2.013
  Group = -> [Li_element006,O_element055]
  conduct = 2
  density = 1
  expand = 3
  formula = G4_LITHIUM_OXIDE
  name = G4_LITHIUM_OXIDE
  specific = 4
FEATURE [App::DocumentObjectGroupPython] Li_element007  label="Li_element : 007"  # scripted group (container) (typed FeaturePython)
  n = 2
  ref = Li_element
FEATURE [App::DocumentObjectGroupPython] B_element005  label="B_element : 005"  # scripted group (container) (typed FeaturePython)
  n = 4
  ref = B_element
FEATURE [App::DocumentObjectGroupPython] O_element056  label="O_element : 7"  # scripted group (container) (typed FeaturePython)
  n = 7
  ref = O_element
FEATURE [App::DocumentObjectGroupPython] G4_LITHIUM_TETRABORATE  # scripted group (container) (typed FeaturePython)
  Dunit = g/cm3
  Dvalue = 2.44
  Group = -> [Li_element007,B_element005,O_element056]
  conduct = 2
  density = 1
  expand = 3
  formula = G4_LITHIUM_TETRABORATE
  name = G4_LITHIUM_TETRABORATE
  specific = 4
FEATURE [App::DocumentObjectGroupPython] H_element051  label="H_element : 0.105"  # scripted group (container) (typed FeaturePython)
  n = 0.105
FEATURE [App::DocumentObjectGroupPython] C_element056  label="C_element : 0.083"  # scripted group (container) (typed FeaturePython)
  n = 0.083
FEATURE [App::DocumentObjectGroupPython] N_element023  label="N_element : 0.023"  # scripted group (container) (typed FeaturePython)
  n = 0.023
FEATURE [App::DocumentObjectGroupPython] O_element057  label="O_element : 0.779"  # scripted group (container) (typed FeaturePython)
  n = 0.779
FEATURE [App::DocumentObjectGroupPython] Na_element010  label="Na_element : 0.097"  # scripted group (container) (typed FeaturePython)
  n = 0.002
FEATURE [App::DocumentObjectGroupPython] P_element006  label="P_element : 0.105"  # scripted group (container) (typed FeaturePython)
  n = 0.001
FEATURE [App::DocumentObjectGroupPython] S_element016  label="S_element : 0.017"  # scripted group (container) (typed FeaturePython)
  n = 0.002
FEATURE [App::DocumentObjectGroupPython] Cl_element014  label="Cl_element : 0.587"  # scripted group (container) (typed FeaturePython)
  n = 0.003
FEATURE [App::DocumentObjectGroupPython] K_element005  label="K_element : 0.015"  # scripted group (container) (typed FeaturePython)
  n = 0.002
FEATURE [App::DocumentObjectGroupPython] G4_LUNG_ICRP  # scripted group (container) (typed FeaturePython)
  Dunit = g/cm3
  Dvalue = 1.04
  Group = -> [H_element051,C_element056,N_element023,O_element057,Na_element010,P_element006,S_element016,Cl_element014,K_element005]
  conduct = 2
  density = 1
  expand = 3
  formula = G4_LUNG_ICRP
  name = G4_LUNG_ICRP
  specific = 4
FEATURE [App::DocumentObjectGroupPython] H_element052  label="H_element : 0.116"  # scripted group (container) (typed FeaturePython)
  n = 0.114318
FEATURE [App::DocumentObjectGroupPython] C_element057  label="C_element : 0.656"  # scripted group (container) (typed FeaturePython)
  n = 0.655824
FEATURE [App::DocumentObjectGroupPython] O_element058  label="O_element : 0.092"  # scripted group (container) (typed FeaturePython)
  n = 0.0921831
FEATURE [App::DocumentObjectGroupPython] Mg_element004  label="Mg_element : 0.135"  # scripted group (container) (typed FeaturePython)
  n = 0.134792
FEATURE [App::DocumentObjectGroupPython] Ca_element013  label="Ca_element : 0.003"  # scripted group (container) (typed FeaturePython)
  n = 0.002883
FEATURE [App::DocumentObjectGroupPython] G4_M3_WAX  # scripted group (container) (typed FeaturePython)
  Dunit = g/cm3
  Dvalue = 1.05
  Group = -> [H_element052,C_element057,O_element058,Mg_element004,Ca_element013]
  conduct = 2
  density = 1
  expand = 3
  formula = G4_M3_WAX
  name = G4_M3_WAX
  specific = 4
FEATURE [App::DocumentObjectGroupPython] Mg_element005  label="Mg_element : 1"  # scripted group (container) (typed FeaturePython)
  n = 1
  ref = Mg_element
FEATURE [App::DocumentObjectGroupPython] C_element058  label="C_element : 031"  # scripted group (container) (typed FeaturePython)
  n = 1
  ref = C_element
FEATURE [App::DocumentObjectGroupPython] O_element059  label="O_element : 030"  # scripted group (container) (typed FeaturePython)
  n = 3
  ref = O_element
FEATURE [App::DocumentObjectGroupPython] G4_MAGNESIUM_CARBONATE  # scripted group (container) (typed FeaturePython)
  Dunit = g/cm3
  Dvalue = 2.958
  Group = -> [Mg_element005,C_element058,O_element059]
  conduct = 2
  density = 1
  expand = 3
  formula = G4_MAGNESIUM_CARBONATE
  name = G4_MAGNESIUM_CARBONATE
  specific = 4
FEATURE [App::DocumentObjectGroupPython] Mg_element006  label="Mg_element : 002"  # scripted group (container) (typed FeaturePython)
  n = 1
  ref = Mg_element
FEATURE [App::DocumentObjectGroupPython] F_element013  label="F_element : 005"  # scripted group (container) (typed FeaturePython)
  n = 2
  ref = F_element
FEATURE [App::DocumentObjectGroupPython] G4_MAGNESIUM_FLUORIDE  # scripted group (container) (typed FeaturePython)
  Dunit = g/cm3
  Dvalue = 3
  Group = -> [Mg_element006,F_element013]
  conduct = 2
  density = 1
  expand = 3
  formula = G4_MAGNESIUM_FLUORIDE
  name = G4_MAGNESIUM_FLUORIDE
  specific = 4
FEATURE [App::DocumentObjectGroupPython] Mg_element007  label="Mg_element : 003"  # scripted group (container) (typed FeaturePython)
  n = 1
  ref = Mg_element
FEATURE [App::DocumentObjectGroupPython] O_element060  label="O_element : 031"  # scripted group (container) (typed FeaturePython)
  n = 1
  ref = O_element
FEATURE [App::DocumentObjectGroupPython] G4_MAGNESIUM_OXIDE  # scripted group (container) (typed FeaturePython)
  Dunit = g/cm3
  Dvalue = 3.58
  Group = -> [Mg_element007,O_element060]
  conduct = 2
  density = 1
  expand = 3
  formula = G4_MAGNESIUM_OXIDE
  name = G4_MAGNESIUM_OXIDE
  specific = 4
FEATURE [App::DocumentObjectGroupPython] Mg_element008  label="Mg_element : 004"  # scripted group (container) (typed FeaturePython)
  n = 1
  ref = Mg_element
FEATURE [App::DocumentObjectGroupPython] B_element006  label="B_element : 006"  # scripted group (container) (typed FeaturePython)
  n = 4
  ref = B_element
FEATURE [App::DocumentObjectGroupPython] O_element061  label="O_element : 032"  # scripted group (container) (typed FeaturePython)
  n = 7
  ref = O_element
FEATURE [App::DocumentObjectGroupPython] G4_MAGNESIUM_TETRABORATE  # scripted group (container) (typed FeaturePython)
  Dunit = g/cm3
  Dvalue = 2.53
  Group = -> [Mg_element008,B_element006,O_element061]
  conduct = 2
  density = 1
  expand = 3
  formula = G4_MAGNESIUM_TETRABORATE
  name = G4_MAGNESIUM_TETRABORATE
  specific = 4
FEATURE [App::DocumentObjectGroupPython] Hg_element001  label="Hg_element : 1"  # scripted group (container) (typed FeaturePython)
  n = 1
  ref = Hg_element
FEATURE [App::DocumentObjectGroupPython] I_element004  label="I_element : 2"  # scripted group (container) (typed FeaturePython)
  n = 2
  ref = I_element
FEATURE [App::DocumentObjectGroupPython] G4_MERCURIC_IODIDE  # scripted group (container) (typed FeaturePython)
  Dunit = g/cm3
  Dvalue = 6.36
  Group = -> [Hg_element001,I_element004]
  conduct = 2
  density = 1
  expand = 3
  formula = G4_MERCURIC_IODIDE
  name = G4_MERCURIC_IODIDE
  specific = 4
FEATURE [App::DocumentObjectGroupPython] C_element059  label="C_element : 032"  # scripted group (container) (typed FeaturePython)
  n = 1
  ref = C_element
FEATURE [App::DocumentObjectGroupPython] H_element053  label="H_element : 028"  # scripted group (container) (typed FeaturePython)
  n = 4
  ref = H_element
FEATURE [App::DocumentObjectGroupPython] G4_METHANE  # scripted group (container) (typed FeaturePython)
  Dunit = g/cm3
  Dvalue = 0.000667151
  Group = -> [C_element059,H_element053]
  conduct = 2
  density = 1
  expand = 3
  formula = G4_METHANE
  name = G4_METHANE
  specific = 4
FEATURE [App::DocumentObjectGroupPython] C_element060  label="C_element : 033"  # scripted group (container) (typed FeaturePython)
  n = 1
  ref = C_element
FEATURE [App::DocumentObjectGroupPython] H_element054  label="H_element : 029"  # scripted group (container) (typed FeaturePython)
  n = 4
  ref = H_element
FEATURE [App::DocumentObjectGroupPython] O_element062  label="O_element : 033"  # scripted group (container) (typed FeaturePython)
  n = 1
  ref = O_element
FEATURE [App::DocumentObjectGroupPython] G4_METHANOL  # scripted group (container) (typed FeaturePython)
  Dunit = g/cm3
  Dvalue = 0.7914
  Group = -> [C_element060,H_element054,O_element062]
  conduct = 2
  density = 1
  expand = 3
  formula = G4_METHANOL
  name = G4_METHANOL
  specific = 4
FEATURE [App::DocumentObjectGroupPython] H_element055  label="H_element : 0.134"  # scripted group (container) (typed FeaturePython)
  n = 0.13404
FEATURE [App::DocumentObjectGroupPython] C_element061  label="C_element : 0.778"  # scripted group (container) (typed FeaturePython)
  n = 0.77796
FEATURE [App::DocumentObjectGroupPython] O_element063  label="O_element : 0.035"  # scripted group (container) (typed FeaturePython)
  n = 0.03502
FEATURE [App::DocumentObjectGroupPython] Mg_element009  label="Mg_element : 0.039"  # scripted group (container) (typed FeaturePython)
  n = 0.038594
FEATURE [App::DocumentObjectGroupPython] Ti_element002  label="Ti_element : 0.014"  # scripted group (container) (typed FeaturePython)
  n = 0.014386
FEATURE [App::DocumentObjectGroupPython] G4_MIX_D_WAX  # scripted group (container) (typed FeaturePython)
  Dunit = g/cm3
  Dvalue = 0.99
  Group = -> [H_element055,C_element061,O_element063,Mg_element009,Ti_element002]
  conduct = 2
  density = 1
  expand = 3
  formula = G4_MIX_D_WAX
  name = G4_MIX_D_WAX
  specific = 4
FEATURE [App::DocumentObjectGroupPython] H_element056  label="H_element : 0.135"  # scripted group (container) (typed FeaturePython)
  n = 0.081192
FEATURE [App::DocumentObjectGroupPython] C_element062  label="C_element : 0.583"  # scripted group (container) (typed FeaturePython)
  n = 0.583442
FEATURE [App::DocumentObjectGroupPython] N_element024  label="N_element : 0.018"  # scripted group (container) (typed FeaturePython)
  n = 0.017798
FEATURE [App::DocumentObjectGroupPython] O_element064  label="O_element : 0.186"  # scripted group (container) (typed FeaturePython)
  n = 0.186381
FEATURE [App::DocumentObjectGroupPython] Mg_element010  label="Mg_element : 0.130"  # scripted group (container) (typed FeaturePython)
  n = 0.130287
FEATURE [App::DocumentObjectGroupPython] Cl_element015  label="Cl_element : 0.588"  # scripted group (container) (typed FeaturePython)
  n = 0.0009
FEATURE [App::DocumentObjectGroupPython] G4_MS20_TISSUE  # scripted group (container) (typed FeaturePython)
  Dunit = g/cm3
  Dvalue = 1
  Group = -> [H_element056,C_element062,N_element024,O_element064,Mg_element010,Cl_element015]
  conduct = 2
  density = 1
  expand = 3
  formula = G4_MS20_TISSUE
  name = G4_MS20_TISSUE
  specific = 4
FEATURE [App::DocumentObjectGroupPython] H_element057  label="H_element : 0.136"  # scripted group (container) (typed FeaturePython)
  n = 0.102
FEATURE [App::DocumentObjectGroupPython] C_element063  label="C_element : 0.143"  # scripted group (container) (typed FeaturePython)
  n = 0.143
FEATURE [App::DocumentObjectGroupPython] N_element025  label="N_element : 0.034"  # scripted group (container) (typed FeaturePython)
  n = 0.034
FEATURE [App::DocumentObjectGroupPython] O_element065  label="O_element : 0.710"  # scripted group (container) (typed FeaturePython)
  n = 0.71
FEATURE [App::DocumentObjectGroupPython] Na_element011  label="Na_element : 0.098"  # scripted group (container) (typed FeaturePython)
  n = 0.001
FEATURE [App::DocumentObjectGroupPython] P_element007  label="P_element : 0.002"  # scripted group (container) (typed FeaturePython)
  n = 0.002
FEATURE [App::DocumentObjectGroupPython] S_element017  label="S_element : 0.018"  # scripted group (container) (typed FeaturePython)
  n = 0.003
FEATURE [App::DocumentObjectGroupPython] Cl_element016  label="Cl_element : 0.589"  # scripted group (container) (typed FeaturePython)
  n = 0.001
FEATURE [App::DocumentObjectGroupPython] K_element006  label="K_element : 0.004"  # scripted group (container) (typed FeaturePython)
  n = 0.004
FEATURE [App::DocumentObjectGroupPython] G4_MUSCLE_SKELETAL_ICRP  # scripted group (container) (typed FeaturePython)
  Dunit = g/cm3
  Dvalue = 1.05
  Group = -> [H_element057,C_element063,N_element025,O_element065,Na_element011,P_element007,S_element017,Cl_element016,K_element006]
  conduct = 2
  density = 1
  expand = 3
  formula = G4_MUSCLE_SKELETAL_ICRP
  name = G4_MUSCLE_SKELETAL_ICRP
  specific = 4
FEATURE [App::DocumentObjectGroupPython] H_element058  label="H_element : 0.137"  # scripted group (container) (typed FeaturePython)
  n = 0.102102
FEATURE [App::DocumentObjectGroupPython] C_element064  label="C_element : 0.123"  # scripted group (container) (typed FeaturePython)
  n = 0.123123
FEATURE [App::DocumentObjectGroupPython] N_element026  label="N_element : 0.756"  # scripted group (container) (typed FeaturePython)
  n = 0.035035
FEATURE [App::DocumentObjectGroupPython] O_element066  label="O_element : 0.730"  # scripted group (container) (typed FeaturePython)
  n = 0.72973
FEATURE [App::DocumentObjectGroupPython] Na_element012  label="Na_element : 0.099"  # scripted group (container) (typed FeaturePython)
  n = 0.001001
FEATURE [App::DocumentObjectGroupPython] P_element008  label="P_element : 0.106"  # scripted group (container) (typed FeaturePython)
  n = 0.002002
FEATURE [App::DocumentObjectGroupPython] S_element018  label="S_element : 0.019"  # scripted group (container) (typed FeaturePython)
  n = 0.004004
FEATURE [App::DocumentObjectGroupPython] K_element007  label="K_element : 0.016"  # scripted group (container) (typed FeaturePython)
  n = 0.003003
FEATURE [App::DocumentObjectGroupPython] G4_MUSCLE_STRIATED_ICRU  # scripted group (container) (typed FeaturePython)
  Dunit = g/cm3
  Dvalue = 1.04
  Group = -> [H_element058,C_element064,N_element026,O_element066,Na_element012,P_element008,S_element018,K_element007]
  conduct = 2
  density = 1
  expand = 3
  formula = G4_MUSCLE_STRIATED_ICRU
  name = G4_MUSCLE_STRIATED_ICRU
  specific = 4
FEATURE [App::DocumentObjectGroupPython] H_element059  label="H_element : 0.098"  # scripted group (container) (typed FeaturePython)
  n = 0.0982341
FEATURE [App::DocumentObjectGroupPython] C_element065  label="C_element : 0.156"  # scripted group (container) (typed FeaturePython)
  n = 0.156214
FEATURE [App::DocumentObjectGroupPython] N_element027  label="N_element : 0.757"  # scripted group (container) (typed FeaturePython)
  n = 0.035451
FEATURE [App::DocumentObjectGroupPython] O_element067  label="O_element : 0.880"  # scripted group (container) (typed FeaturePython)
  n = 0.710101
FEATURE [App::DocumentObjectGroupPython] G4_MUSCLE_WITH_SUCROSE  # scripted group (container) (typed FeaturePython)
  Dunit = g/cm3
  Dvalue = 1.11
  Group = -> [H_element059,C_element065,N_element027,O_element067]
  conduct = 2
  density = 1
  expand = 3
  formula = G4_MUSCLE_WITH_SUCROSE
  name = G4_MUSCLE_WITH_SUCROSE
  specific = 4
FEATURE [App::DocumentObjectGroupPython] H_element060  label="H_element : 0.138"  # scripted group (container) (typed FeaturePython)
  n = 0.101969
FEATURE [App::DocumentObjectGroupPython] C_element066  label="C_element : 0.120"  # scripted group (container) (typed FeaturePython)
  n = 0.120058
FEATURE [App::DocumentObjectGroupPython] N_element028  label="N_element : 0.758"  # scripted group (container) (typed FeaturePython)
  n = 0.035451
FEATURE [App::DocumentObjectGroupPython] O_element068  label="O_element : 0.743"  # scripted group (container) (typed FeaturePython)
  n = 0.742522
FEATURE [App::DocumentObjectGroupPython] G4_MUSCLE_WITHOUT_SUCROSE  # scripted group (container) (typed FeaturePython)
  Dunit = g/cm3
  Dvalue = 1.07
  Group = -> [H_element060,C_element066,N_element028,O_element068]
  conduct = 2
  density = 1
  expand = 3
  formula = G4_MUSCLE_WITHOUT_SUCROSE
  name = G4_MUSCLE_WITHOUT_SUCROSE
  specific = 4
FEATURE [App::DocumentObjectGroupPython] C_element067  label="C_element : 10"  # scripted group (container) (typed FeaturePython)
  n = 10
  ref = C_element
FEATURE [App::DocumentObjectGroupPython] H_element061  label="H_element : 030"  # scripted group (container) (typed FeaturePython)
  n = 8
  ref = H_element
FEATURE [App::DocumentObjectGroupPython] G4_NAPHTHALENE  # scripted group (container) (typed FeaturePython)
  Dunit = g/cm3
  Dvalue = 1.145
  Group = -> [C_element067,H_element061]
  conduct = 2
  density = 1
  expand = 3
  formula = G4_NAPHTHALENE
  name = G4_NAPHTHALENE
  specific = 4
FEATURE [App::DocumentObjectGroupPython] C_element068  label="C_element : 034"  # scripted group (container) (typed FeaturePython)
  n = 6
  ref = C_element
FEATURE [App::DocumentObjectGroupPython] H_element062  label="H_element : 031"  # scripted group (container) (typed FeaturePython)
  n = 5
  ref = H_element
FEATURE [App::DocumentObjectGroupPython] N_element029  label="N_element : 012"  # scripted group (container) (typed FeaturePython)
  n = 1
  ref = N_element
FEATURE [App::DocumentObjectGroupPython] O_element069  label="O_element : 034"  # scripted group (container) (typed FeaturePython)
  n = 2
  ref = O_element
FEATURE [App::DocumentObjectGroupPython] G4_NITROBENZENE  # scripted group (container) (typed FeaturePython)
  Dunit = g/cm3
  Dvalue = 1.19867
  Group = -> [C_element068,H_element062,N_element029,O_element069]
  conduct = 2
  density = 1
  expand = 3
  formula = G4_NITROBENZENE
  name = G4_NITROBENZENE
  specific = 4
FEATURE [App::DocumentObjectGroupPython] N_element030  label="N_element : 013"  # scripted group (container) (typed FeaturePython)
  n = 2
  ref = N_element
FEATURE [App::DocumentObjectGroupPython] O_element070  label="O_element : 035"  # scripted group (container) (typed FeaturePython)
  n = 1
  ref = O_element
FEATURE [App::DocumentObjectGroupPython] G4_NITROUS_OXIDE  # scripted group (container) (typed FeaturePython)
  Dunit = g/cm3
  Dvalue = 0.00183094
  Group = -> [N_element030,O_element070]
  conduct = 2
  density = 1
  expand = 3
  formula = G4_NITROUS_OXIDE
  name = G4_NITROUS_OXIDE
  specific = 4
FEATURE [App::DocumentObjectGroupPython] H_element063  label="H_element : 0.104"  # scripted group (container) (typed FeaturePython)
  n = 0.103509
FEATURE [App::DocumentObjectGroupPython] C_element069  label="C_element : 0.648"  # scripted group (container) (typed FeaturePython)
  n = 0.648416
FEATURE [App::DocumentObjectGroupPython] N_element031  label="N_element : 0.100"  # scripted group (container) (typed FeaturePython)
  n = 0.0995361
FEATURE [App::DocumentObjectGroupPython] O_element071  label="O_element : 0.149"  # scripted group (container) (typed FeaturePython)
  n = 0.148539
FEATURE [App::DocumentObjectGroupPython] G4_NYLON_8062  label="G4_NYLON-8062"  # scripted group (container) (typed FeaturePython)
  Dunit = g/cm3
  Dvalue = 1.08
  Group = -> [H_element063,C_element069,N_element031,O_element071]
  conduct = 2
  density = 1
  expand = 3
  formula = G4_NYLON-8062
  name = G4_NYLON-8062
  specific = 4
FEATURE [App::DocumentObjectGroupPython] C_element070  label="C_element : 035"  # scripted group (container) (typed FeaturePython)
  n = 6
  ref = C_element
FEATURE [App::DocumentObjectGroupPython] H_element064  label="H_element : 11"  # scripted group (container) (typed FeaturePython)
  n = 11
  ref = H_element
FEATURE [App::DocumentObjectGroupPython] N_element032  label="N_element : 014"  # scripted group (container) (typed FeaturePython)
  n = 1
  ref = N_element
FEATURE [App::DocumentObjectGroupPython] O_element072  label="O_element : 036"  # scripted group (container) (typed FeaturePython)
  n = 1
  ref = O_element
FEATURE [App::DocumentObjectGroupPython] G4_NYLON_6_6  label="G4_NYLON-6-6"  # scripted group (container) (typed FeaturePython)
  Dunit = g/cm3
  Dvalue = 1.14
  Group = -> [C_element070,H_element064,N_element032,O_element072]
  conduct = 2
  density = 1
  expand = 3
  formula = G4_NYLON-6-6
  name = G4_NYLON-6-6
  specific = 4
FEATURE [App::DocumentObjectGroupPython] H_element065  label="H_element : 0.139"  # scripted group (container) (typed FeaturePython)
  n = 0.107062
FEATURE [App::DocumentObjectGroupPython] C_element071  label="C_element : 0.680"  # scripted group (container) (typed FeaturePython)
  n = 0.680449
FEATURE [App::DocumentObjectGroupPython] N_element033  label="N_element : 0.099"  # scripted group (container) (typed FeaturePython)
  n = 0.099189
FEATURE [App::DocumentObjectGroupPython] O_element073  label="O_element : 0.113"  # scripted group (container) (typed FeaturePython)
  n = 0.1133
FEATURE [App::DocumentObjectGroupPython] G4_NYLON_6_10  label="G4_NYLON-6-10"  # scripted group (container) (typed FeaturePython)
  Dunit = g/cm3
  Dvalue = 1.14
  Group = -> [H_element065,C_element071,N_element033,O_element073]
  conduct = 2
  density = 1
  expand = 3
  formula = G4_NYLON-6-10
  name = G4_NYLON-6-10
  specific = 4
FEATURE [App::DocumentObjectGroupPython] H_element066  label="H_element : 0.140"  # scripted group (container) (typed FeaturePython)
  n = 0.115476
FEATURE [App::DocumentObjectGroupPython] C_element072  label="C_element : 0.721"  # scripted group (container) (typed FeaturePython)
  n = 0.720818
FEATURE [App::DocumentObjectGroupPython] N_element034  label="N_element : 0.076"  # scripted group (container) (typed FeaturePython)
  n = 0.0764169
FEATURE [App::DocumentObjectGroupPython] O_element074  label="O_element : 0.087"  # scripted group (container) (typed FeaturePython)
  n = 0.0872889
FEATURE [App::DocumentObjectGroupPython] G4_NYLON_11_RILSAN  label="G4_NYLON-11_RILSAN"  # scripted group (container) (typed FeaturePython)
  Dunit = g/cm3
  Dvalue = 1.425
  Group = -> [H_element066,C_element072,N_element034,O_element074]
  conduct = 2
  density = 1
  expand = 3
  formula = G4_NYLON-11_RILSAN
  name = G4_NYLON-11_RILSAN
  specific = 4
FEATURE [App::DocumentObjectGroupPython] C_element073  label="C_element : 8"  # scripted group (container) (typed FeaturePython)
  n = 8
  ref = C_element
FEATURE [App::DocumentObjectGroupPython] H_element067  label="H_element : 18"  # scripted group (container) (typed FeaturePython)
  n = 18
  ref = H_element
FEATURE [App::DocumentObjectGroupPython] G4_OCTANE  # scripted group (container) (typed FeaturePython)
  Dunit = g/cm3
  Dvalue = 0.7026
  Group = -> [C_element073,H_element067]
  conduct = 2
  density = 1
  expand = 3
  formula = G4_OCTANE
  name = G4_OCTANE
  specific = 4
FEATURE [App::DocumentObjectGroupPython] C_element074  label="C_element : 25"  # scripted group (container) (typed FeaturePython)
  n = 25
  ref = C_element
FEATURE [App::DocumentObjectGroupPython] H_element068  label="H_element : 52"  # scripted group (container) (typed FeaturePython)
  n = 52
  ref = H_element
FEATURE [App::DocumentObjectGroupPython] G4_PARAFFIN  # scripted group (container) (typed FeaturePython)
  Dunit = g/cm3
  Dvalue = 0.93
  Group = -> [C_element074,H_element068]
  conduct = 2
  density = 1
  expand = 3
  formula = G4_PARAFFIN
  name = G4_PARAFFIN
  specific = 4
FEATURE [App::DocumentObjectGroupPython] C_element075  label="C_element : 036"  # scripted group (container) (typed FeaturePython)
  n = 5
  ref = C_element
FEATURE [App::DocumentObjectGroupPython] H_element069  label="H_element : 032"  # scripted group (container) (typed FeaturePython)
  n = 12
  ref = H_element
FEATURE [App::DocumentObjectGroupPython] G4_N_PENTANE  label="G4_N-PENTANE"  # scripted group (container) (typed FeaturePython)
  Dunit = g/cm3
  Dvalue = 0.6262
  Group = -> [C_element075,H_element069]
  conduct = 2
  density = 1
  expand = 3
  formula = G4_N-PENTANE
  name = G4_N-PENTANE
  specific = 4
FEATURE [App::DocumentObjectGroupPython] H_element070  label="H_element : 0.014"  # scripted group (container) (typed FeaturePython)
  n = 0.0141
FEATURE [App::DocumentObjectGroupPython] C_element076  label="C_element : 0.072"  # scripted group (container) (typed FeaturePython)
  n = 0.072261
FEATURE [App::DocumentObjectGroupPython] N_element035  label="N_element : 0.019"  # scripted group (container) (typed FeaturePython)
  n = 0.01932
FEATURE [App::DocumentObjectGroupPython] O_element075  label="O_element : 0.066"  # scripted group (container) (typed FeaturePython)
  n = 0.066101
FEATURE [App::DocumentObjectGroupPython] S_element019  label="S_element : 0.020"  # scripted group (container) (typed FeaturePython)
  n = 0.00189
FEATURE [App::DocumentObjectGroupPython] Br_element004  label="Br_element : 0.349"  # scripted group (container) (typed FeaturePython)
  n = 0.349103
FEATURE [App::DocumentObjectGroupPython] Ag_element001  label="Ag_element : 0.474"  # scripted group (container) (typed FeaturePython)
  n = 0.474105
FEATURE [App::DocumentObjectGroupPython] I_element005  label="I_element : 0.003"  # scripted group (container) (typed FeaturePython)
  n = 0.00312
FEATURE [App::DocumentObjectGroupPython] G4_PHOTO_EMULSION  # scripted group (container) (typed FeaturePython)
  Dunit = g/cm3
  Dvalue = 3.815
  Group = -> [H_element070,C_element076,N_element035,O_element075,S_element019,Br_element004,Ag_element001,I_element005]
  conduct = 2
  density = 1
  expand = 3
  formula = G4_PHOTO_EMULSION
  name = G4_PHOTO_EMULSION
  specific = 4
FEATURE [App::DocumentObjectGroupPython] C_element077  label="C_element : 9"  # scripted group (container) (typed FeaturePython)
  n = 9
  ref = C_element
FEATURE [App::DocumentObjectGroupPython] H_element071  label="H_element : 033"  # scripted group (container) (typed FeaturePython)
  n = 10
  ref = H_element
FEATURE [App::DocumentObjectGroupPython] G4_PLASTIC_SC_VINYLTOLUENE  # scripted group (container) (typed FeaturePython)
  Dunit = g/cm3
  Dvalue = 1.032
  Group = -> [C_element077,H_element071]
  conduct = 2
  density = 1
  expand = 3
  formula = G4_PLASTIC_SC_VINYLTOLUENE
  name = G4_PLASTIC_SC_VINYLTOLUENE
  specific = 4
FEATURE [App::DocumentObjectGroupPython] Pu_element001  label="Pu_element : 1"  # scripted group (container) (typed FeaturePython)
  n = 1
  ref = Pu_element
FEATURE [App::DocumentObjectGroupPython] O_element076  label="O_element : 037"  # scripted group (container) (typed FeaturePython)
  n = 2
  ref = O_element
FEATURE [App::DocumentObjectGroupPython] G4_PLUTONIUM_DIOXIDE  # scripted group (container) (typed FeaturePython)
  Dunit = g/cm3
  Dvalue = 11.46
  Group = -> [Pu_element001,O_element076]
  conduct = 2
  density = 1
  expand = 3
  formula = G4_PLUTONIUM_DIOXIDE
  name = G4_PLUTONIUM_DIOXIDE
  specific = 4
FEATURE [App::DocumentObjectGroupPython] C_element078  label="C_element : 037"  # scripted group (container) (typed FeaturePython)
  n = 3
  ref = C_element
FEATURE [App::DocumentObjectGroupPython] H_element072  label="H_element : 034"  # scripted group (container) (typed FeaturePython)
  n = 3
  ref = H_element
FEATURE [App::DocumentObjectGroupPython] N_element036  label="N_element : 015"  # scripted group (container) (typed FeaturePython)
  n = 1
  ref = N_element
FEATURE [App::DocumentObjectGroupPython] G4_POLYACRYLONITRILE  # scripted group (container) (typed FeaturePython)
  Dunit = g/cm3
  Dvalue = 1.17
  Group = -> [C_element078,H_element072,N_element036]
  conduct = 2
  density = 1
  expand = 3
  formula = G4_POLYACRYLONITRILE
  name = G4_POLYACRYLONITRILE
  specific = 4
FEATURE [App::DocumentObjectGroupPython] C_element079  label="C_element : 16"  # scripted group (container) (typed FeaturePython)
  n = 16
  ref = C_element
FEATURE [App::DocumentObjectGroupPython] H_element073  label="H_element : 035"  # scripted group (container) (typed FeaturePython)
  n = 14
  ref = H_element
FEATURE [App::DocumentObjectGroupPython] O_element077  label="O_element : 038"  # scripted group (container) (typed FeaturePython)
  n = 3
  ref = O_element
FEATURE [App::DocumentObjectGroupPython] G4_POLYCARBONATE  # scripted group (container) (typed FeaturePython)
  Dunit = g/cm3
  Dvalue = 1.2
  Group = -> [C_element079,H_element073,O_element077]
  conduct = 2
  density = 1
  expand = 3
  formula = G4_POLYCARBONATE
  name = G4_POLYCARBONATE
  specific = 4
FEATURE [App::DocumentObjectGroupPython] C_element080  label="C_element : 038"  # scripted group (container) (typed FeaturePython)
  n = 8
  ref = C_element
FEATURE [App::DocumentObjectGroupPython] H_element074  label="H_element : 036"  # scripted group (container) (typed FeaturePython)
  n = 7
  ref = H_element
FEATURE [App::DocumentObjectGroupPython] Cl_element017  label="Cl_element : 007"  # scripted group (container) (typed FeaturePython)
  n = 1
  ref = Cl_element
FEATURE [App::DocumentObjectGroupPython] G4_POLYCHLOROSTYRENE  # scripted group (container) (typed FeaturePython)
  Dunit = g/cm3
  Dvalue = 1.3
  Group = -> [C_element080,H_element074,Cl_element017]
  conduct = 2
  density = 1
  expand = 3
  formula = G4_POLYCHLOROSTYRENE
  name = G4_POLYCHLOROSTYRENE
  specific = 4
FEATURE [App::DocumentObjectGroupPython] C_element081  label="C_element : 039"  # scripted group (container) (typed FeaturePython)
  n = 1
  ref = C_element
FEATURE [App::DocumentObjectGroupPython] H_element075  label="H_element : 037"  # scripted group (container) (typed FeaturePython)
  n = 2
  ref = H_element
FEATURE [App::DocumentObjectGroupPython] G4_POLYETHYLENE  # scripted group (container) (typed FeaturePython)
  Dunit = g/cm3
  Dvalue = 0.94
  Group = -> [C_element081,H_element075]
  conduct = 2
  density = 1
  expand = 3
  formula = G4_POLYETHYLENE
  name = G4_POLYETHYLENE
  specific = 4
FEATURE [App::DocumentObjectGroupPython] C_element082  label="C_element : 040"  # scripted group (container) (typed FeaturePython)
  n = 10
  ref = C_element
FEATURE [App::DocumentObjectGroupPython] H_element076  label="H_element : 038"  # scripted group (container) (typed FeaturePython)
  n = 8
  ref = H_element
FEATURE [App::DocumentObjectGroupPython] O_element078  label="O_element : 039"  # scripted group (container) (typed FeaturePython)
  n = 4
  ref = O_element
FEATURE [App::DocumentObjectGroupPython] G4_MYLAR  # scripted group (container) (typed FeaturePython)
  Dunit = g/cm3
  Dvalue = 1.4
  Group = -> [C_element082,H_element076,O_element078]
  conduct = 2
  density = 1
  expand = 3
  formula = G4_MYLAR
  name = G4_MYLAR
  specific = 4
FEATURE [App::DocumentObjectGroupPython] C_element083  label="C_element : 041"  # scripted group (container) (typed FeaturePython)
  n = 5
  ref = C_element
FEATURE [App::DocumentObjectGroupPython] H_element077  label="H_element : 039"  # scripted group (container) (typed FeaturePython)
  n = 8
  ref = H_element
FEATURE [App::DocumentObjectGroupPython] O_element079  label="O_element : 040"  # scripted group (container) (typed FeaturePython)
  n = 2
  ref = O_element
FEATURE [App::DocumentObjectGroupPython] G4_PLEXIGLASS  # scripted group (container) (typed FeaturePython)
  Dunit = g/cm3
  Dvalue = 1.19
  Group = -> [C_element083,H_element077,O_element079]
  conduct = 2
  density = 1
  expand = 3
  formula = G4_PLEXIGLASS
  name = G4_PLEXIGLASS
  specific = 4
FEATURE [App::DocumentObjectGroupPython] C_element084  label="C_element : 042"  # scripted group (container) (typed FeaturePython)
  n = 1
  ref = C_element
FEATURE [App::DocumentObjectGroupPython] H_element078  label="H_element : 040"  # scripted group (container) (typed FeaturePython)
  n = 2
  ref = H_element
FEATURE [App::DocumentObjectGroupPython] O_element080  label="O_element : 041"  # scripted group (container) (typed FeaturePython)
  n = 1
  ref = O_element
FEATURE [App::DocumentObjectGroupPython] G4_POLYOXYMETHYLENE  # scripted group (container) (typed FeaturePython)
  Dunit = g/cm3
  Dvalue = 1.425
  Group = -> [C_element084,H_element078,O_element080]
  conduct = 2
  density = 1
  expand = 3
  formula = G4_POLYOXYMETHYLENE
  name = G4_POLYOXYMETHYLENE
  specific = 4
FEATURE [App::DocumentObjectGroupPython] C_element085  label="C_element : 043"  # scripted group (container) (typed FeaturePython)
  n = 2
  ref = C_element
FEATURE [App::DocumentObjectGroupPython] H_element079  label="H_element : 041"  # scripted group (container) (typed FeaturePython)
  n = 4
  ref = H_element
FEATURE [App::DocumentObjectGroupPython] G4_POLYPROPYLENE  # scripted group (container) (typed FeaturePython)
  Dunit = g/cm3
  Dvalue = 0.9
  Group = -> [C_element085,H_element079]
  conduct = 2
  density = 1
  expand = 3
  formula = G4_POLYPROPYLENE
  name = G4_POLYPROPYLENE
  specific = 4
FEATURE [App::DocumentObjectGroupPython] C_element086  label="C_element : 044"  # scripted group (container) (typed FeaturePython)
  n = 8
  ref = C_element
FEATURE [App::DocumentObjectGroupPython] H_element080  label="H_element : 042"  # scripted group (container) (typed FeaturePython)
  n = 8
  ref = H_element
FEATURE [App::DocumentObjectGroupPython] G4_POLYSTYRENE  # scripted group (container) (typed FeaturePython)
  Dunit = g/cm3
  Dvalue = 1.06
  Group = -> [C_element086,H_element080]
  conduct = 2
  density = 1
  expand = 3
  formula = G4_POLYSTYRENE
  name = G4_POLYSTYRENE
  specific = 4
FEATURE [App::DocumentObjectGroupPython] C_element087  label="C_element : 045"  # scripted group (container) (typed FeaturePython)
  n = 2
  ref = C_element
FEATURE [App::DocumentObjectGroupPython] F_element014  label="F_element : 4"  # scripted group (container) (typed FeaturePython)
  n = 4
  ref = F_element
FEATURE [App::DocumentObjectGroupPython] G4_TEFLON  # scripted group (container) (typed FeaturePython)
  Dunit = g/cm3
  Dvalue = 2.2
  Group = -> [C_element087,F_element014]
  conduct = 2
  density = 1
  expand = 3
  formula = G4_TEFLON
  name = G4_TEFLON
  specific = 4
FEATURE [App::DocumentObjectGroupPython] C_element088  label="C_element : 046"  # scripted group (container) (typed FeaturePython)
  n = 2
  ref = C_element
FEATURE [App::DocumentObjectGroupPython] F_element015  label="F_element : 006"  # scripted group (container) (typed FeaturePython)
  n = 3
  ref = F_element
FEATURE [App::DocumentObjectGroupPython] Cl_element018  label="Cl_element : 008"  # scripted group (container) (typed FeaturePython)
  n = 1
  ref = Cl_element
FEATURE [App::DocumentObjectGroupPython] G4_POLYTRIFLUOROCHLOROETHYLENE  # scripted group (container) (typed FeaturePython)
  Dunit = g/cm3
  Dvalue = 2.1
  Group = -> [C_element088,F_element015,Cl_element018]
  conduct = 2
  density = 1
  expand = 3
  formula = G4_POLYTRIFLUOROCHLOROETHYLENE
  name = G4_POLYTRIFLUOROCHLOROETHYLENE
  specific = 4
FEATURE [App::DocumentObjectGroupPython] C_element089  label="C_element : 047"  # scripted group (container) (typed FeaturePython)
  n = 4
  ref = C_element
FEATURE [App::DocumentObjectGroupPython] H_element081  label="H_element : 043"  # scripted group (container) (typed FeaturePython)
  n = 6
  ref = H_element
FEATURE [App::DocumentObjectGroupPython] O_element081  label="O_element : 042"  # scripted group (container) (typed FeaturePython)
  n = 2
  ref = O_element
FEATURE [App::DocumentObjectGroupPython] G4_POLYVINYL_ACETATE  # scripted group (container) (typed FeaturePython)
  Dunit = g/cm3
  Dvalue = 1.19
  Group = -> [C_element089,H_element081,O_element081]
  conduct = 2
  density = 1
  expand = 3
  formula = G4_POLYVINYL_ACETATE
  name = G4_POLYVINYL_ACETATE
  specific = 4
FEATURE [App::DocumentObjectGroupPython] C_element090  label="C_element : 048"  # scripted group (container) (typed FeaturePython)
  n = 2
  ref = C_element
FEATURE [App::DocumentObjectGroupPython] H_element082  label="H_element : 044"  # scripted group (container) (typed FeaturePython)
  n = 4
  ref = H_element
FEATURE [App::DocumentObjectGroupPython] O_element082  label="O_element : 043"  # scripted group (container) (typed FeaturePython)
  n = 1
  ref = O_element
FEATURE [App::DocumentObjectGroupPython] G4_POLYVINYL_ALCOHOL  # scripted group (container) (typed FeaturePython)
  Dunit = g/cm3
  Dvalue = 1.3
  Group = -> [C_element090,H_element082,O_element082]
  conduct = 2
  density = 1
  expand = 3
  formula = G4_POLYVINYL_ALCOHOL
  name = G4_POLYVINYL_ALCOHOL
  specific = 4
FEATURE [App::DocumentObjectGroupPython] C_element091  label="C_element : 049"  # scripted group (container) (typed FeaturePython)
  n = 8
  ref = C_element
FEATURE [App::DocumentObjectGroupPython] H_element083  label="H_element : 045"  # scripted group (container) (typed FeaturePython)
  n = 14
  ref = H_element
FEATURE [App::DocumentObjectGroupPython] O_element083  label="O_element : 044"  # scripted group (container) (typed FeaturePython)
  n = 2
  ref = O_element
FEATURE [App::DocumentObjectGroupPython] G4_POLYVINYL_BUTYRAL  # scripted group (container) (typed FeaturePython)
  Dunit = g/cm3
  Dvalue = 1.12
  Group = -> [C_element091,H_element083,O_element083]
  conduct = 2
  density = 1
  expand = 3
  formula = G4_POLYVINYL_BUTYRAL
  name = G4_POLYVINYL_BUTYRAL
  specific = 4
FEATURE [App::DocumentObjectGroupPython] C_element092  label="C_element : 050"  # scripted group (container) (typed FeaturePython)
  n = 2
  ref = C_element
FEATURE [App::DocumentObjectGroupPython] H_element084  label="H_element : 046"  # scripted group (container) (typed FeaturePython)
  n = 3
  ref = H_element
FEATURE [App::DocumentObjectGroupPython] Cl_element019  label="Cl_element : 009"  # scripted group (container) (typed FeaturePython)
  n = 1
  ref = Cl_element
FEATURE [App::DocumentObjectGroupPython] G4_POLYVINYL_CHLORIDE  # scripted group (container) (typed FeaturePython)
  Dunit = g/cm3
  Dvalue = 1.3
  Group = -> [C_element092,H_element084,Cl_element019]
  conduct = 2
  density = 1
  expand = 3
  formula = G4_POLYVINYL_CHLORIDE
  name = G4_POLYVINYL_CHLORIDE
  specific = 4
FEATURE [App::DocumentObjectGroupPython] C_element093  label="C_element : 051"  # scripted group (container) (typed FeaturePython)
  n = 2
  ref = C_element
FEATURE [App::DocumentObjectGroupPython] H_element085  label="H_element : 047"  # scripted group (container) (typed FeaturePython)
  n = 2
  ref = H_element
FEATURE [App::DocumentObjectGroupPython] Cl_element020  label="Cl_element : 010"  # scripted group (container) (typed FeaturePython)
  n = 2
  ref = Cl_element
FEATURE [App::DocumentObjectGroupPython] G4_POLYVINYLIDENE_CHLORIDE  # scripted group (container) (typed FeaturePython)
  Dunit = g/cm3
  Dvalue = 1.7
  Group = -> [C_element093,H_element085,Cl_element020]
  conduct = 2
  density = 1
  expand = 3
  formula = G4_POLYVINYLIDENE_CHLORIDE
  name = G4_POLYVINYLIDENE_CHLORIDE
  specific = 4
FEATURE [App::DocumentObjectGroupPython] C_element094  label="C_element : 052"  # scripted group (container) (typed FeaturePython)
  n = 2
  ref = C_element
FEATURE [App::DocumentObjectGroupPython] H_element086  label="H_element : 048"  # scripted group (container) (typed FeaturePython)
  n = 2
  ref = H_element
FEATURE [App::DocumentObjectGroupPython] F_element016  label="F_element : 007"  # scripted group (container) (typed FeaturePython)
  n = 2
  ref = F_element
FEATURE [App::DocumentObjectGroupPython] G4_POLYVINYLIDENE_FLUORIDE  # scripted group (container) (typed FeaturePython)
  Dunit = g/cm3
  Dvalue = 1.76
  Group = -> [C_element094,H_element086,F_element016]
  conduct = 2
  density = 1
  expand = 3
  formula = G4_POLYVINYLIDENE_FLUORIDE
  name = G4_POLYVINYLIDENE_FLUORIDE
  specific = 4
FEATURE [App::DocumentObjectGroupPython] C_element095  label="C_element : 053"  # scripted group (container) (typed FeaturePython)
  n = 6
  ref = C_element
FEATURE [App::DocumentObjectGroupPython] H_element087  label="H_element : 9"  # scripted group (container) (typed FeaturePython)
  n = 9
  ref = H_element
FEATURE [App::DocumentObjectGroupPython] N_element037  label="N_element : 016"  # scripted group (container) (typed FeaturePython)
  n = 1
  ref = N_element
FEATURE [App::DocumentObjectGroupPython] O_element084  label="O_element : 045"  # scripted group (container) (typed FeaturePython)
  n = 1
  ref = O_element
FEATURE [App::DocumentObjectGroupPython] G4_POLYVINYL_PYRROLIDONE  # scripted group (container) (typed FeaturePython)
  Dunit = g/cm3
  Dvalue = 1.25
  Group = -> [C_element095,H_element087,N_element037,O_element084]
  conduct = 2
  density = 1
  expand = 3
  formula = G4_POLYVINYL_PYRROLIDONE
  name = G4_POLYVINYL_PYRROLIDONE
  specific = 4
FEATURE [App::DocumentObjectGroupPython] K_element008  label="K_element : 1"  # scripted group (container) (typed FeaturePython)
  n = 1
  ref = K_element
FEATURE [App::DocumentObjectGroupPython] I_element006  label="I_element : 003"  # scripted group (container) (typed FeaturePython)
  n = 1
  ref = I_element
FEATURE [App::DocumentObjectGroupPython] G4_POTASSIUM_IODIDE  # scripted group (container) (typed FeaturePython)
  Dunit = g/cm3
  Dvalue = 3.13
  Group = -> [K_element008,I_element006]
  conduct = 2
  density = 1
  expand = 3
  formula = G4_POTASSIUM_IODIDE
  name = G4_POTASSIUM_IODIDE
  specific = 4
FEATURE [App::DocumentObjectGroupPython] K_element009  label="K_element : 2"  # scripted group (container) (typed FeaturePython)
  n = 2
  ref = K_element
FEATURE [App::DocumentObjectGroupPython] O_element085  label="O_element : 046"  # scripted group (container) (typed FeaturePython)
  n = 1
  ref = O_element
FEATURE [App::DocumentObjectGroupPython] G4_POTASSIUM_OXIDE  # scripted group (container) (typed FeaturePython)
  Dunit = g/cm3
  Dvalue = 2.32
  Group = -> [K_element009,O_element085]
  conduct = 2
  density = 1
  expand = 3
  formula = G4_POTASSIUM_OXIDE
  name = G4_POTASSIUM_OXIDE
  specific = 4
FEATURE [App::DocumentObjectGroupPython] C_element096  label="C_element : 054"  # scripted group (container) (typed FeaturePython)
  n = 3
  ref = C_element
FEATURE [App::DocumentObjectGroupPython] H_element088  label="H_element : 049"  # scripted group (container) (typed FeaturePython)
  n = 8
  ref = H_element
FEATURE [App::DocumentObjectGroupPython] G4_PROPANE  # scripted group (container) (typed FeaturePython)
  Dunit = g/cm3
  Dvalue = 0.00187939
  Group = -> [C_element096,H_element088]
  conduct = 2
  density = 1
  expand = 3
  formula = G4_PROPANE
  name = G4_PROPANE
  specific = 4
FEATURE [App::DocumentObjectGroupPython] C_element097  label="C_element : 055"  # scripted group (container) (typed FeaturePython)
  n = 3
  ref = C_element
FEATURE [App::DocumentObjectGroupPython] H_element089  label="H_element : 050"  # scripted group (container) (typed FeaturePython)
  n = 8
  ref = H_element
FEATURE [App::DocumentObjectGroupPython] G4_lPROPANE  # scripted group (container) (typed FeaturePython)
  Dunit = g/cm3
  Dvalue = 0.43
  Group = -> [C_element097,H_element089]
  conduct = 2
  density = 1
  expand = 3
  formula = G4_lPROPANE
  name = G4_lPROPANE
  specific = 4
FEATURE [App::DocumentObjectGroupPython] C_element098  label="C_element : 056"  # scripted group (container) (typed FeaturePython)
  n = 3
  ref = C_element
FEATURE [App::DocumentObjectGroupPython] H_element090  label="H_element : 051"  # scripted group (container) (typed FeaturePython)
  n = 8
  ref = H_element
FEATURE [App::DocumentObjectGroupPython] O_element086  label="O_element : 047"  # scripted group (container) (typed FeaturePython)
  n = 1
  ref = O_element
FEATURE [App::DocumentObjectGroupPython] G4_N_PROPYL_ALCOHOL  label="G4_N-PROPYL_ALCOHOL"  # scripted group (container) (typed FeaturePython)
  Dunit = g/cm3
  Dvalue = 0.8035
  Group = -> [C_element098,H_element090,O_element086]
  conduct = 2
  density = 1
  expand = 3
  formula = G4_N-PROPYL_ALCOHOL
  name = G4_N-PROPYL_ALCOHOL
  specific = 4
FEATURE [App::DocumentObjectGroupPython] C_element099  label="C_element : 057"  # scripted group (container) (typed FeaturePython)
  n = 5
  ref = C_element
FEATURE [App::DocumentObjectGroupPython] H_element091  label="H_element : 052"  # scripted group (container) (typed FeaturePython)
  n = 5
  ref = H_element
FEATURE [App::DocumentObjectGroupPython] N_element038  label="N_element : 017"  # scripted group (container) (typed FeaturePython)
  n = 1
  ref = N_element
FEATURE [App::DocumentObjectGroupPython] G4_PYRIDINE  # scripted group (container) (typed FeaturePython)
  Dunit = g/cm3
  Dvalue = 0.9819
  Group = -> [C_element099,H_element091,N_element038]
  conduct = 2
  density = 1
  expand = 3
  formula = G4_PYRIDINE
  name = G4_PYRIDINE
  specific = 4
FEATURE [App::DocumentObjectGroupPython] H_element092  label="H_element : 0.144"  # scripted group (container) (typed FeaturePython)
  n = 0.143711
FEATURE [App::DocumentObjectGroupPython] C_element100  label="C_element : 0.856"  # scripted group (container) (typed FeaturePython)
  n = 0.856289
FEATURE [App::DocumentObjectGroupPython] G4_RUBBER_BUTYL  # scripted group (container) (typed FeaturePython)
  Dunit = g/cm3
  Dvalue = 0.92
  Group = -> [H_element092,C_element100]
  conduct = 2
  density = 1
  expand = 3
  formula = G4_RUBBER_BUTYL
  name = G4_RUBBER_BUTYL
  specific = 4
FEATURE [App::DocumentObjectGroupPython] H_element093  label="H_element : 0.118"  # scripted group (container) (typed FeaturePython)
  n = 0.118371
FEATURE [App::DocumentObjectGroupPython] C_element101  label="C_element : 0.882"  # scripted group (container) (typed FeaturePython)
  n = 0.881629
FEATURE [App::DocumentObjectGroupPython] G4_RUBBER_NATURAL  # scripted group (container) (typed FeaturePython)
  Dunit = g/cm3
  Dvalue = 0.92
  Group = -> [H_element093,C_element101]
  conduct = 2
  density = 1
  expand = 3
  formula = G4_RUBBER_NATURAL
  name = G4_RUBBER_NATURAL
  specific = 4
FEATURE [App::DocumentObjectGroupPython] H_element094  label="H_element : 0.145"  # scripted group (container) (typed FeaturePython)
  n = 0.05692
FEATURE [App::DocumentObjectGroupPython] C_element102  label="C_element : 0.543"  # scripted group (container) (typed FeaturePython)
  n = 0.542646
FEATURE [App::DocumentObjectGroupPython] Cl_element021  label="Cl_element : 0.400"  # scripted group (container) (typed FeaturePython)
  n = 0.400434
FEATURE [App::DocumentObjectGroupPython] G4_RUBBER_NEOPRENE  # scripted group (container) (typed FeaturePython)
  Dunit = g/cm3
  Dvalue = 1.23
  Group = -> [H_element094,C_element102,Cl_element021]
  conduct = 2
  density = 1
  expand = 3
  formula = G4_RUBBER_NEOPRENE
  name = G4_RUBBER_NEOPRENE
  specific = 4
FEATURE [App::DocumentObjectGroupPython] Si_element006  label="Si_element : 1"  # scripted group (container) (typed FeaturePython)
  n = 1
  ref = Si_element
FEATURE [App::DocumentObjectGroupPython] O_element087  label="O_element : 048"  # scripted group (container) (typed FeaturePython)
  n = 2
  ref = O_element
FEATURE [App::DocumentObjectGroupPython] G4_SILICON_DIOXIDE  # scripted group (container) (typed FeaturePython)
  Dunit = g/cm3
  Dvalue = 2.32
  Group = -> [Si_element006,O_element087]
  conduct = 2
  density = 1
  expand = 3
  formula = G4_SILICON_DIOXIDE
  name = G4_SILICON_DIOXIDE
  specific = 4
FEATURE [App::DocumentObjectGroupPython] Ag_element002  label="Ag_element : 1"  # scripted group (container) (typed FeaturePython)
  n = 1
  ref = Ag_element
FEATURE [App::DocumentObjectGroupPython] Br_element005  label="Br_element : 003"  # scripted group (container) (typed FeaturePython)
  n = 1
  ref = Br_element
FEATURE [App::DocumentObjectGroupPython] G4_SILVER_BROMIDE  # scripted group (container) (typed FeaturePython)
  Dunit = g/cm3
  Dvalue = 6.473
  Group = -> [Ag_element002,Br_element005]
  conduct = 2
  density = 1
  expand = 3
  formula = G4_SILVER_BROMIDE
  name = G4_SILVER_BROMIDE
  specific = 4
FEATURE [App::DocumentObjectGroupPython] Ag_element003  label="Ag_element : 002"  # scripted group (container) (typed FeaturePython)
  n = 1
  ref = Ag_element
FEATURE [App::DocumentObjectGroupPython] Cl_element022  label="Cl_element : 011"  # scripted group (container) (typed FeaturePython)
  n = 1
  ref = Cl_element
FEATURE [App::DocumentObjectGroupPython] G4_SILVER_CHLORIDE  # scripted group (container) (typed FeaturePython)
  Dunit = g/cm3
  Dvalue = 5.56
  Group = -> [Ag_element003,Cl_element022]
  conduct = 2
  density = 1
  expand = 3
  formula = G4_SILVER_CHLORIDE
  name = G4_SILVER_CHLORIDE
  specific = 4
FEATURE [App::DocumentObjectGroupPython] Br_element006  label="Br_element : 0.423"  # scripted group (container) (typed FeaturePython)
  n = 0.422895
FEATURE [App::DocumentObjectGroupPython] Ag_element004  label="Ag_element : 0.574"  # scripted group (container) (typed FeaturePython)
  n = 0.573748
FEATURE [App::DocumentObjectGroupPython] I_element007  label="I_element : 0.649"  # scripted group (container) (typed FeaturePython)
  n = 0.003357
FEATURE [App::DocumentObjectGroupPython] G4_SILVER_HALIDES  # scripted group (container) (typed FeaturePython)
  Dunit = g/cm3
  Dvalue = 6.47
  Group = -> [Br_element006,Ag_element004,I_element007]
  conduct = 2
  density = 1
  expand = 3
  formula = G4_SILVER_HALIDES
  name = G4_SILVER_HALIDES
  specific = 4
FEATURE [App::DocumentObjectGroupPython] Ag_element005  label="Ag_element : 003"  # scripted group (container) (typed FeaturePython)
  n = 1
  ref = Ag_element
FEATURE [App::DocumentObjectGroupPython] I_element008  label="I_element : 004"  # scripted group (container) (typed FeaturePython)
  n = 1
  ref = I_element
FEATURE [App::DocumentObjectGroupPython] G4_SILVER_IODIDE  # scripted group (container) (typed FeaturePython)
  Dunit = g/cm3
  Dvalue = 6.01
  Group = -> [Ag_element005,I_element008]
  conduct = 2
  density = 1
  expand = 3
  formula = G4_SILVER_IODIDE
  name = G4_SILVER_IODIDE
  specific = 4
FEATURE [App::DocumentObjectGroupPython] H_element095  label="H_element : 0.100"  # scripted group (container) (typed FeaturePython)
  n = 0.1
FEATURE [App::DocumentObjectGroupPython] C_element103  label="C_element : 0.204"  # scripted group (container) (typed FeaturePython)
  n = 0.204
FEATURE [App::DocumentObjectGroupPython] N_element039  label="N_element : 0.759"  # scripted group (container) (typed FeaturePython)
  n = 0.042
FEATURE [App::DocumentObjectGroupPython] O_element088  label="O_element : 0.645"  # scripted group (container) (typed FeaturePython)
  n = 0.645
FEATURE [App::DocumentObjectGroupPython] Na_element013  label="Na_element : 0.100"  # scripted group (container) (typed FeaturePython)
  n = 0.002
FEATURE [App::DocumentObjectGroupPython] P_element009  label="P_element : 0.107"  # scripted group (container) (typed FeaturePython)
  n = 0.001
FEATURE [App::DocumentObjectGroupPython] S_element020  label="S_element : 0.021"  # scripted group (container) (typed FeaturePython)
  n = 0.002
FEATURE [App::DocumentObjectGroupPython] Cl_element023  label="Cl_element : 0.590"  # scripted group (container) (typed FeaturePython)
  n = 0.003
FEATURE [App::DocumentObjectGroupPython] K_element010  label="K_element : 0.001"  # scripted group (container) (typed FeaturePython)
  n = 0.001
FEATURE [App::DocumentObjectGroupPython] G4_SKIN_ICRP  # scripted group (container) (typed FeaturePython)
  Dunit = g/cm3
  Dvalue = 1.09
  Group = -> [H_element095,C_element103,N_element039,O_element088,Na_element013,P_element009,S_element020,Cl_element023,K_element010]
  conduct = 2
  density = 1
  expand = 3
  formula = G4_SKIN_ICRP
  name = G4_SKIN_ICRP
  specific = 4
FEATURE [App::DocumentObjectGroupPython] Na_element014  label="Na_element : 2"  # scripted group (container) (typed FeaturePython)
  n = 2
  ref = Na_element
FEATURE [App::DocumentObjectGroupPython] C_element104  label="C_element : 058"  # scripted group (container) (typed FeaturePython)
  n = 1
  ref = C_element
FEATURE [App::DocumentObjectGroupPython] O_element089  label="O_element : 049"  # scripted group (container) (typed FeaturePython)
  n = 3
  ref = O_element
FEATURE [App::DocumentObjectGroupPython] G4_SODIUM_CARBONATE  # scripted group (container) (typed FeaturePython)
  Dunit = g/cm3
  Dvalue = 2.532
  Group = -> [Na_element014,C_element104,O_element089]
  conduct = 2
  density = 1
  expand = 3
  formula = G4_SODIUM_CARBONATE
  name = G4_SODIUM_CARBONATE
  specific = 4
FEATURE [App::DocumentObjectGroupPython] Na_element015  label="Na_element : 1"  # scripted group (container) (typed FeaturePython)
  n = 1
  ref = Na_element
FEATURE [App::DocumentObjectGroupPython] I_element009  label="I_element : 005"  # scripted group (container) (typed FeaturePython)
  n = 1
  ref = I_element
FEATURE [App::DocumentObjectGroupPython] G4_SODIUM_IODIDE  # scripted group (container) (typed FeaturePython)
  Dunit = g/cm3
  Dvalue = 3.667
  Group = -> [Na_element015,I_element009]
  conduct = 2
  density = 1
  expand = 3
  formula = G4_SODIUM_IODIDE
  name = G4_SODIUM_IODIDE
  specific = 4
FEATURE [App::DocumentObjectGroupPython] Na_element016  label="Na_element : 003"  # scripted group (container) (typed FeaturePython)
  n = 2
  ref = Na_element
FEATURE [App::DocumentObjectGroupPython] O_element090  label="O_element : 050"  # scripted group (container) (typed FeaturePython)
  n = 1
  ref = O_element
FEATURE [App::DocumentObjectGroupPython] G4_SODIUM_MONOXIDE  # scripted group (container) (typed FeaturePython)
  Dunit = g/cm3
  Dvalue = 2.27
  Group = -> [Na_element016,O_element090]
  conduct = 2
  density = 1
  expand = 3
  formula = G4_SODIUM_MONOXIDE
  name = G4_SODIUM_MONOXIDE
  specific = 4
FEATURE [App::DocumentObjectGroupPython] Na_element017  label="Na_element : 004"  # scripted group (container) (typed FeaturePython)
  n = 1
  ref = Na_element
FEATURE [App::DocumentObjectGroupPython] N_element040  label="N_element : 018"  # scripted group (container) (typed FeaturePython)
  n = 1
  ref = N_element
FEATURE [App::DocumentObjectGroupPython] O_element091  label="O_element : 051"  # scripted group (container) (typed FeaturePython)
  n = 3
  ref = O_element
FEATURE [App::DocumentObjectGroupPython] G4_SODIUM_NITRATE  # scripted group (container) (typed FeaturePython)
  Dunit = g/cm3
  Dvalue = 2.261
  Group = -> [Na_element017,N_element040,O_element091]
  conduct = 2
  density = 1
  expand = 3
  formula = G4_SODIUM_NITRATE
  name = G4_SODIUM_NITRATE
  specific = 4
FEATURE [App::DocumentObjectGroupPython] C_element105  label="C_element : 059"  # scripted group (container) (typed FeaturePython)
  n = 14
  ref = C_element
FEATURE [App::DocumentObjectGroupPython] H_element096  label="H_element : 053"  # scripted group (container) (typed FeaturePython)
  n = 12
  ref = H_element
FEATURE [App::DocumentObjectGroupPython] G4_STILBENE  # scripted group (container) (typed FeaturePython)
  Dunit = g/cm3
  Dvalue = 0.9707
  Group = -> [C_element105,H_element096]
  conduct = 2
  density = 1
  expand = 3
  formula = G4_STILBENE
  name = G4_STILBENE
  specific = 4
FEATURE [App::DocumentObjectGroupPython] C_element106  label="C_element : 12"  # scripted group (container) (typed FeaturePython)
  n = 12
  ref = C_element
FEATURE [App::DocumentObjectGroupPython] H_element097  label="H_element : 22"  # scripted group (container) (typed FeaturePython)
  n = 22
  ref = H_element
FEATURE [App::DocumentObjectGroupPython] O_element092  label="O_element : 11"  # scripted group (container) (typed FeaturePython)
  n = 11
  ref = O_element
FEATURE [App::DocumentObjectGroupPython] G4_SUCROSE  # scripted group (container) (typed FeaturePython)
  Dunit = g/cm3
  Dvalue = 1.5805
  Group = -> [C_element106,H_element097,O_element092]
  conduct = 2
  density = 1
  expand = 3
  formula = G4_SUCROSE
  name = G4_SUCROSE
  specific = 4
FEATURE [App::DocumentObjectGroupPython] C_element107  label="C_element : 18"  # scripted group (container) (typed FeaturePython)
  n = 18
  ref = C_element
FEATURE [App::DocumentObjectGroupPython] H_element098  label="H_element : 054"  # scripted group (container) (typed FeaturePython)
  n = 14
  ref = H_element
FEATURE [App::DocumentObjectGroupPython] G4_TERPHENYL  # scripted group (container) (typed FeaturePython)
  Dunit = g/cm3
  Dvalue = 1.24
  Group = -> [C_element107,H_element098]
  conduct = 2
  density = 1
  expand = 3
  formula = G4_TERPHENYL
  name = G4_TERPHENYL
  specific = 4
FEATURE [App::DocumentObjectGroupPython] H_element099  label="H_element : 0.146"  # scripted group (container) (typed FeaturePython)
  n = 0.106
FEATURE [App::DocumentObjectGroupPython] C_element108  label="C_element : 0.883"  # scripted group (container) (typed FeaturePython)
  n = 0.099
FEATURE [App::DocumentObjectGroupPython] N_element041  label="N_element : 0.020"  # scripted group (container) (typed FeaturePython)
  n = 0.02
FEATURE [App::DocumentObjectGroupPython] O_element093  label="O_element : 0.766"  # scripted group (container) (typed FeaturePython)
  n = 0.766
FEATURE [App::DocumentObjectGroupPython] Na_element018  label="Na_element : 0.101"  # scripted group (container) (typed FeaturePython)
  n = 0.002
FEATURE [App::DocumentObjectGroupPython] P_element010  label="P_element : 0.108"  # scripted group (container) (typed FeaturePython)
  n = 0.001
FEATURE [App::DocumentObjectGroupPython] S_element021  label="S_element : 0.022"  # scripted group (container) (typed FeaturePython)
  n = 0.002
FEATURE [App::DocumentObjectGroupPython] Cl_element024  label="Cl_element : 0.002"  # scripted group (container) (typed FeaturePython)
  n = 0.002
FEATURE [App::DocumentObjectGroupPython] K_element011  label="K_element : 0.017"  # scripted group (container) (typed FeaturePython)
  n = 0.002
FEATURE [App::DocumentObjectGroupPython] G4_TESTIS_ICRP  # scripted group (container) (typed FeaturePython)
  Dunit = g/cm3
  Dvalue = 1.04
  Group = -> [H_element099,C_element108,N_element041,O_element093,Na_element018,P_element010,S_element021,Cl_element024,K_element011]
  conduct = 2
  density = 1
  expand = 3
  formula = G4_TESTIS_ICRP
  name = G4_TESTIS_ICRP
  specific = 4
FEATURE [App::DocumentObjectGroupPython] C_element109  label="C_element : 060"  # scripted group (container) (typed FeaturePython)
  n = 2
  ref = C_element
FEATURE [App::DocumentObjectGroupPython] Cl_element025  label="Cl_element : 012"  # scripted group (container) (typed FeaturePython)
  n = 4
  ref = Cl_element
FEATURE [App::DocumentObjectGroupPython] G4_TETRACHLOROETHYLENE  # scripted group (container) (typed FeaturePython)
  Dunit = g/cm3
  Dvalue = 1.625
  Group = -> [C_element109,Cl_element025]
  conduct = 2
  density = 1
  expand = 3
  formula = G4_TETRACHLOROETHYLENE
  name = G4_TETRACHLOROETHYLENE
  specific = 4
FEATURE [App::DocumentObjectGroupPython] Tl_element001  label="Tl_element : 1"  # scripted group (container) (typed FeaturePython)
  n = 1
  ref = Tl_element
FEATURE [App::DocumentObjectGroupPython] Cl_element026  label="Cl_element : 013"  # scripted group (container) (typed FeaturePython)
  n = 1
  ref = Cl_element
FEATURE [App::DocumentObjectGroupPython] G4_THALLIUM_CHLORIDE  # scripted group (container) (typed FeaturePython)
  Dunit = g/cm3
  Dvalue = 7.004
  Group = -> [Tl_element001,Cl_element026]
  conduct = 2
  density = 1
  expand = 3
  formula = G4_THALLIUM_CHLORIDE
  name = G4_THALLIUM_CHLORIDE
  specific = 4
FEATURE [App::DocumentObjectGroupPython] H_element100  label="H_element : 0.147"  # scripted group (container) (typed FeaturePython)
  n = 0.105
FEATURE [App::DocumentObjectGroupPython] C_element110  label="C_element : 0.256"  # scripted group (container) (typed FeaturePython)
  n = 0.256
FEATURE [App::DocumentObjectGroupPython] N_element042  label="N_element : 0.760"  # scripted group (container) (typed FeaturePython)
  n = 0.027
FEATURE [App::DocumentObjectGroupPython] O_element094  label="O_element : 0.602"  # scripted group (container) (typed FeaturePython)
  n = 0.602
FEATURE [App::DocumentObjectGroupPython] Na_element019  label="Na_element : 0.102"  # scripted group (container) (typed FeaturePython)
  n = 0.001
FEATURE [App::DocumentObjectGroupPython] P_element011  label="P_element : 0.109"  # scripted group (container) (typed FeaturePython)
  n = 0.002
FEATURE [App::DocumentObjectGroupPython] S_element022  label="S_element : 0.023"  # scripted group (container) (typed FeaturePython)
  n = 0.003
FEATURE [App::DocumentObjectGroupPython] Cl_element027  label="Cl_element : 0.591"  # scripted group (container) (typed FeaturePython)
  n = 0.002
FEATURE [App::DocumentObjectGroupPython] K_element012  label="K_element : 0.018"  # scripted group (container) (typed FeaturePython)
  n = 0.002
FEATURE [App::DocumentObjectGroupPython] G4_TISSUE_SOFT_ICRP  # scripted group (container) (typed FeaturePython)
  Dunit = g/cm3
  Dvalue = 1.03
  Group = -> [H_element100,C_element110,N_element042,O_element094,Na_element019,P_element011,S_element022,Cl_element027,K_element012]
  conduct = 2
  density = 1
  expand = 3
  formula = G4_TISSUE_SOFT_ICRP
  name = G4_TISSUE_SOFT_ICRP
  specific = 4
FEATURE [App::DocumentObjectGroupPython] H_element101  label="H_element : 0.148"  # scripted group (container) (typed FeaturePython)
  n = 0.101
FEATURE [App::DocumentObjectGroupPython] C_element111  label="C_element : 0.111"  # scripted group (container) (typed FeaturePython)
  n = 0.111
FEATURE [App::DocumentObjectGroupPython] N_element043  label="N_element : 0.026"  # scripted group (container) (typed FeaturePython)
  n = 0.026
FEATURE [App::DocumentObjectGroupPython] O_element095  label="O_element : 0.762"  # scripted group (container) (typed FeaturePython)
  n = 0.762
FEATURE [App::DocumentObjectGroupPython] G4_TISSUE_SOFT_ICRU_4  label="G4_TISSUE_SOFT_ICRU-4"  # scripted group (container) (typed FeaturePython)
  Dunit = g/cm3
  Dvalue = 1
  Group = -> [H_element101,C_element111,N_element043,O_element095]
  conduct = 2
  density = 1
  expand = 3
  formula = G4_TISSUE_SOFT_ICRU-4
  name = G4_TISSUE_SOFT_ICRU-4
  specific = 4
FEATURE [App::DocumentObjectGroupPython] H_element102  label="H_element : 0.149"  # scripted group (container) (typed FeaturePython)
  n = 0.101869
FEATURE [App::DocumentObjectGroupPython] C_element112  label="C_element : 0.456"  # scripted group (container) (typed FeaturePython)
  n = 0.456179
FEATURE [App::DocumentObjectGroupPython] N_element044  label="N_element : 0.761"  # scripted group (container) (typed FeaturePython)
  n = 0.035172
FEATURE [App::DocumentObjectGroupPython] O_element096  label="O_element : 0.407"  # scripted group (container) (typed FeaturePython)
  n = 0.40678
FEATURE [App::DocumentObjectGroupPython] G4_TISSUE_METHANE  label="G4_TISSUE-METHANE"  # scripted group (container) (typed FeaturePython)
  Dunit = g/cm3
  Dvalue = 0.00106409
  Group = -> [H_element102,C_element112,N_element044,O_element096]
  conduct = 2
  density = 1
  expand = 3
  formula = G4_TISSUE-METHANE
  name = G4_TISSUE-METHANE
  specific = 4
FEATURE [App::DocumentObjectGroupPython] H_element103  label="H_element : 0.103"  # scripted group (container) (typed FeaturePython)
  n = 0.102672
FEATURE [App::DocumentObjectGroupPython] C_element113  label="C_element : 0.569"  # scripted group (container) (typed FeaturePython)
  n = 0.56894
FEATURE [App::DocumentObjectGroupPython] N_element045  label="N_element : 0.762"  # scripted group (container) (typed FeaturePython)
  n = 0.035022
FEATURE [App::DocumentObjectGroupPython] O_element097  label="O_element : 0.293"  # scripted group (container) (typed FeaturePython)
  n = 0.293366
FEATURE [App::DocumentObjectGroupPython] G4_TISSUE_PROPANE  label="G4_TISSUE-PROPANE"  # scripted group (container) (typed FeaturePython)
  Dunit = g/cm3
  Dvalue = 0.00182628
  Group = -> [H_element103,C_element113,N_element045,O_element097]
  conduct = 2
  density = 1
  expand = 3
  formula = G4_TISSUE-PROPANE
  name = G4_TISSUE-PROPANE
  specific = 4
FEATURE [App::DocumentObjectGroupPython] Ti_element003  label="Ti_element : 1"  # scripted group (container) (typed FeaturePython)
  n = 1
  ref = Ti_element
FEATURE [App::DocumentObjectGroupPython] O_element098  label="O_element : 052"  # scripted group (container) (typed FeaturePython)
  n = 2
  ref = O_element
FEATURE [App::DocumentObjectGroupPython] G4_TITANIUM_DIOXIDE  # scripted group (container) (typed FeaturePython)
  Dunit = g/cm3
  Dvalue = 4.26
  Group = -> [Ti_element003,O_element098]
  conduct = 2
  density = 1
  expand = 3
  formula = G4_TITANIUM_DIOXIDE
  name = G4_TITANIUM_DIOXIDE
  specific = 4
FEATURE [App::DocumentObjectGroupPython] C_element114  label="C_element : 061"  # scripted group (container) (typed FeaturePython)
  n = 7
  ref = C_element
FEATURE [App::DocumentObjectGroupPython] H_element104  label="H_element : 055"  # scripted group (container) (typed FeaturePython)
  n = 8
  ref = H_element
FEATURE [App::DocumentObjectGroupPython] G4_TOLUENE  # scripted group (container) (typed FeaturePython)
  Dunit = g/cm3
  Dvalue = 0.8669
  Group = -> [C_element114,H_element104]
  conduct = 2
  density = 1
  expand = 3
  formula = G4_TOLUENE
  name = G4_TOLUENE
  specific = 4
FEATURE [App::DocumentObjectGroupPython] C_element115  label="C_element : 062"  # scripted group (container) (typed FeaturePython)
  n = 2
  ref = C_element
FEATURE [App::DocumentObjectGroupPython] H_element105  label="H_element : 056"  # scripted group (container) (typed FeaturePython)
  n = 1
  ref = H_element
FEATURE [App::DocumentObjectGroupPython] Cl_element028  label="Cl_element : 014"  # scripted group (container) (typed FeaturePython)
  n = 3
  ref = Cl_element
FEATURE [App::DocumentObjectGroupPython] G4_TRICHLOROETHYLENE  # scripted group (container) (typed FeaturePython)
  Dunit = g/cm3
  Dvalue = 1.46
  Group = -> [C_element115,H_element105,Cl_element028]
  conduct = 2
  density = 1
  expand = 3
  formula = G4_TRICHLOROETHYLENE
  name = G4_TRICHLOROETHYLENE
  specific = 4
FEATURE [App::DocumentObjectGroupPython] C_element116  label="C_element : 063"  # scripted group (container) (typed FeaturePython)
  n = 6
  ref = C_element
FEATURE [App::DocumentObjectGroupPython] H_element106  label="H_element : 15"  # scripted group (container) (typed FeaturePython)
  n = 15
  ref = H_element
FEATURE [App::DocumentObjectGroupPython] O_element099  label="O_element : 053"  # scripted group (container) (typed FeaturePython)
  n = 4
  ref = O_element
FEATURE [App::DocumentObjectGroupPython] P_element012  label="P_element : 1"  # scripted group (container) (typed FeaturePython)
  n = 1
  ref = P_element
FEATURE [App::DocumentObjectGroupPython] G4_TRIETHYL_PHOSPHATE  # scripted group (container) (typed FeaturePython)
  Dunit = g/cm3
  Dvalue = 1.07
  Group = -> [C_element116,H_element106,O_element099,P_element012]
  conduct = 2
  density = 1
  expand = 3
  formula = G4_TRIETHYL_PHOSPHATE
  name = G4_TRIETHYL_PHOSPHATE
  specific = 4
FEATURE [App::DocumentObjectGroupPython] W_element003  label="W_element : 003"  # scripted group (container) (typed FeaturePython)
  n = 1
  ref = W_element
FEATURE [App::DocumentObjectGroupPython] F_element017  label="F_element : 6"  # scripted group (container) (typed FeaturePython)
  n = 6
  ref = F_element
FEATURE [App::DocumentObjectGroupPython] G4_TUNGSTEN_HEXAFLUORIDE  # scripted group (container) (typed FeaturePython)
  Dunit = g/cm3
  Dvalue = 2.4
  Group = -> [W_element003,F_element017]
  conduct = 2
  density = 1
  expand = 3
  formula = G4_TUNGSTEN_HEXAFLUORIDE
  name = G4_TUNGSTEN_HEXAFLUORIDE
  specific = 4
FEATURE [App::DocumentObjectGroupPython] U_element001  label="U_element : 1"  # scripted group (container) (typed FeaturePython)
  n = 1
  ref = U_element
FEATURE [App::DocumentObjectGroupPython] C_element117  label="C_element : 064"  # scripted group (container) (typed FeaturePython)
  n = 2
  ref = C_element
FEATURE [App::DocumentObjectGroupPython] G4_URANIUM_DICARBIDE  # scripted group (container) (typed FeaturePython)
  Dunit = g/cm3
  Dvalue = 11.28
  Group = -> [U_element001,C_element117]
  conduct = 2
  density = 1
  expand = 3
  formula = G4_URANIUM_DICARBIDE
  name = G4_URANIUM_DICARBIDE
  specific = 4
FEATURE [App::DocumentObjectGroupPython] U_element002  label="U_element : 002"  # scripted group (container) (typed FeaturePython)
  n = 1
  ref = U_element
FEATURE [App::DocumentObjectGroupPython] C_element118  label="C_element : 065"  # scripted group (container) (typed FeaturePython)
  n = 1
  ref = C_element
FEATURE [App::DocumentObjectGroupPython] G4_URANIUM_MONOCARBIDE  # scripted group (container) (typed FeaturePython)
  Dunit = g/cm3
  Dvalue = 13.63
  Group = -> [U_element002,C_element118]
  conduct = 2
  density = 1
  expand = 3
  formula = G4_URANIUM_MONOCARBIDE
  name = G4_URANIUM_MONOCARBIDE
  specific = 4
FEATURE [App::DocumentObjectGroupPython] U_element003  label="U_element : 003"  # scripted group (container) (typed FeaturePython)
  n = 1
  ref = U_element
FEATURE [App::DocumentObjectGroupPython] O_element100  label="O_element : 054"  # scripted group (container) (typed FeaturePython)
  n = 2
  ref = O_element
FEATURE [App::DocumentObjectGroupPython] G4_URANIUM_OXIDE  # scripted group (container) (typed FeaturePython)
  Dunit = g/cm3
  Dvalue = 10.96
  Group = -> [U_element003,O_element100]
  conduct = 2
  density = 1
  expand = 3
  formula = G4_URANIUM_OXIDE
  name = G4_URANIUM_OXIDE
  specific = 4
FEATURE [App::DocumentObjectGroupPython] C_element119  label="C_element : 066"  # scripted group (container) (typed FeaturePython)
  n = 1
  ref = C_element
FEATURE [App::DocumentObjectGroupPython] H_element107  label="H_element : 057"  # scripted group (container) (typed FeaturePython)
  n = 4
  ref = H_element
FEATURE [App::DocumentObjectGroupPython] N_element046  label="N_element : 019"  # scripted group (container) (typed FeaturePython)
  n = 2
  ref = N_element
FEATURE [App::DocumentObjectGroupPython] O_element101  label="O_element : 055"  # scripted group (container) (typed FeaturePython)
  n = 1
  ref = O_element
FEATURE [App::DocumentObjectGroupPython] G4_UREA  # scripted group (container) (typed FeaturePython)
  Dunit = g/cm3
  Dvalue = 1.323
  Group = -> [C_element119,H_element107,N_element046,O_element101]
  conduct = 2
  density = 1
  expand = 3
  formula = G4_UREA
  name = G4_UREA
  specific = 4
FEATURE [App::DocumentObjectGroupPython] C_element120  label="C_element : 067"  # scripted group (container) (typed FeaturePython)
  n = 5
  ref = C_element
FEATURE [App::DocumentObjectGroupPython] H_element108  label="H_element : 058"  # scripted group (container) (typed FeaturePython)
  n = 11
  ref = H_element
FEATURE [App::DocumentObjectGroupPython] N_element047  label="N_element : 020"  # scripted group (container) (typed FeaturePython)
  n = 1
  ref = N_element
FEATURE [App::DocumentObjectGroupPython] O_element102  label="O_element : 056"  # scripted group (container) (typed FeaturePython)
  n = 2
  ref = O_element
FEATURE [App::DocumentObjectGroupPython] G4_VALINE  # scripted group (container) (typed FeaturePython)
  Dunit = g/cm3
  Dvalue = 1.23
  Group = -> [C_element120,H_element108,N_element047,O_element102]
  conduct = 2
  density = 1
  expand = 3
  formula = G4_VALINE
  name = G4_VALINE
  specific = 4
FEATURE [App::DocumentObjectGroupPython] H_element109  label="H_element : 0.009"  # scripted group (container) (typed FeaturePython)
  n = 0.009417
FEATURE [App::DocumentObjectGroupPython] C_element121  label="C_element : 0.281"  # scripted group (container) (typed FeaturePython)
  n = 0.280555
FEATURE [App::DocumentObjectGroupPython] F_element018  label="F_element : 0.710"  # scripted group (container) (typed FeaturePython)
  n = 0.710028
FEATURE [App::DocumentObjectGroupPython] G4_VITON  # scripted group (container) (typed FeaturePython)
  Dunit = g/cm3
  Dvalue = 1.8
  Group = -> [H_element109,C_element121,F_element018]
  conduct = 2
  density = 1
  expand = 3
  formula = G4_VITON
  name = G4_VITON
  specific = 4
FEATURE [App::DocumentObjectGroupPython] H_element110  label="H_element : 059"  # scripted group (container) (typed FeaturePython)
  n = 2
  ref = H_element
FEATURE [App::DocumentObjectGroupPython] O_element103  label="O_element : 057"  # scripted group (container) (typed FeaturePython)
  n = 1
  ref = O_element
FEATURE [App::DocumentObjectGroupPython] G4_WATER  # scripted group (container) (typed FeaturePython)
  Dunit = g/cm3
  Dvalue = 1
  Group = -> [H_element110,O_element103]
  conduct = 2
  density = 1
  expand = 3
  formula = G4_WATER
  name = G4_WATER
  specific = 4
FEATURE [App::DocumentObjectGroupPython] H_element111  label="H_element : 060"  # scripted group (container) (typed FeaturePython)
  n = 2
  ref = H_element
FEATURE [App::DocumentObjectGroupPython] O_element104  label="O_element : 058"  # scripted group (container) (typed FeaturePython)
  n = 1
  ref = O_element
FEATURE [App::DocumentObjectGroupPython] G4_WATER_VAPOR  # scripted group (container) (typed FeaturePython)
  Dunit = g/cm3
  Dvalue = 0.000756182
  Group = -> [H_element111,O_element104]
  conduct = 2
  density = 1
  expand = 3
  formula = G4_WATER_VAPOR
  name = G4_WATER_VAPOR
  specific = 4
FEATURE [App::DocumentObjectGroupPython] C_element122  label="C_element : 068"  # scripted group (container) (typed FeaturePython)
  n = 8
  ref = C_element
FEATURE [App::DocumentObjectGroupPython] H_element112  label="H_element : 061"  # scripted group (container) (typed FeaturePython)
  n = 10
  ref = H_element
FEATURE [App::DocumentObjectGroupPython] G4_XYLENE  # scripted group (container) (typed FeaturePython)
  Dunit = g/cm3
  Dvalue = 0.87
  Group = -> [C_element122,H_element112]
  conduct = 2
  density = 1
  expand = 3
  formula = G4_XYLENE
  name = G4_XYLENE
  specific = 4
FEATURE [App::DocumentObjectGroupPython] C_element123  label="C_element : 069"  # scripted group (container) (typed FeaturePython)
  n = 1
  ref = C_element
FEATURE [App::DocumentObjectGroupPython] G4_GRAPHITE  # scripted group (container) (typed FeaturePython)
  Dunit = g/cm3
  Dvalue = 2.21
  Group = -> [C_element123]
  conduct = 2
  density = 1
  expand = 3
  formula = G4_GRAPHITE
  name = G4_GRAPHITE
  specific = 4
FEATURE [App::DocumentObjectGroupPython] NIST  # scripted group (container) (typed FeaturePython)
  Group = -> [G4_A_150_TISSUE,G4_ACETONE,G4_ACETYLENE,G4_ADENINE,G4_ADIPOSE_TISSUE_ICRP,G4_AIR,G4_ALANINE,G4_ALUMINUM_OXIDE,G4_AMBER,G4_AMMONIA,G4_ANILINE,G4_ANTHRACENE,G4_B_100_BONE,G4_BAKELITE,G4_BARIUM_FLUORIDE,G4_BARIUM_SULFATE,G4_BENZENE,G4_BERYLLIUM_OXIDE,G4_BGO,G4_BLOOD_ICRP,G4_BONE_COMPACT_ICRU,G4_BONE_CORTICAL_ICRP,G4_BORON_CARBIDE,G4_BORON_OXIDE,G4_BRAIN_ICRP,G4_BUTANE,G4_N_BUTYL_ALCOHOL,G4_C_552,+152 more]
FEATURE [App::DocumentObjectGroupPython] H_element113  label="H_element : 062"  # scripted group (container) (typed FeaturePython)
  n = 1
  ref = H_element
FEATURE [App::DocumentObjectGroupPython] G4_H  # scripted group (container) (typed FeaturePython)
  Dunit = g/cm3
  Dvalue = 8.3748e-05
  Group = -> [H_element113]
  conduct = 2
  density = 1
  expand = 3
  formula = H
  name = G4_H
  specific = 4
FEATURE [App::DocumentObjectGroupPython] He_element001  label="He_element : 1"  # scripted group (container) (typed FeaturePython)
  n = 1
  ref = He_element
FEATURE [App::DocumentObjectGroupPython] G4_He  # scripted group (container) (typed FeaturePython)
  Dunit = g/cm3
  Dvalue = 0.000166322
  Group = -> [He_element001]
  conduct = 2
  density = 1
  expand = 3
  formula = He
  name = G4_He
  specific = 4
FEATURE [App::DocumentObjectGroupPython] Li_element008  label="Li_element : 008"  # scripted group (container) (typed FeaturePython)
  n = 1
  ref = Li_element
FEATURE [App::DocumentObjectGroupPython] G4_Li  # scripted group (container) (typed FeaturePython)
  Dunit = g/cm3
  Dvalue = 0.534
  Group = -> [Li_element008]
  conduct = 2
  density = 1
  expand = 3
  formula = Li
  name = G4_Li
  specific = 4
FEATURE [App::DocumentObjectGroupPython] Be_element002  label="Be_element : 002"  # scripted group (container) (typed FeaturePython)
  n = 1
  ref = Be_element
FEATURE [App::DocumentObjectGroupPython] G4_Be  # scripted group (container) (typed FeaturePython)
  Dunit = g/cm3
  Dvalue = 1.848
  Group = -> [Be_element002]
  conduct = 2
  density = 1
  expand = 3
  formula = Be
  name = G4_Be
  specific = 4
FEATURE [App::DocumentObjectGroupPython] B_element007  label="B_element : 007"  # scripted group (container) (typed FeaturePython)
  n = 1
  ref = B_element
FEATURE [App::DocumentObjectGroupPython] G4_B  # scripted group (container) (typed FeaturePython)
  Dunit = g/cm3
  Dvalue = 2.37
  Group = -> [B_element007]
  conduct = 2
  density = 1
  expand = 3
  formula = B
  name = G4_B
  specific = 4
FEATURE [App::DocumentObjectGroupPython] C_element124  label="C_element : 070"  # scripted group (container) (typed FeaturePython)
  n = 1
  ref = C_element
FEATURE [App::DocumentObjectGroupPython] G4_C  # scripted group (container) (typed FeaturePython)
  Dunit = g/cm3
  Dvalue = 2
  Group = -> [C_element124]
  conduct = 2
  density = 1
  expand = 3
  formula = C
  name = G4_C
  specific = 4
FEATURE [App::DocumentObjectGroupPython] N_element048  label="N_element : 021"  # scripted group (container) (typed FeaturePython)
  n = 1
  ref = N_element
FEATURE [App::DocumentObjectGroupPython] G4_N  # scripted group (container) (typed FeaturePython)
  Dunit = g/cm3
  Dvalue = 0.0011652
  Group = -> [N_element048]
  conduct = 2
  density = 1
  expand = 3
  formula = N
  name = G4_N
  specific = 4
FEATURE [App::DocumentObjectGroupPython] O_element105  label="O_element : 059"  # scripted group (container) (typed FeaturePython)
  n = 1
  ref = O_element
FEATURE [App::DocumentObjectGroupPython] G4_O  # scripted group (container) (typed FeaturePython)
  Dunit = g/cm3
  Dvalue = 0.00133151
  Group = -> [O_element105]
  conduct = 2
  density = 1
  expand = 3
  formula = O
  name = G4_O
  specific = 4
FEATURE [App::DocumentObjectGroupPython] F_element019  label="F_element : 008"  # scripted group (container) (typed FeaturePython)
  n = 1
  ref = F_element
FEATURE [App::DocumentObjectGroupPython] G4_F  # scripted group (container) (typed FeaturePython)
  Dunit = g/cm3
  Dvalue = 0.00158029
  Group = -> [F_element019]
  conduct = 2
  density = 1
  expand = 3
  formula = F
  name = G4_F
  specific = 4
FEATURE [App::DocumentObjectGroupPython] Ne_element001  label="Ne_element : 1"  # scripted group (container) (typed FeaturePython)
  n = 1
  ref = Ne_element
FEATURE [App::DocumentObjectGroupPython] G4_Ne  # scripted group (container) (typed FeaturePython)
  Dunit = g/cm3
  Dvalue = 0.000838505
  Group = -> [Ne_element001]
  conduct = 2
  density = 1
  expand = 3
  formula = Ne
  name = G4_Ne
  specific = 4
FEATURE [App::DocumentObjectGroupPython] Na_element020  label="Na_element : 005"  # scripted group (container) (typed FeaturePython)
  n = 1
  ref = Na_element
FEATURE [App::DocumentObjectGroupPython] G4_Na  # scripted group (container) (typed FeaturePython)
  Dunit = g/cm3
  Dvalue = 0.971
  Group = -> [Na_element020]
  conduct = 2
  density = 1
  expand = 3
  formula = Na
  name = G4_Na
  specific = 4
FEATURE [App::DocumentObjectGroupPython] Mg_element011  label="Mg_element : 005"  # scripted group (container) (typed FeaturePython)
  n = 1
  ref = Mg_element
FEATURE [App::DocumentObjectGroupPython] G4_Mg  # scripted group (container) (typed FeaturePython)
  Dunit = g/cm3
  Dvalue = 1.74
  Group = -> [Mg_element011]
  conduct = 2
  density = 1
  expand = 3
  formula = Mg
  name = G4_Mg
  specific = 4
FEATURE [App::DocumentObjectGroupPython] Al_element004  label="Al_element : 1"  # scripted group (container) (typed FeaturePython)
  n = 1
  ref = Al_element
FEATURE [App::DocumentObjectGroupPython] G4_Al  # scripted group (container) (typed FeaturePython)
  Dunit = g/cm3
  Dvalue = 2.699
  Group = -> [Al_element004]
  conduct = 2
  density = 1
  expand = 3
  formula = Al
  name = G4_Al
  specific = 4
FEATURE [App::DocumentObjectGroupPython] Si_element007  label="Si_element : 002"  # scripted group (container) (typed FeaturePython)
  n = 1
  ref = Si_element
FEATURE [App::DocumentObjectGroupPython] G4_Si  # scripted group (container) (typed FeaturePython)
  Dunit = g/cm3
  Dvalue = 2.33
  Group = -> [Si_element007]
  conduct = 2
  density = 1
  expand = 3
  formula = Si
  name = G4_Si
  specific = 4
FEATURE [App::DocumentObjectGroupPython] P_element013  label="P_element : 002"  # scripted group (container) (typed FeaturePython)
  n = 1
  ref = P_element
FEATURE [App::DocumentObjectGroupPython] G4_P  # scripted group (container) (typed FeaturePython)
  Dunit = g/cm3
  Dvalue = 2.2
  Group = -> [P_element013]
  conduct = 2
  density = 1
  expand = 3
  formula = P
  name = G4_P
  specific = 4
FEATURE [App::DocumentObjectGroupPython] S_element023  label="S_element : 007"  # scripted group (container) (typed FeaturePython)
  n = 1
  ref = S_element
FEATURE [App::DocumentObjectGroupPython] G4_S  # scripted group (container) (typed FeaturePython)
  Dunit = g/cm3
  Dvalue = 2
  Group = -> [S_element023]
  conduct = 2
  density = 1
  expand = 3
  formula = S
  name = G4_S
  specific = 4
FEATURE [App::DocumentObjectGroupPython] Cl_element029  label="Cl_element : 015"  # scripted group (container) (typed FeaturePython)
  n = 1
  ref = Cl_element
FEATURE [App::DocumentObjectGroupPython] G4_Cl  # scripted group (container) (typed FeaturePython)
  Dunit = g/cm3
  Dvalue = 0.00299473
  Group = -> [Cl_element029]
  conduct = 2
  density = 1
  expand = 3
  formula = Cl
  name = G4_Cl
  specific = 4
FEATURE [App::DocumentObjectGroupPython] Ar_element002  label="Ar_element : 1"  # scripted group (container) (typed FeaturePython)
  n = 1
  ref = Ar_element
FEATURE [App::DocumentObjectGroupPython] G4_Ar  # scripted group (container) (typed FeaturePython)
  Dunit = g/cm3
  Dvalue = 0.00166201
  Group = -> [Ar_element002]
  conduct = 2
  density = 1
  expand = 3
  formula = Ar
  name = G4_Ar
  specific = 4
FEATURE [App::DocumentObjectGroupPython] K_element013  label="K_element : 003"  # scripted group (container) (typed FeaturePython)
  n = 1
  ref = K_element
FEATURE [App::DocumentObjectGroupPython] G4_K  # scripted group (container) (typed FeaturePython)
  Dunit = g/cm3
  Dvalue = 0.862
  Group = -> [K_element013]
  conduct = 2
  density = 1
  expand = 3
  formula = K
  name = G4_K
  specific = 4
FEATURE [App::DocumentObjectGroupPython] Ca_element014  label="Ca_element : 007"  # scripted group (container) (typed FeaturePython)
  n = 1
  ref = Ca_element
FEATURE [App::DocumentObjectGroupPython] G4_Ca  # scripted group (container) (typed FeaturePython)
  Dunit = g/cm3
  Dvalue = 1.55
  Group = -> [Ca_element014]
  conduct = 2
  density = 1
  expand = 3
  formula = Ca
  name = G4_Ca
  specific = 4
FEATURE [App::DocumentObjectGroupPython] Sc_element001  label="Sc_element : 1"  # scripted group (container) (typed FeaturePython)
  n = 1
  ref = Sc_element
FEATURE [App::DocumentObjectGroupPython] G4_Sc  # scripted group (container) (typed FeaturePython)
  Dunit = g/cm3
  Dvalue = 2.989
  Group = -> [Sc_element001]
  conduct = 2
  density = 1
  expand = 3
  formula = Sc
  name = G4_Sc
  specific = 4
FEATURE [App::DocumentObjectGroupPython] Ti_element004  label="Ti_element : 002"  # scripted group (container) (typed FeaturePython)
  n = 1
  ref = Ti_element
FEATURE [App::DocumentObjectGroupPython] G4_Ti  # scripted group (container) (typed FeaturePython)
  Dunit = g/cm3
  Dvalue = 4.54
  Group = -> [Ti_element004]
  conduct = 2
  density = 1
  expand = 3
  formula = Ti
  name = G4_Ti
  specific = 4
FEATURE [App::DocumentObjectGroupPython] V_element001  label="V_element : 1"  # scripted group (container) (typed FeaturePython)
  n = 1
  ref = V_element
FEATURE [App::DocumentObjectGroupPython] G4_V  # scripted group (container) (typed FeaturePython)
  Dunit = g/cm3
  Dvalue = 6.11
  Group = -> [V_element001]
  conduct = 2
  density = 1
  expand = 3
  formula = V
  name = G4_V
  specific = 4
FEATURE [App::DocumentObjectGroupPython] Cr_element001  label="Cr_element : 1"  # scripted group (container) (typed FeaturePython)
  n = 1
  ref = Cr_element
FEATURE [App::DocumentObjectGroupPython] G4_Cr  # scripted group (container) (typed FeaturePython)
  Dunit = g/cm3
  Dvalue = 7.18
  Group = -> [Cr_element001]
  conduct = 2
  density = 1
  expand = 3
  formula = Cr
  name = G4_Cr
  specific = 4
FEATURE [App::DocumentObjectGroupPython] Mn_element001  label="Mn_element : 1"  # scripted group (container) (typed FeaturePython)
  n = 1
  ref = Mn_element
FEATURE [App::DocumentObjectGroupPython] G4_Mn  # scripted group (container) (typed FeaturePython)
  Dunit = g/cm3
  Dvalue = 7.44
  Group = -> [Mn_element001]
  conduct = 2
  density = 1
  expand = 3
  formula = Mn
  name = G4_Mn
  specific = 4
FEATURE [App::DocumentObjectGroupPython] Fe_element007  label="Fe_element : 004"  # scripted group (container) (typed FeaturePython)
  n = 1
  ref = Fe_element
FEATURE [App::DocumentObjectGroupPython] G4_Fe  # scripted group (container) (typed FeaturePython)
  Dunit = g/cm3
  Dvalue = 7.874
  Group = -> [Fe_element007]
  conduct = 2
  density = 1
  expand = 3
  formula = Fe
  name = G4_Fe
  specific = 4
FEATURE [App::DocumentObjectGroupPython] Co_element001  label="Co_element : 1"  # scripted group (container) (typed FeaturePython)
  n = 1
  ref = Co_element
FEATURE [App::DocumentObjectGroupPython] G4_Co  # scripted group (container) (typed FeaturePython)
  Dunit = g/cm3
  Dvalue = 8.9
  Group = -> [Co_element001]
  conduct = 2
  density = 1
  expand = 3
  formula = Co
  name = G4_Co
  specific = 4
FEATURE [App::DocumentObjectGroupPython] Ni_element001  label="Ni_element : 1"  # scripted group (container) (typed FeaturePython)
  n = 1
  ref = Ni_element
FEATURE [App::DocumentObjectGroupPython] G4_Ni  # scripted group (container) (typed FeaturePython)
  Dunit = g/cm3
  Dvalue = 8.902
  Group = -> [Ni_element001]
  conduct = 2
  density = 1
  expand = 3
  formula = Ni
  name = G4_Ni
  specific = 4
FEATURE [App::DocumentObjectGroupPython] Cu_element001  label="Cu_element : 1"  # scripted group (container) (typed FeaturePython)
  n = 1
  ref = Cu_element
FEATURE [App::DocumentObjectGroupPython] G4_Cu  # scripted group (container) (typed FeaturePython)
  Dunit = g/cm3
  Dvalue = 8.96
  Group = -> [Cu_element001]
  conduct = 2
  density = 1
  expand = 3
  formula = Cu
  name = G4_Cu
  specific = 4
FEATURE [App::DocumentObjectGroupPython] Zn_element001  label="Zn_element : 1"  # scripted group (container) (typed FeaturePython)
  n = 1
  ref = Zn_element
FEATURE [App::DocumentObjectGroupPython] G4_Zn  # scripted group (container) (typed FeaturePython)
  Dunit = g/cm3
  Dvalue = 7.133
  Group = -> [Zn_element001]
  conduct = 2
  density = 1
  expand = 3
  formula = Zn
  name = G4_Zn
  specific = 4
FEATURE [App::DocumentObjectGroupPython] Ga_element002  label="Ga_element : 002"  # scripted group (container) (typed FeaturePython)
  n = 1
  ref = Ga_element
FEATURE [App::DocumentObjectGroupPython] G4_Ga  # scripted group (container) (typed FeaturePython)
  Dunit = g/cm3
  Dvalue = 5.904
  Group = -> [Ga_element002]
  conduct = 2
  density = 1
  expand = 3
  formula = Ga
  name = G4_Ga
  specific = 4
FEATURE [App::DocumentObjectGroupPython] Ge_element002  label="Ge_element : 1"  # scripted group (container) (typed FeaturePython)
  n = 1
  ref = Ge_element
FEATURE [App::DocumentObjectGroupPython] G4_Ge  # scripted group (container) (typed FeaturePython)
  Dunit = g/cm3
  Dvalue = 5.323
  Group = -> [Ge_element002]
  conduct = 2
  density = 1
  expand = 3
  formula = Ge
  name = G4_Ge
  specific = 4
FEATURE [App::DocumentObjectGroupPython] As_element003  label="As_element : 002"  # scripted group (container) (typed FeaturePython)
  n = 1
  ref = As_element
FEATURE [App::DocumentObjectGroupPython] G4_As  # scripted group (container) (typed FeaturePython)
  Dunit = g/cm3
  Dvalue = 5.73
  Group = -> [As_element003]
  conduct = 2
  density = 1
  expand = 3
  formula = As
  name = G4_As
  specific = 4
FEATURE [App::DocumentObjectGroupPython] Se_element001  label="Se_element : 1"  # scripted group (container) (typed FeaturePython)
  n = 1
  ref = Se_element
FEATURE [App::DocumentObjectGroupPython] G4_Se  # scripted group (container) (typed FeaturePython)
  Dunit = g/cm3
  Dvalue = 4.5
  Group = -> [Se_element001]
  conduct = 2
  density = 1
  expand = 3
  formula = Se
  name = G4_Se
  specific = 4
FEATURE [App::DocumentObjectGroupPython] Br_element007  label="Br_element : 004"  # scripted group (container) (typed FeaturePython)
  n = 1
  ref = Br_element
FEATURE [App::DocumentObjectGroupPython] G4_Br  # scripted group (container) (typed FeaturePython)
  Dunit = g/cm3
  Dvalue = 0.0070721
  Group = -> [Br_element007]
  conduct = 2
  density = 1
  expand = 3
  formula = Br
  name = G4_Br
  specific = 4
FEATURE [App::DocumentObjectGroupPython] Kr_element001  label="Kr_element : 1"  # scripted group (container) (typed FeaturePython)
  n = 1
  ref = Kr_element
FEATURE [App::DocumentObjectGroupPython] G4_Kr  # scripted group (container) (typed FeaturePython)
  Dunit = g/cm3
  Dvalue = 0.00347832
  Group = -> [Kr_element001]
  conduct = 2
  density = 1
  expand = 3
  formula = Kr
  name = G4_Kr
  specific = 4
FEATURE [App::DocumentObjectGroupPython] Rb_element001  label="Rb_element : 1"  # scripted group (container) (typed FeaturePython)
  n = 1
  ref = Rb_element
FEATURE [App::DocumentObjectGroupPython] G4_Rb  # scripted group (container) (typed FeaturePython)
  Dunit = g/cm3
  Dvalue = 1.532
  Group = -> [Rb_element001]
  conduct = 2
  density = 1
  expand = 3
  formula = Rb
  name = G4_Rb
  specific = 4
FEATURE [App::DocumentObjectGroupPython] Sr_element001  label="Sr_element : 1"  # scripted group (container) (typed FeaturePython)
  n = 1
  ref = Sr_element
FEATURE [App::DocumentObjectGroupPython] G4_Sr  # scripted group (container) (typed FeaturePython)
  Dunit = g/cm3
  Dvalue = 2.54
  Group = -> [Sr_element001]
  conduct = 2
  density = 1
  expand = 3
  formula = Sr
  name = G4_Sr
  specific = 4
FEATURE [App::DocumentObjectGroupPython] Y_element001  label="Y_element : 1"  # scripted group (container) (typed FeaturePython)
  n = 1
  ref = Y_element
FEATURE [App::DocumentObjectGroupPython] G4_Y  # scripted group (container) (typed FeaturePython)
  Dunit = g/cm3
  Dvalue = 4.469
  Group = -> [Y_element001]
  conduct = 2
  density = 1
  expand = 3
  formula = Y
  name = G4_Y
  specific = 4
FEATURE [App::DocumentObjectGroupPython] Zr_element001  label="Zr_element : 1"  # scripted group (container) (typed FeaturePython)
  n = 1
  ref = Zr_element
FEATURE [App::DocumentObjectGroupPython] G4_Zr  # scripted group (container) (typed FeaturePython)
  Dunit = g/cm3
  Dvalue = 6.506
  Group = -> [Zr_element001]
  conduct = 2
  density = 1
  expand = 3
  formula = Zr
  name = G4_Zr
  specific = 4
FEATURE [App::DocumentObjectGroupPython] Nb_element001  label="Nb_element : 1"  # scripted group (container) (typed FeaturePython)
  n = 1
  ref = Nb_element
FEATURE [App::DocumentObjectGroupPython] G4_Nb  # scripted group (container) (typed FeaturePython)
  Dunit = g/cm3
  Dvalue = 8.57
  Group = -> [Nb_element001]
  conduct = 2
  density = 1
  expand = 3
  formula = Nb
  name = G4_Nb
  specific = 4
FEATURE [App::DocumentObjectGroupPython] Mo_element001  label="Mo_element : 1"  # scripted group (container) (typed FeaturePython)
  n = 1
  ref = Mo_element
FEATURE [App::DocumentObjectGroupPython] G4_Mo  # scripted group (container) (typed FeaturePython)
  Dunit = g/cm3
  Dvalue = 10.22
  Group = -> [Mo_element001]
  conduct = 2
  density = 1
  expand = 3
  formula = Mo
  name = G4_Mo
  specific = 4
FEATURE [App::DocumentObjectGroupPython] Tc_element001  label="Tc_element : 1"  # scripted group (container) (typed FeaturePython)
  n = 1
  ref = Tc_element
FEATURE [App::DocumentObjectGroupPython] G4_Tc  # scripted group (container) (typed FeaturePython)
  Dunit = g/cm3
  Dvalue = 11.5
  Group = -> [Tc_element001]
  conduct = 2
  density = 1
  expand = 3
  formula = Tc
  name = G4_Tc
  specific = 4
FEATURE [App::DocumentObjectGroupPython] Ru_element001  label="Ru_element : 1"  # scripted group (container) (typed FeaturePython)
  n = 1
  ref = Ru_element
FEATURE [App::DocumentObjectGroupPython] G4_Ru  # scripted group (container) (typed FeaturePython)
  Dunit = g/cm3
  Dvalue = 12.41
  Group = -> [Ru_element001]
  conduct = 2
  density = 1
  expand = 3
  formula = Ru
  name = G4_Ru
  specific = 4
FEATURE [App::DocumentObjectGroupPython] Rh_element001  label="Rh_element : 1"  # scripted group (container) (typed FeaturePython)
  n = 1
  ref = Rh_element
FEATURE [App::DocumentObjectGroupPython] G4_Rh  # scripted group (container) (typed FeaturePython)
  Dunit = g/cm3
  Dvalue = 12.41
  Group = -> [Rh_element001]
  conduct = 2
  density = 1
  expand = 3
  formula = Rh
  name = G4_Rh
  specific = 4
FEATURE [App::DocumentObjectGroupPython] Pd_element001  label="Pd_element : 1"  # scripted group (container) (typed FeaturePython)
  n = 1
  ref = Pd_element
FEATURE [App::DocumentObjectGroupPython] G4_Pd  # scripted group (container) (typed FeaturePython)
  Dunit = g/cm3
  Dvalue = 12.02
  Group = -> [Pd_element001]
  conduct = 2
  density = 1
  expand = 3
  formula = Pd
  name = G4_Pd
  specific = 4
FEATURE [App::DocumentObjectGroupPython] Ag_element006  label="Ag_element : 004"  # scripted group (container) (typed FeaturePython)
  n = 1
  ref = Ag_element
FEATURE [App::DocumentObjectGroupPython] G4_Ag  # scripted group (container) (typed FeaturePython)
  Dunit = g/cm3
  Dvalue = 10.5
  Group = -> [Ag_element006]
  conduct = 2
  density = 1
  expand = 3
  formula = Ag
  name = G4_Ag
  specific = 4
FEATURE [App::DocumentObjectGroupPython] Cd_element003  label="Cd_element : 003"  # scripted group (container) (typed FeaturePython)
  n = 1
  ref = Cd_element
FEATURE [App::DocumentObjectGroupPython] G4_Cd  # scripted group (container) (typed FeaturePython)
  Dunit = g/cm3
  Dvalue = 8.65
  Group = -> [Cd_element003]
  conduct = 2
  density = 1
  expand = 3
  formula = Cd
  name = G4_Cd
  specific = 4
FEATURE [App::DocumentObjectGroupPython] In_element001  label="In_element : 1"  # scripted group (container) (typed FeaturePython)
  n = 1
  ref = In_element
FEATURE [App::DocumentObjectGroupPython] G4_In  # scripted group (container) (typed FeaturePython)
  Dunit = g/cm3
  Dvalue = 7.31
  Group = -> [In_element001]
  conduct = 2
  density = 1
  expand = 3
  formula = In
  name = G4_In
  specific = 4
FEATURE [App::DocumentObjectGroupPython] Sn_element001  label="Sn_element : 1"  # scripted group (container) (typed FeaturePython)
  n = 1
  ref = Sn_element
FEATURE [App::DocumentObjectGroupPython] G4_Sn  # scripted group (container) (typed FeaturePython)
  Dunit = g/cm3
  Dvalue = 7.31
  Group = -> [Sn_element001]
  conduct = 2
  density = 1
  expand = 3
  formula = Sn
  name = G4_Sn
  specific = 4
FEATURE [App::DocumentObjectGroupPython] Sb_element001  label="Sb_element : 1"  # scripted group (container) (typed FeaturePython)
  n = 1
  ref = Sb_element
FEATURE [App::DocumentObjectGroupPython] G4_Sb  # scripted group (container) (typed FeaturePython)
  Dunit = g/cm3
  Dvalue = 6.691
  Group = -> [Sb_element001]
  conduct = 2
  density = 1
  expand = 3
  formula = Sb
  name = G4_Sb
  specific = 4
FEATURE [App::DocumentObjectGroupPython] Te_element002  label="Te_element : 002"  # scripted group (container) (typed FeaturePython)
  n = 1
  ref = Te_element
FEATURE [App::DocumentObjectGroupPython] G4_Te  # scripted group (container) (typed FeaturePython)
  Dunit = g/cm3
  Dvalue = 6.24
  Group = -> [Te_element002]
  conduct = 2
  density = 1
  expand = 3
  formula = Te
  name = G4_Te
  specific = 4
FEATURE [App::DocumentObjectGroupPython] I_element010  label="I_element : 006"  # scripted group (container) (typed FeaturePython)
  n = 1
  ref = I_element
FEATURE [App::DocumentObjectGroupPython] G4_I  # scripted group (container) (typed FeaturePython)
  Dunit = g/cm3
  Dvalue = 4.93
  Group = -> [I_element010]
  conduct = 2
  density = 1
  expand = 3
  formula = I
  name = G4_I
  specific = 4
FEATURE [App::DocumentObjectGroupPython] Xe_element001  label="Xe_element : 1"  # scripted group (container) (typed FeaturePython)
  n = 1
  ref = Xe_element
FEATURE [App::DocumentObjectGroupPython] G4_Xe  # scripted group (container) (typed FeaturePython)
  Dunit = g/cm3
  Dvalue = 0.00548536
  Group = -> [Xe_element001]
  conduct = 2
  density = 1
  expand = 3
  formula = Xe
  name = G4_Xe
  specific = 4
FEATURE [App::DocumentObjectGroupPython] Cs_element003  label="Cs_element : 003"  # scripted group (container) (typed FeaturePython)
  n = 1
  ref = Cs_element
FEATURE [App::DocumentObjectGroupPython] G4_Cs  # scripted group (container) (typed FeaturePython)
  Dunit = g/cm3
  Dvalue = 1.873
  Group = -> [Cs_element003]
  conduct = 2
  density = 1
  expand = 3
  formula = Cs
  name = G4_Cs
  specific = 4
FEATURE [App::DocumentObjectGroupPython] Ba_element003  label="Ba_element : 003"  # scripted group (container) (typed FeaturePython)
  n = 1
  ref = Ba_element
FEATURE [App::DocumentObjectGroupPython] G4_Ba  # scripted group (container) (typed FeaturePython)
  Dunit = g/cm3
  Dvalue = 3.5
  Group = -> [Ba_element003]
  conduct = 2
  density = 1
  expand = 3
  formula = Ba
  name = G4_Ba
  specific = 4
FEATURE [App::DocumentObjectGroupPython] La_element003  label="La_element : 003"  # scripted group (container) (typed FeaturePython)
  n = 1
  ref = La_element
FEATURE [App::DocumentObjectGroupPython] G4_La  # scripted group (container) (typed FeaturePython)
  Dunit = g/cm3
  Dvalue = 6.154
  Group = -> [La_element003]
  conduct = 2
  density = 1
  expand = 3
  formula = La
  name = G4_La
  specific = 4
FEATURE [App::DocumentObjectGroupPython] Ce_element002  label="Ce_element : 1"  # scripted group (container) (typed FeaturePython)
  n = 1
  ref = Ce_element
FEATURE [App::DocumentObjectGroupPython] G4_Ce  # scripted group (container) (typed FeaturePython)
  Dunit = g/cm3
  Dvalue = 6.657
  Group = -> [Ce_element002]
  conduct = 2
  density = 1
  expand = 3
  formula = Ce
  name = G4_Ce
  specific = 4
FEATURE [App::DocumentObjectGroupPython] Pr_element001  label="Pr_element : 1"  # scripted group (container) (typed FeaturePython)
  n = 1
  ref = Pr_element
FEATURE [App::DocumentObjectGroupPython] G4_Pr  # scripted group (container) (typed FeaturePython)
  Dunit = g/cm3
  Dvalue = 6.71
  Group = -> [Pr_element001]
  conduct = 2
  density = 1
  expand = 3
  formula = Pr
  name = G4_Pr
  specific = 4
FEATURE [App::DocumentObjectGroupPython] Nd_element001  label="Nd_element : 1"  # scripted group (container) (typed FeaturePython)
  n = 1
  ref = Nd_element
FEATURE [App::DocumentObjectGroupPython] G4_Nd  # scripted group (container) (typed FeaturePython)
  Dunit = g/cm3
  Dvalue = 6.9
  Group = -> [Nd_element001]
  conduct = 2
  density = 1
  expand = 3
  formula = Nd
  name = G4_Nd
  specific = 4
FEATURE [App::DocumentObjectGroupPython] Pm_element001  label="Pm_element : 1"  # scripted group (container) (typed FeaturePython)
  n = 1
  ref = Pm_element
FEATURE [App::DocumentObjectGroupPython] G4_Pm  # scripted group (container) (typed FeaturePython)
  Dunit = g/cm3
  Dvalue = 7.22
  Group = -> [Pm_element001]
  conduct = 2
  density = 1
  expand = 3
  formula = Pm
  name = G4_Pm
  specific = 4
FEATURE [App::DocumentObjectGroupPython] Sm_element001  label="Sm_element : 1"  # scripted group (container) (typed FeaturePython)
  n = 1
  ref = Sm_element
FEATURE [App::DocumentObjectGroupPython] G4_Sm  # scripted group (container) (typed FeaturePython)
  Dunit = g/cm3
  Dvalue = 7.46
  Group = -> [Sm_element001]
  conduct = 2
  density = 1
  expand = 3
  formula = Sm
  name = G4_Sm
  specific = 4
FEATURE [App::DocumentObjectGroupPython] Eu_element001  label="Eu_element : 1"  # scripted group (container) (typed FeaturePython)
  n = 1
  ref = Eu_element
FEATURE [App::DocumentObjectGroupPython] G4_Eu  # scripted group (container) (typed FeaturePython)
  Dunit = g/cm3
  Dvalue = 5.243
  Group = -> [Eu_element001]
  conduct = 2
  density = 1
  expand = 3
  formula = Eu
  name = G4_Eu
  specific = 4
FEATURE [App::DocumentObjectGroupPython] Gd_element002  label="Gd_element : 1"  # scripted group (container) (typed FeaturePython)
  n = 1
  ref = Gd_element
FEATURE [App::DocumentObjectGroupPython] G4_Gd  # scripted group (container) (typed FeaturePython)
  Dunit = g/cm3
  Dvalue = 7.9004
  Group = -> [Gd_element002]
  conduct = 2
  density = 1
  expand = 3
  formula = Gd
  name = G4_Gd
  specific = 4
FEATURE [App::DocumentObjectGroupPython] Tb_element001  label="Tb_element : 1"  # scripted group (container) (typed FeaturePython)
  n = 1
  ref = Tb_element
FEATURE [App::DocumentObjectGroupPython] G4_Tb  # scripted group (container) (typed FeaturePython)
  Dunit = g/cm3
  Dvalue = 8.229
  Group = -> [Tb_element001]
  conduct = 2
  density = 1
  expand = 3
  formula = Tb
  name = G4_Tb
  specific = 4
FEATURE [App::DocumentObjectGroupPython] Dy_element001  label="Dy_element : 1"  # scripted group (container) (typed FeaturePython)
  n = 1
  ref = Dy_element
FEATURE [App::DocumentObjectGroupPython] G4_Dy  # scripted group (container) (typed FeaturePython)
  Dunit = g/cm3
  Dvalue = 8.55
  Group = -> [Dy_element001]
  conduct = 2
  density = 1
  expand = 3
  formula = Dy
  name = G4_Dy
  specific = 4
FEATURE [App::DocumentObjectGroupPython] Ho_element001  label="Ho_element : 1"  # scripted group (container) (typed FeaturePython)
  n = 1
  ref = Ho_element
FEATURE [App::DocumentObjectGroupPython] G4_Ho  # scripted group (container) (typed FeaturePython)
  Dunit = g/cm3
  Dvalue = 8.795
  Group = -> [Ho_element001]
  conduct = 2
  density = 1
  expand = 3
  formula = Ho
  name = G4_Ho
  specific = 4
FEATURE [App::DocumentObjectGroupPython] Er_element001  label="Er_element : 1"  # scripted group (container) (typed FeaturePython)
  n = 1
  ref = Er_element
FEATURE [App::DocumentObjectGroupPython] G4_Er  # scripted group (container) (typed FeaturePython)
  Dunit = g/cm3
  Dvalue = 9.066
  Group = -> [Er_element001]
  conduct = 2
  density = 1
  expand = 3
  formula = Er
  name = G4_Er
  specific = 4
FEATURE [App::DocumentObjectGroupPython] Tm_element001  label="Tm_element : 1"  # scripted group (container) (typed FeaturePython)
  n = 1
  ref = Tm_element
FEATURE [App::DocumentObjectGroupPython] G4_Tm  # scripted group (container) (typed FeaturePython)
  Dunit = g/cm3
  Dvalue = 9.321
  Group = -> [Tm_element001]
  conduct = 2
  density = 1
  expand = 3
  formula = Tm
  name = G4_Tm
  specific = 4
FEATURE [App::DocumentObjectGroupPython] Yb_element001  label="Yb_element : 1"  # scripted group (container) (typed FeaturePython)
  n = 1
  ref = Yb_element
FEATURE [App::DocumentObjectGroupPython] G4_Yb  # scripted group (container) (typed FeaturePython)
  Dunit = g/cm3
  Dvalue = 6.73
  Group = -> [Yb_element001]
  conduct = 2
  density = 1
  expand = 3
  formula = Yb
  name = G4_Yb
  specific = 4
FEATURE [App::DocumentObjectGroupPython] Lu_element001  label="Lu_element : 1"  # scripted group (container) (typed FeaturePython)
  n = 1
  ref = Lu_element
FEATURE [App::DocumentObjectGroupPython] G4_Lu  # scripted group (container) (typed FeaturePython)
  Dunit = g/cm3
  Dvalue = 9.84
  Group = -> [Lu_element001]
  conduct = 2
  density = 1
  expand = 3
  formula = Lu
  name = G4_Lu
  specific = 4
FEATURE [App::DocumentObjectGroupPython] Hf_element001  label="Hf_element : 1"  # scripted group (container) (typed FeaturePython)
  n = 1
  ref = Hf_element
FEATURE [App::DocumentObjectGroupPython] G4_Hf  # scripted group (container) (typed FeaturePython)
  Dunit = g/cm3
  Dvalue = 13.31
  Group = -> [Hf_element001]
  conduct = 2
  density = 1
  expand = 3
  formula = Hf
  name = G4_Hf
  specific = 4
FEATURE [App::DocumentObjectGroupPython] Ta_element001  label="Ta_element : 1"  # scripted group (container) (typed FeaturePython)
  n = 1
  ref = Ta_element
FEATURE [App::DocumentObjectGroupPython] G4_Ta  # scripted group (container) (typed FeaturePython)
  Dunit = g/cm3
  Dvalue = 16.654
  Group = -> [Ta_element001]
  conduct = 2
  density = 1
  expand = 3
  formula = Ta
  name = G4_Ta
  specific = 4
FEATURE [App::DocumentObjectGroupPython] W_element004  label="W_element : 004"  # scripted group (container) (typed FeaturePython)
  n = 1
  ref = W_element
FEATURE [App::DocumentObjectGroupPython] G4_W  # scripted group (container) (typed FeaturePython)
  Dunit = g/cm3
  Dvalue = 19.3
  Group = -> [W_element004]
  conduct = 2
  density = 1
  expand = 3
  formula = W
  name = G4_W
  specific = 4
FEATURE [App::DocumentObjectGroupPython] Re_element001  label="Re_element : 1"  # scripted group (container) (typed FeaturePython)
  n = 1
  ref = Re_element
FEATURE [App::DocumentObjectGroupPython] G4_Re  # scripted group (container) (typed FeaturePython)
  Dunit = g/cm3
  Dvalue = 21.02
  Group = -> [Re_element001]
  conduct = 2
  density = 1
  expand = 3
  formula = Re
  name = G4_Re
  specific = 4
FEATURE [App::DocumentObjectGroupPython] Os_element001  label="Os_element : 1"  # scripted group (container) (typed FeaturePython)
  n = 1
  ref = Os_element
FEATURE [App::DocumentObjectGroupPython] G4_Os  # scripted group (container) (typed FeaturePython)
  Dunit = g/cm3
  Dvalue = 22.57
  Group = -> [Os_element001]
  conduct = 2
  density = 1
  expand = 3
  formula = Os
  name = G4_Os
  specific = 4
FEATURE [App::DocumentObjectGroupPython] Ir_element001  label="Ir_element : 1"  # scripted group (container) (typed FeaturePython)
  n = 1
  ref = Ir_element
FEATURE [App::DocumentObjectGroupPython] G4_Ir  # scripted group (container) (typed FeaturePython)
  Dunit = g/cm3
  Dvalue = 22.42
  Group = -> [Ir_element001]
  conduct = 2
  density = 1
  expand = 3
  formula = Ir
  name = G4_Ir
  specific = 4
FEATURE [App::DocumentObjectGroupPython] Pt_element001  label="Pt_element : 1"  # scripted group (container) (typed FeaturePython)
  n = 1
  ref = Pt_element
FEATURE [App::DocumentObjectGroupPython] G4_Pt  # scripted group (container) (typed FeaturePython)
  Dunit = g/cm3
  Dvalue = 21.45
  Group = -> [Pt_element001]
  conduct = 2
  density = 1
  expand = 3
  formula = Pt
  name = G4_Pt
  specific = 4
FEATURE [App::DocumentObjectGroupPython] Au_element001  label="Au_element : 1"  # scripted group (container) (typed FeaturePython)
  n = 1
  ref = Au_element
FEATURE [App::DocumentObjectGroupPython] G4_Au  # scripted group (container) (typed FeaturePython)
  Dunit = g/cm3
  Dvalue = 19.32
  Group = -> [Au_element001]
  conduct = 2
  density = 1
  expand = 3
  formula = Au
  name = G4_Au
  specific = 4
FEATURE [App::DocumentObjectGroupPython] Hg_element002  label="Hg_element : 002"  # scripted group (container) (typed FeaturePython)
  n = 1
  ref = Hg_element
FEATURE [App::DocumentObjectGroupPython] G4_Hg  # scripted group (container) (typed FeaturePython)
  Dunit = g/cm3
  Dvalue = 13.546
  Group = -> [Hg_element002]
  conduct = 2
  density = 1
  expand = 3
  formula = Hg
  name = G4_Hg
  specific = 4
FEATURE [App::DocumentObjectGroupPython] Tl_element002  label="Tl_element : 002"  # scripted group (container) (typed FeaturePython)
  n = 1
  ref = Tl_element
FEATURE [App::DocumentObjectGroupPython] G4_Tl  # scripted group (container) (typed FeaturePython)
  Dunit = g/cm3
  Dvalue = 11.72
  Group = -> [Tl_element002]
  conduct = 2
  density = 1
  expand = 3
  formula = Tl
  name = G4_Tl
  specific = 4
FEATURE [App::DocumentObjectGroupPython] Pb_element003  label="Pb_element : 1"  # scripted group (container) (typed FeaturePython)
  n = 1
  ref = Pb_element
FEATURE [App::DocumentObjectGroupPython] G4_Pb  # scripted group (container) (typed FeaturePython)
  Dunit = g/cm3
  Dvalue = 11.35
  Group = -> [Pb_element003]
  conduct = 2
  density = 1
  expand = 3
  formula = Pb
  name = G4_Pb
  specific = 4
FEATURE [App::DocumentObjectGroupPython] Bi_element002  label="Bi_element : 1"  # scripted group (container) (typed FeaturePython)
  n = 1
  ref = Bi_element
FEATURE [App::DocumentObjectGroupPython] G4_Bi  # scripted group (container) (typed FeaturePython)
  Dunit = g/cm3
  Dvalue = 9.747
  Group = -> [Bi_element002]
  conduct = 2
  density = 1
  expand = 3
  formula = Bi
  name = G4_Bi
  specific = 4
FEATURE [App::DocumentObjectGroupPython] Po_element001  label="Po_element : 1"  # scripted group (container) (typed FeaturePython)
  n = 1
  ref = Po_element
FEATURE [App::DocumentObjectGroupPython] G4_Po  # scripted group (container) (typed FeaturePython)
  Dunit = g/cm3
  Dvalue = 9.32
  Group = -> [Po_element001]
  conduct = 2
  density = 1
  expand = 3
  formula = Po
  name = G4_Po
  specific = 4
FEATURE [App::DocumentObjectGroupPython] At_element001  label="At_element : 1"  # scripted group (container) (typed FeaturePython)
  n = 1
  ref = At_element
FEATURE [App::DocumentObjectGroupPython] G4_At  # scripted group (container) (typed FeaturePython)
  Dunit = g/cm3
  Dvalue = 9.32
  Group = -> [At_element001]
  conduct = 2
  density = 1
  expand = 3
  formula = At
  name = G4_At
  specific = 4
FEATURE [App::DocumentObjectGroupPython] Rn_element001  label="Rn_element : 1"  # scripted group (container) (typed FeaturePython)
  n = 1
  ref = Rn_element
FEATURE [App::DocumentObjectGroupPython] G4_Rn  # scripted group (container) (typed FeaturePython)
  Dunit = g/cm3
  Dvalue = 0.00900662
  Group = -> [Rn_element001]
  conduct = 2
  density = 1
  expand = 3
  formula = Rn
  name = G4_Rn
  specific = 4
FEATURE [App::DocumentObjectGroupPython] Fr_element001  label="Fr_element : 1"  # scripted group (container) (typed FeaturePython)
  n = 1
  ref = Fr_element
FEATURE [App::DocumentObjectGroupPython] G4_Fr  # scripted group (container) (typed FeaturePython)
  Dunit = g/cm3
  Dvalue = 1
  Group = -> [Fr_element001]
  conduct = 2
  density = 1
  expand = 3
  formula = Fr
  name = G4_Fr
  specific = 4
FEATURE [App::DocumentObjectGroupPython] Ra_element001  label="Ra_element : 1"  # scripted group (container) (typed FeaturePython)
  n = 1
  ref = Ra_element
FEATURE [App::DocumentObjectGroupPython] G4_Ra  # scripted group (container) (typed FeaturePython)
  Dunit = g/cm3
  Dvalue = 5
  Group = -> [Ra_element001]
  conduct = 2
  density = 1
  expand = 3
  formula = Ra
  name = G4_Ra
  specific = 4
FEATURE [App::DocumentObjectGroupPython] Ac_element001  label="Ac_element : 1"  # scripted group (container) (typed FeaturePython)
  n = 1
  ref = Ac_element
FEATURE [App::DocumentObjectGroupPython] G4_Ac  # scripted group (container) (typed FeaturePython)
  Dunit = g/cm3
  Dvalue = 10.07
  Group = -> [Ac_element001]
  conduct = 2
  density = 1
  expand = 3
  formula = Ac
  name = G4_Ac
  specific = 4
FEATURE [App::DocumentObjectGroupPython] Th_element001  label="Th_element : 1"  # scripted group (container) (typed FeaturePython)
  n = 1
  ref = Th_element
FEATURE [App::DocumentObjectGroupPython] G4_Th  # scripted group (container) (typed FeaturePython)
  Dunit = g/cm3
  Dvalue = 11.72
  Group = -> [Th_element001]
  conduct = 2
  density = 1
  expand = 3
  formula = Th
  name = G4_Th
  specific = 4
FEATURE [App::DocumentObjectGroupPython] Pa_element001  label="Pa_element : 1"  # scripted group (container) (typed FeaturePython)
  n = 1
  ref = Pa_element
FEATURE [App::DocumentObjectGroupPython] G4_Pa  # scripted group (container) (typed FeaturePython)
  Dunit = g/cm3
  Dvalue = 15.37
  Group = -> [Pa_element001]
  conduct = 2
  density = 1
  expand = 3
  formula = Pa
  name = G4_Pa
  specific = 4
FEATURE [App::DocumentObjectGroupPython] U_element004  label="U_element : 004"  # scripted group (container) (typed FeaturePython)
  n = 1
  ref = U_element
FEATURE [App::DocumentObjectGroupPython] G4_U  # scripted group (container) (typed FeaturePython)
  Dunit = g/cm3
  Dvalue = 18.95
  Group = -> [U_element004]
  conduct = 2
  density = 1
  expand = 3
  formula = U
  name = G4_U
  specific = 4
FEATURE [App::DocumentObjectGroupPython] Np_element001  label="Np_element : 1"  # scripted group (container) (typed FeaturePython)
  n = 1
  ref = Np_element
FEATURE [App::DocumentObjectGroupPython] G4_Np  # scripted group (container) (typed FeaturePython)
  Dunit = g/cm3
  Dvalue = 20.25
  Group = -> [Np_element001]
  conduct = 2
  density = 1
  expand = 3
  formula = Np
  name = G4_Np
  specific = 4
FEATURE [App::DocumentObjectGroupPython] Pu_element002  label="Pu_element : 002"  # scripted group (container) (typed FeaturePython)
  n = 1
  ref = Pu_element
FEATURE [App::DocumentObjectGroupPython] G4_Pu  # scripted group (container) (typed FeaturePython)
  Dunit = g/cm3
  Dvalue = 19.84
  Group = -> [Pu_element002]
  conduct = 2
  density = 1
  expand = 3
  formula = Pu
  name = G4_Pu
  specific = 4
FEATURE [App::DocumentObjectGroupPython] Am_element001  label="Am_element : 1"  # scripted group (container) (typed FeaturePython)
  n = 1
  ref = Am_element
FEATURE [App::DocumentObjectGroupPython] G4_Am  # scripted group (container) (typed FeaturePython)
  Dunit = g/cm3
  Dvalue = 13.67
  Group = -> [Am_element001]
  conduct = 2
  density = 1
  expand = 3
  formula = Am
  name = G4_Am
  specific = 4
FEATURE [App::DocumentObjectGroupPython] Cm_element001  label="Cm_element : 1"  # scripted group (container) (typed FeaturePython)
  n = 1
  ref = Cm_element
FEATURE [App::DocumentObjectGroupPython] G4_Cm  # scripted group (container) (typed FeaturePython)
  Dunit = g/cm3
  Dvalue = 13.51
  Group = -> [Cm_element001]
  conduct = 2
  density = 1
  expand = 3
  formula = Cm
  name = G4_Cm
  specific = 4
FEATURE [App::DocumentObjectGroupPython] Bk_element001  label="Bk_element : 1"  # scripted group (container) (typed FeaturePython)
  n = 1
  ref = Bk_element
FEATURE [App::DocumentObjectGroupPython] G4_Bk  # scripted group (container) (typed FeaturePython)
  Dunit = g/cm3
  Dvalue = 14
  Group = -> [Bk_element001]
  conduct = 2
  density = 1
  expand = 3
  formula = Bk
  name = G4_Bk
  specific = 4
FEATURE [App::DocumentObjectGroupPython] Cf_element001  label="Cf_element : 1"  # scripted group (container) (typed FeaturePython)
  n = 1
  ref = Cf_element
FEATURE [App::DocumentObjectGroupPython] G4_Cf  # scripted group (container) (typed FeaturePython)
  Dunit = g/cm3
  Dvalue = 10
  Group = -> [Cf_element001]
  conduct = 2
  density = 1
  expand = 3
  formula = Cf
  name = G4_Cf
  specific = 4
FEATURE [App::DocumentObjectGroupPython] Element  # scripted group (container) (typed FeaturePython)
  Group = -> [G4_H,G4_He,G4_Li,G4_Be,G4_B,G4_C,G4_N,G4_O,G4_F,G4_Ne,G4_Na,G4_Mg,G4_Al,G4_Si,G4_P,G4_S,G4_Cl,G4_Ar,G4_K,G4_Ca,G4_Sc,G4_Ti,G4_V,G4_Cr,G4_Mn,G4_Fe,G4_Co,G4_Ni,G4_Cu,G4_Zn,G4_Ga,G4_Ge,G4_As,G4_Se,G4_Br,G4_Kr,G4_Rb,G4_Sr,G4_Y,G4_Zr,G4_Nb,G4_Mo,G4_Tc,G4_Ru,G4_Rh,G4_Pd,G4_Ag,G4_Cd,G4_In,G4_Sn,G4_Sb,G4_Te,G4_I,G4_Xe,G4_Cs,G4_Ba,G4_La,G4_Ce,G4_Pr,G4_Nd,G4_Pm,G4_Sm,G4_Eu,G4_Gd,G4_Tb,G4_Dy,G4_Ho,G4_Er,+30 more]
FEATURE [App::DocumentObjectGroupPython] H_element114  label="H_element : 063"  # scripted group (container) (typed FeaturePython)
  n = 2
  ref = H_element
FEATURE [App::DocumentObjectGroupPython] G4_lH2  # scripted group (container) (typed FeaturePython)
  Dunit = g/cm3
  Dvalue = 0.0708
  Group = -> [H_element114]
  conduct = 2
  density = 1
  expand = 3
  formula = G4_lH2
  name = G4_lH2
  specific = 4
FEATURE [App::DocumentObjectGroupPython] N_element049  label="N_element : 022"  # scripted group (container) (typed FeaturePython)
  n = 2
  ref = N_element
FEATURE [App::DocumentObjectGroupPython] G4_lN2  # scripted group (container) (typed FeaturePython)
  Dunit = g/cm3
  Dvalue = 0.807
  Group = -> [N_element049]
  conduct = 2
  density = 1
  expand = 3
  formula = G4_lN2
  name = G4_lN2
  specific = 4
FEATURE [App::DocumentObjectGroupPython] O_element106  label="O_element : 060"  # scripted group (container) (typed FeaturePython)
  n = 2
  ref = O_element
FEATURE [App::DocumentObjectGroupPython] G4_lO2  # scripted group (container) (typed FeaturePython)
  Dunit = g/cm3
  Dvalue = 1.141
  Group = -> [O_element106]
  conduct = 2
  density = 1
  expand = 3
  formula = G4_lO2
  name = G4_lO2
  specific = 4
FEATURE [App::DocumentObjectGroupPython] Ar  label="Ar : 1"  # scripted group (container) (typed FeaturePython)
  n = 1
  ref = Ar
FEATURE [App::DocumentObjectGroupPython] G4_lAr  # scripted group (container) (typed FeaturePython)
  Dunit = g/cm3
  Dvalue = 1.396
  Group = -> [Ar]
  conduct = 2
  density = 1
  expand = 3
  formula = G4_lAr
  name = G4_lAr
  specific = 4
FEATURE [App::DocumentObjectGroupPython] Br  label="Br : 1"  # scripted group (container) (typed FeaturePython)
  n = 1
  ref = Br
FEATURE [App::DocumentObjectGroupPython] G4_lBr  # scripted group (container) (typed FeaturePython)
  Dunit = g/cm3
  Dvalue = 3.1028
  Group = -> [Br]
  conduct = 2
  density = 1
  expand = 3
  formula = G4_lBr
  name = G4_lBr
  specific = 4
FEATURE [App::DocumentObjectGroupPython] Kr  label="Kr : 1"  # scripted group (container) (typed FeaturePython)
  n = 1
  ref = Kr
FEATURE [App::DocumentObjectGroupPython] G4_lKr  # scripted group (container) (typed FeaturePython)
  Dunit = g/cm3
  Dvalue = 2.418
  Group = -> [Kr]
  conduct = 2
  density = 1
  expand = 3
  formula = G4_lKr
  name = G4_lKr
  specific = 4
FEATURE [App::DocumentObjectGroupPython] Xe  label="Xe : 1"  # scripted group (container) (typed FeaturePython)
  n = 1
  ref = Xe
FEATURE [App::DocumentObjectGroupPython] G4_lXe  # scripted group (container) (typed FeaturePython)
  Dunit = g/cm3
  Dvalue = 2.953
  Group = -> [Xe]
  conduct = 2
  density = 1
  expand = 3
  formula = G4_lXe
  name = G4_lXe
  specific = 4
FEATURE [App::DocumentObjectGroupPython] O_element107  label="O_element : 061"  # scripted group (container) (typed FeaturePython)
  n = 4
  ref = O_element
FEATURE [App::DocumentObjectGroupPython] Pb_element004  label="Pb_element : 002"  # scripted group (container) (typed FeaturePython)
  n = 1
  ref = Pb_element
FEATURE [App::DocumentObjectGroupPython] W_element005  label="W_element : 005"  # scripted group (container) (typed FeaturePython)
  n = 1
  ref = W_element
FEATURE [App::DocumentObjectGroupPython] G4_PbWO4  # scripted group (container) (typed FeaturePython)
  Dunit = g/cm3
  Dvalue = 8.28
  Group = -> [O_element107,Pb_element004,W_element005]
  conduct = 2
  density = 1
  expand = 3
  formula = G4_PbWO4
  name = G4_PbWO4
  specific = 4
FEATURE [App::DocumentObjectGroupPython] alactic  label="alactic : 1"  # scripted group (container) (typed FeaturePython)
  n = 1
  ref = alactic
FEATURE [App::DocumentObjectGroupPython] G4_Galactic  # scripted group (container) (typed FeaturePython)
  Dunit = g/cm3
  Dvalue = 0
  Group = -> [alactic]
  conduct = 2
  density = 1
  expand = 3
  formula = G4_Galactic
  name = G4_Galactic
  specific = 4
FEATURE [App::DocumentObjectGroupPython] RAPHITE_POROUS  label="RAPHITE_POROUS : 1"  # scripted group (container) (typed FeaturePython)
  n = 1
  ref = RAPHITE_POROUS
FEATURE [App::DocumentObjectGroupPython] G4_GRAPHITE_POROUS  # scripted group (container) (typed FeaturePython)
  Dunit = g/cm3
  Dvalue = 1.7
  Group = -> [RAPHITE_POROUS]
  conduct = 2
  density = 1
  expand = 3
  formula = G4_GRAPHITE_POROUS
  name = G4_GRAPHITE_POROUS
  specific = 4
FEATURE [App::DocumentObjectGroupPython] H_element115  label="H_element : 0.150"  # scripted group (container) (typed FeaturePython)
  n = 0.080538
FEATURE [App::DocumentObjectGroupPython] C_element125  label="C_element : 0.600"  # scripted group (container) (typed FeaturePython)
  n = 0.599848
FEATURE [App::DocumentObjectGroupPython] O_element108  label="O_element : 0.320"  # scripted group (container) (typed FeaturePython)
  n = 0.319614
FEATURE [App::DocumentObjectGroupPython] G4_LUCITE  # scripted group (container) (typed FeaturePython)
  Dunit = g/cm3
  Dvalue = 1.19
  Group = -> [H_element115,C_element125,O_element108]
  conduct = 2
  density = 1
  expand = 3
  formula = G4_LUCITE
  name = G4_LUCITE
  specific = 4
FEATURE [App::DocumentObjectGroupPython] Cu_element002  label="Cu_element : 62"  # scripted group (container) (typed FeaturePython)
  n = 62
  ref = Cu_element
FEATURE [App::DocumentObjectGroupPython] Zn_element002  label="Zn_element : 35"  # scripted group (container) (typed FeaturePython)
  n = 35
  ref = Zn_element
FEATURE [App::DocumentObjectGroupPython] Pb_element005  label="Pb_element : 3"  # scripted group (container) (typed FeaturePython)
  n = 3
  ref = Pb_element
FEATURE [App::DocumentObjectGroupPython] G4_BRASS  # scripted group (container) (typed FeaturePython)
  Dunit = g/cm3
  Dvalue = 8.52
  Group = -> [Cu_element002,Zn_element002,Pb_element005]
  conduct = 2
  density = 1
  expand = 3
  formula = G4_BRASS
  name = G4_BRASS
  specific = 4
FEATURE [App::DocumentObjectGroupPython] Cu_element003  label="Cu_element : 89"  # scripted group (container) (typed FeaturePython)
  n = 89
  ref = Cu_element
FEATURE [App::DocumentObjectGroupPython] Zn_element003  label="Zn_element : 9"  # scripted group (container) (typed FeaturePython)
  n = 9
  ref = Zn_element
FEATURE [App::DocumentObjectGroupPython] Pb_element006  label="Pb_element : 2"  # scripted group (container) (typed FeaturePython)
  n = 2
  ref = Pb_element
FEATURE [App::DocumentObjectGroupPython] G4_BRONZE  # scripted group (container) (typed FeaturePython)
  Dunit = g/cm3
  Dvalue = 8.82
  Group = -> [Cu_element003,Zn_element003,Pb_element006]
  conduct = 2
  density = 1
  expand = 3
  formula = G4_BRONZE
  name = G4_BRONZE
  specific = 4
FEATURE [App::DocumentObjectGroupPython] Fe_element008  label="Fe_element : 74"  # scripted group (container) (typed FeaturePython)
  n = 74
  ref = Fe_element
FEATURE [App::DocumentObjectGroupPython] Cr_element002  label="Cr_element : 18"  # scripted group (container) (typed FeaturePython)
  n = 18
  ref = Cr_element
FEATURE [App::DocumentObjectGroupPython] Ni_element002  label="Ni_element : 8"  # scripted group (container) (typed FeaturePython)
  n = 8
  ref = Ni_element
FEATURE [App::DocumentObjectGroupPython] G4_STAINLESS_STEEL  label="G4_STAINLESS-STEEL"  # scripted group (container) (typed FeaturePython)
  Dunit = g/cm3
  Dvalue = 8
  Group = -> [Fe_element008,Cr_element002,Ni_element002]
  conduct = 2
  density = 1
  expand = 3
  formula = G4_STAINLESS-STEEL
  name = G4_STAINLESS-STEEL
  specific = 4
FEATURE [App::DocumentObjectGroupPython] H_element116  label="H_element : 064"  # scripted group (container) (typed FeaturePython)
  n = 18
  ref = H_element
FEATURE [App::DocumentObjectGroupPython] C_element126  label="C_element : 071"  # scripted group (container) (typed FeaturePython)
  n = 12
  ref = C_element
FEATURE [App::DocumentObjectGroupPython] O_element109  label="O_element : 062"  # scripted group (container) (typed FeaturePython)
  n = 7
  ref = O_element
FEATURE [App::DocumentObjectGroupPython] G4_CR39  # scripted group (container) (typed FeaturePython)
  Dunit = g/cm3
  Dvalue = 1.32
  Group = -> [H_element116,C_element126,O_element109]
  conduct = 2
  density = 1
  expand = 3
  formula = G4_CR39
  name = G4_CR39
  specific = 4
FEATURE [App::DocumentObjectGroupPython] H_element117  label="H_element : 38"  # scripted group (container) (typed FeaturePython)
  n = 38
  ref = H_element
FEATURE [App::DocumentObjectGroupPython] C_element127  label="C_element : 072"  # scripted group (container) (typed FeaturePython)
  n = 18
  ref = C_element
FEATURE [App::DocumentObjectGroupPython] O_element110  label="O_element : 063"  # scripted group (container) (typed FeaturePython)
  n = 1
  ref = O_element
FEATURE [App::DocumentObjectGroupPython] G4_OCTADECANOL  # scripted group (container) (typed FeaturePython)
  Dunit = g/cm3
  Dvalue = 0.812
  Group = -> [H_element117,C_element127,O_element110]
  conduct = 2
  density = 1
  expand = 3
  formula = G4_OCTADECANOL
  name = G4_OCTADECANOL
  specific = 4
FEATURE [App::DocumentObjectGroupPython] HEP  # scripted group (container) (typed FeaturePython)
  Group = -> [G4_lH2,G4_lN2,G4_lO2,G4_lAr,G4_lBr,G4_lKr,G4_lXe,G4_PbWO4,G4_Galactic,G4_GRAPHITE_POROUS,G4_LUCITE,G4_BRASS,G4_BRONZE,G4_STAINLESS_STEEL,G4_CR39,G4_OCTADECANOL]
FEATURE [App::DocumentObjectGroupPython] C_element128  label="C_element : 073"  # scripted group (container) (typed FeaturePython)
  n = 14
  ref = C_element
FEATURE [App::DocumentObjectGroupPython] H_element118  label="H_element : 065"  # scripted group (container) (typed FeaturePython)
  n = 10
  ref = H_element
FEATURE [App::DocumentObjectGroupPython] O_element111  label="O_element : 064"  # scripted group (container) (typed FeaturePython)
  n = 2
  ref = O_element
FEATURE [App::DocumentObjectGroupPython] N_element050  label="N_element : 023"  # scripted group (container) (typed FeaturePython)
  n = 2
  ref = N_element
FEATURE [App::DocumentObjectGroupPython] G4_KEVLAR  # scripted group (container) (typed FeaturePython)
  Dunit = g/cm3
  Dvalue = 1.44
  Group = -> [C_element128,H_element118,O_element111,N_element050]
  conduct = 2
  density = 1
  expand = 3
  formula = G4_KEVLAR
  name = G4_KEVLAR
  specific = 4
FEATURE [App::DocumentObjectGroupPython] C_element129  label="C_element : 074"  # scripted group (container) (typed FeaturePython)
  n = 10
  ref = C_element
FEATURE [App::DocumentObjectGroupPython] H_element119  label="H_element : 066"  # scripted group (container) (typed FeaturePython)
  n = 8
  ref = H_element
FEATURE [App::DocumentObjectGroupPython] O_element112  label="O_element : 065"  # scripted group (container) (typed FeaturePython)
  n = 4
  ref = O_element
FEATURE [App::DocumentObjectGroupPython] G4_DACRON  # scripted group (container) (typed FeaturePython)
  Dunit = g/cm3
  Dvalue = 1.4
  Group = -> [C_element129,H_element119,O_element112]
  conduct = 2
  density = 1
  expand = 3
  formula = G4_DACRON
  name = G4_DACRON
  specific = 4
FEATURE [App::DocumentObjectGroupPython] C_element130  label="C_element : 075"  # scripted group (container) (typed FeaturePython)
  n = 4
  ref = C_element
FEATURE [App::DocumentObjectGroupPython] H_element120  label="H_element : 067"  # scripted group (container) (typed FeaturePython)
  n = 5
  ref = H_element
FEATURE [App::DocumentObjectGroupPython] Cl_element030  label="Cl_element : 016"  # scripted group (container) (typed FeaturePython)
  n = 1
  ref = Cl_element
FEATURE [App::DocumentObjectGroupPython] G4_NEOPRENE  # scripted group (container) (typed FeaturePython)
  Dunit = g/cm3
  Dvalue = 1.23
  Group = -> [C_element130,H_element120,Cl_element030]
  conduct = 2
  density = 1
  expand = 3
  formula = G4_NEOPRENE
  name = G4_NEOPRENE
  specific = 4
FEATURE [App::DocumentObjectGroupPython] Space  # scripted group (container) (typed FeaturePython)
  Group = -> [G4_KEVLAR,G4_DACRON,G4_NEOPRENE]
FEATURE [App::DocumentObjectGroupPython] H_element121  label="H_element : 068"  # scripted group (container) (typed FeaturePython)
  n = 5
  ref = H_element
FEATURE [App::DocumentObjectGroupPython] C_element131  label="C_element : 076"  # scripted group (container) (typed FeaturePython)
  n = 4
  ref = C_element
FEATURE [App::DocumentObjectGroupPython] N_element051  label="N_element : 3"  # scripted group (container) (typed FeaturePython)
  n = 3
  ref = N_element
FEATURE [App::DocumentObjectGroupPython] O_element113  label="O_element : 066"  # scripted group (container) (typed FeaturePython)
  n = 1
  ref = O_element
FEATURE [App::DocumentObjectGroupPython] G4_CYTOSINE  # scripted group (container) (typed FeaturePython)
  Dunit = g/cm3
  Dvalue = 1.55
  Group = -> [H_element121,C_element131,N_element051,O_element113]
  conduct = 2
  density = 1
  expand = 3
  formula = G4_CYTOSINE
  name = G4_CYTOSINE
  specific = 4
FEATURE [App::DocumentObjectGroupPython] H_element122  label="H_element : 069"  # scripted group (container) (typed FeaturePython)
  n = 6
  ref = H_element
FEATURE [App::DocumentObjectGroupPython] C_element132  label="C_element : 077"  # scripted group (container) (typed FeaturePython)
  n = 5
  ref = C_element
FEATURE [App::DocumentObjectGroupPython] N_element052  label="N_element : 024"  # scripted group (container) (typed FeaturePython)
  n = 2
  ref = N_element
FEATURE [App::DocumentObjectGroupPython] O_element114  label="O_element : 067"  # scripted group (container) (typed FeaturePython)
  n = 2
  ref = O_element
FEATURE [App::DocumentObjectGroupPython] G4_THYMINE  # scripted group (container) (typed FeaturePython)
  Dunit = g/cm3
  Dvalue = 1.23
  Group = -> [H_element122,C_element132,N_element052,O_element114]
  conduct = 2
  density = 1
  expand = 3
  formula = G4_THYMINE
  name = G4_THYMINE
  specific = 4
FEATURE [App::DocumentObjectGroupPython] H_element123  label="H_element : 070"  # scripted group (container) (typed FeaturePython)
  n = 4
  ref = H_element
FEATURE [App::DocumentObjectGroupPython] C_element133  label="C_element : 078"  # scripted group (container) (typed FeaturePython)
  n = 4
  ref = C_element
FEATURE [App::DocumentObjectGroupPython] N_element053  label="N_element : 025"  # scripted group (container) (typed FeaturePython)
  n = 2
  ref = N_element
FEATURE [App::DocumentObjectGroupPython] O_element115  label="O_element : 068"  # scripted group (container) (typed FeaturePython)
  n = 2
  ref = O_element
FEATURE [App::DocumentObjectGroupPython] G4_URACIL  # scripted group (container) (typed FeaturePython)
  Dunit = g/cm3
  Dvalue = 1.32
  Group = -> [H_element123,C_element133,N_element053,O_element115]
  conduct = 2
  density = 1
  expand = 3
  formula = G4_URACIL
  name = G4_URACIL
  specific = 4
FEATURE [App::DocumentObjectGroupPython] H_element124  label="H_element : 071"  # scripted group (container) (typed FeaturePython)
  n = 4
  ref = H_element
FEATURE [App::DocumentObjectGroupPython] C_element134  label="C_element : 079"  # scripted group (container) (typed FeaturePython)
  n = 5
  ref = C_element
FEATURE [App::DocumentObjectGroupPython] N_element054  label="N_element : 026"  # scripted group (container) (typed FeaturePython)
  n = 5
  ref = N_element
FEATURE [App::DocumentObjectGroupPython] G4_DNA_ADENINE  # scripted group (container) (typed FeaturePython)
  Dunit = g/cm3
  Dvalue = 1
  Group = -> [H_element124,C_element134,N_element054]
  conduct = 2
  density = 1
  expand = 3
  formula = G4_DNA_ADENINE
  name = G4_DNA_ADENINE
  specific = 4
FEATURE [App::DocumentObjectGroupPython] H_element125  label="H_element : 072"  # scripted group (container) (typed FeaturePython)
  n = 4
  ref = H_element
FEATURE [App::DocumentObjectGroupPython] C_element135  label="C_element : 080"  # scripted group (container) (typed FeaturePython)
  n = 5
  ref = C_element
FEATURE [App::DocumentObjectGroupPython] N_element055  label="N_element : 027"  # scripted group (container) (typed FeaturePython)
  n = 5
  ref = N_element
FEATURE [App::DocumentObjectGroupPython] O_element116  label="O_element : 069"  # scripted group (container) (typed FeaturePython)
  n = 1
  ref = O_element
FEATURE [App::DocumentObjectGroupPython] G4_DNA_GUANINE  # scripted group (container) (typed FeaturePython)
  Dunit = g/cm3
  Dvalue = 1
  Group = -> [H_element125,C_element135,N_element055,O_element116]
  conduct = 2
  density = 1
  expand = 3
  formula = G4_DNA_GUANINE
  name = G4_DNA_GUANINE
  specific = 4
FEATURE [App::DocumentObjectGroupPython] H_element126  label="H_element : 073"  # scripted group (container) (typed FeaturePython)
  n = 4
  ref = H_element
FEATURE [App::DocumentObjectGroupPython] C_element136  label="C_element : 081"  # scripted group (container) (typed FeaturePython)
  n = 4
  ref = C_element
FEATURE [App::DocumentObjectGroupPython] N_element056  label="N_element : 028"  # scripted group (container) (typed FeaturePython)
  n = 3
  ref = N_element
FEATURE [App::DocumentObjectGroupPython] O_element117  label="O_element : 070"  # scripted group (container) (typed FeaturePython)
  n = 1
  ref = O_element
FEATURE [App::DocumentObjectGroupPython] G4_DNA_CYTOSINE  # scripted group (container) (typed FeaturePython)
  Dunit = g/cm3
  Dvalue = 1
  Group = -> [H_element126,C_element136,N_element056,O_element117]
  conduct = 2
  density = 1
  expand = 3
  formula = G4_DNA_CYTOSINE
  name = G4_DNA_CYTOSINE
  specific = 4
FEATURE [App::DocumentObjectGroupPython] H_element127  label="H_element : 074"  # scripted group (container) (typed FeaturePython)
  n = 5
  ref = H_element
FEATURE [App::DocumentObjectGroupPython] C_element137  label="C_element : 082"  # scripted group (container) (typed FeaturePython)
  n = 5
  ref = C_element
FEATURE [App::DocumentObjectGroupPython] N_element057  label="N_element : 029"  # scripted group (container) (typed FeaturePython)
  n = 2
  ref = N_element
FEATURE [App::DocumentObjectGroupPython] O_element118  label="O_element : 071"  # scripted group (container) (typed FeaturePython)
  n = 2
  ref = O_element
FEATURE [App::DocumentObjectGroupPython] G4_DNA_THYMINE  # scripted group (container) (typed FeaturePython)
  Dunit = g/cm3
  Dvalue = 1
  Group = -> [H_element127,C_element137,N_element057,O_element118]
  conduct = 2
  density = 1
  expand = 3
  formula = G4_DNA_THYMINE
  name = G4_DNA_THYMINE
  specific = 4
FEATURE [App::DocumentObjectGroupPython] H_element128  label="H_element : 075"  # scripted group (container) (typed FeaturePython)
  n = 3
  ref = H_element
FEATURE [App::DocumentObjectGroupPython] C_element138  label="C_element : 083"  # scripted group (container) (typed FeaturePython)
  n = 4
  ref = C_element
FEATURE [App::DocumentObjectGroupPython] N_element058  label="N_element : 030"  # scripted group (container) (typed FeaturePython)
  n = 2
  ref = N_element
FEATURE [App::DocumentObjectGroupPython] O_element119  label="O_element : 072"  # scripted group (container) (typed FeaturePython)
  n = 2
  ref = O_element
FEATURE [App::DocumentObjectGroupPython] G4_DNA_URACIL  # scripted group (container) (typed FeaturePython)
  Dunit = g/cm3
  Dvalue = 1
  Group = -> [H_element128,C_element138,N_element058,O_element119]
  conduct = 2
  density = 1
  expand = 3
  formula = G4_DNA_URACIL
  name = G4_DNA_URACIL
  specific = 4
FEATURE [App::DocumentObjectGroupPython] H_element129  label="H_element : 076"  # scripted group (container) (typed FeaturePython)
  n = 10
  ref = H_element
FEATURE [App::DocumentObjectGroupPython] C_element139  label="C_element : 084"  # scripted group (container) (typed FeaturePython)
  n = 10
  ref = C_element
FEATURE [App::DocumentObjectGroupPython] N_element059  label="N_element : 031"  # scripted group (container) (typed FeaturePython)
  n = 5
  ref = N_element
FEATURE [App::DocumentObjectGroupPython] O_element120  label="O_element : 073"  # scripted group (container) (typed FeaturePython)
  n = 4
  ref = O_element
FEATURE [App::DocumentObjectGroupPython] G4_DNA_ADENOSINE  # scripted group (container) (typed FeaturePython)
  Dunit = g/cm3
  Dvalue = 1
  Group = -> [H_element129,C_element139,N_element059,O_element120]
  conduct = 2
  density = 1
  expand = 3
  formula = G4_DNA_ADENOSINE
  name = G4_DNA_ADENOSINE
  specific = 4
FEATURE [App::DocumentObjectGroupPython] H_element130  label="H_element : 077"  # scripted group (container) (typed FeaturePython)
  n = 10
  ref = H_element
FEATURE [App::DocumentObjectGroupPython] C_element140  label="C_element : 085"  # scripted group (container) (typed FeaturePython)
  n = 10
  ref = C_element
FEATURE [App::DocumentObjectGroupPython] N_element060  label="N_element : 032"  # scripted group (container) (typed FeaturePython)
  n = 5
  ref = N_element
FEATURE [App::DocumentObjectGroupPython] O_element121  label="O_element : 074"  # scripted group (container) (typed FeaturePython)
  n = 5
  ref = O_element
FEATURE [App::DocumentObjectGroupPython] G4_DNA_GUANOSINE  # scripted group (container) (typed FeaturePython)
  Dunit = g/cm3
  Dvalue = 1
  Group = -> [H_element130,C_element140,N_element060,O_element121]
  conduct = 2
  density = 1
  expand = 3
  formula = G4_DNA_GUANOSINE
  name = G4_DNA_GUANOSINE
  specific = 4
FEATURE [App::DocumentObjectGroupPython] H_element131  label="H_element : 078"  # scripted group (container) (typed FeaturePython)
  n = 10
  ref = H_element
FEATURE [App::DocumentObjectGroupPython] C_element141  label="C_element : 086"  # scripted group (container) (typed FeaturePython)
  n = 9
  ref = C_element
FEATURE [App::DocumentObjectGroupPython] N_element061  label="N_element : 033"  # scripted group (container) (typed FeaturePython)
  n = 3
  ref = N_element
FEATURE [App::DocumentObjectGroupPython] O_element122  label="O_element : 075"  # scripted group (container) (typed FeaturePython)
  n = 5
  ref = O_element
FEATURE [App::DocumentObjectGroupPython] G4_DNA_CYTIDINE  # scripted group (container) (typed FeaturePython)
  Dunit = g/cm3
  Dvalue = 1
  Group = -> [H_element131,C_element141,N_element061,O_element122]
  conduct = 2
  density = 1
  expand = 3
  formula = G4_DNA_CYTIDINE
  name = G4_DNA_CYTIDINE
  specific = 4
FEATURE [App::DocumentObjectGroupPython] H_element132  label="H_element : 079"  # scripted group (container) (typed FeaturePython)
  n = 9
  ref = H_element
FEATURE [App::DocumentObjectGroupPython] C_element142  label="C_element : 087"  # scripted group (container) (typed FeaturePython)
  n = 9
  ref = C_element
FEATURE [App::DocumentObjectGroupPython] N_element062  label="N_element : 034"  # scripted group (container) (typed FeaturePython)
  n = 2
  ref = N_element
FEATURE [App::DocumentObjectGroupPython] O_element123  label="O_element : 076"  # scripted group (container) (typed FeaturePython)
  n = 6
  ref = O_element
FEATURE [App::DocumentObjectGroupPython] G4_DNA_URIDINE  # scripted group (container) (typed FeaturePython)
  Dunit = g/cm3
  Dvalue = 1
  Group = -> [H_element132,C_element142,N_element062,O_element123]
  conduct = 2
  density = 1
  expand = 3
  formula = G4_DNA_URIDINE
  name = G4_DNA_URIDINE
  specific = 4
FEATURE [App::DocumentObjectGroupPython] H_element133  label="H_element : 080"  # scripted group (container) (typed FeaturePython)
  n = 11
  ref = H_element
FEATURE [App::DocumentObjectGroupPython] C_element143  label="C_element : 088"  # scripted group (container) (typed FeaturePython)
  n = 10
  ref = C_element
FEATURE [App::DocumentObjectGroupPython] N_element063  label="N_element : 035"  # scripted group (container) (typed FeaturePython)
  n = 2
  ref = N_element
FEATURE [App::DocumentObjectGroupPython] O_element124  label="O_element : 077"  # scripted group (container) (typed FeaturePython)
  n = 6
  ref = O_element
FEATURE [App::DocumentObjectGroupPython] G4_DNA_METHYLURIDINE  # scripted group (container) (typed FeaturePython)
  Dunit = g/cm3
  Dvalue = 1
  Group = -> [H_element133,C_element143,N_element063,O_element124]
  conduct = 2
  density = 1
  expand = 3
  formula = G4_DNA_METHYLURIDINE
  name = G4_DNA_METHYLURIDINE
  specific = 4
FEATURE [App::DocumentObjectGroupPython] P_element014  label="P_element : 003"  # scripted group (container) (typed FeaturePython)
  n = 1
  ref = P_element
FEATURE [App::DocumentObjectGroupPython] O_element125  label="O_element : 078"  # scripted group (container) (typed FeaturePython)
  n = 3
  ref = O_element
FEATURE [App::DocumentObjectGroupPython] G4_DNA_MONOPHOSPHATE  # scripted group (container) (typed FeaturePython)
  Dunit = g/cm3
  Dvalue = 1
  Group = -> [P_element014,O_element125]
  conduct = 2
  density = 1
  expand = 3
  formula = G4_DNA_MONOPHOSPHATE
  name = G4_DNA_MONOPHOSPHATE
  specific = 4
FEATURE [App::DocumentObjectGroupPython] H_element134  label="H_element : 081"  # scripted group (container) (typed FeaturePython)
  n = 10
  ref = H_element
FEATURE [App::DocumentObjectGroupPython] C_element144  label="C_element : 089"  # scripted group (container) (typed FeaturePython)
  n = 10
  ref = C_element
FEATURE [App::DocumentObjectGroupPython] N_element064  label="N_element : 036"  # scripted group (container) (typed FeaturePython)
  n = 5
  ref = N_element
FEATURE [App::DocumentObjectGroupPython] O_element126  label="O_element : 079"  # scripted group (container) (typed FeaturePython)
  n = 7
  ref = O_element
FEATURE [App::DocumentObjectGroupPython] P_element015  label="P_element : 004"  # scripted group (container) (typed FeaturePython)
  n = 1
  ref = P_element
FEATURE [App::DocumentObjectGroupPython] G4_DNA_A  # scripted group (container) (typed FeaturePython)
  Dunit = g/cm3
  Dvalue = 1
  Group = -> [H_element134,C_element144,N_element064,O_element126,P_element015]
  conduct = 2
  density = 1
  expand = 3
  formula = G4_DNA_A
  name = G4_DNA_A
  specific = 4
FEATURE [App::DocumentObjectGroupPython] H_element135  label="H_element : 082"  # scripted group (container) (typed FeaturePython)
  n = 10
  ref = H_element
FEATURE [App::DocumentObjectGroupPython] C_element145  label="C_element : 090"  # scripted group (container) (typed FeaturePython)
  n = 10
  ref = C_element
FEATURE [App::DocumentObjectGroupPython] N_element065  label="N_element : 037"  # scripted group (container) (typed FeaturePython)
  n = 5
  ref = N_element
FEATURE [App::DocumentObjectGroupPython] O_element127  label="O_element : 8"  # scripted group (container) (typed FeaturePython)
  n = 8
  ref = O_element
FEATURE [App::DocumentObjectGroupPython] P_element016  label="P_element : 005"  # scripted group (container) (typed FeaturePython)
  n = 1
  ref = P_element
FEATURE [App::DocumentObjectGroupPython] G4_DNA_G  # scripted group (container) (typed FeaturePython)
  Dunit = g/cm3
  Dvalue = 1
  Group = -> [H_element135,C_element145,N_element065,O_element127,P_element016]
  conduct = 2
  density = 1
  expand = 3
  formula = G4_DNA_G
  name = G4_DNA_G
  specific = 4
FEATURE [App::DocumentObjectGroupPython] H_element136  label="H_element : 083"  # scripted group (container) (typed FeaturePython)
  n = 10
  ref = H_element
FEATURE [App::DocumentObjectGroupPython] C_element146  label="C_element : 091"  # scripted group (container) (typed FeaturePython)
  n = 9
  ref = C_element
FEATURE [App::DocumentObjectGroupPython] N_element066  label="N_element : 038"  # scripted group (container) (typed FeaturePython)
  n = 3
  ref = N_element
FEATURE [App::DocumentObjectGroupPython] O_element128  label="O_element : 080"  # scripted group (container) (typed FeaturePython)
  n = 8
  ref = O_element
FEATURE [App::DocumentObjectGroupPython] P_element017  label="P_element : 006"  # scripted group (container) (typed FeaturePython)
  n = 1
  ref = P_element
FEATURE [App::DocumentObjectGroupPython] G4_DNA_C  # scripted group (container) (typed FeaturePython)
  Dunit = g/cm3
  Dvalue = 1
  Group = -> [H_element136,C_element146,N_element066,O_element128,P_element017]
  conduct = 2
  density = 1
  expand = 3
  formula = G4_DNA_C
  name = G4_DNA_C
  specific = 4
FEATURE [App::DocumentObjectGroupPython] H_element137  label="H_element : 084"  # scripted group (container) (typed FeaturePython)
  n = 9
  ref = H_element
FEATURE [App::DocumentObjectGroupPython] C_element147  label="C_element : 092"  # scripted group (container) (typed FeaturePython)
  n = 9
  ref = C_element
FEATURE [App::DocumentObjectGroupPython] N_element067  label="N_element : 039"  # scripted group (container) (typed FeaturePython)
  n = 2
  ref = N_element
FEATURE [App::DocumentObjectGroupPython] O_element129  label="O_element : 9"  # scripted group (container) (typed FeaturePython)
  n = 9
  ref = O_element
FEATURE [App::DocumentObjectGroupPython] P_element018  label="P_element : 007"  # scripted group (container) (typed FeaturePython)
  n = 1
  ref = P_element
FEATURE [App::DocumentObjectGroupPython] G4_DNA_U  # scripted group (container) (typed FeaturePython)
  Dunit = g/cm3
  Dvalue = 1
  Group = -> [H_element137,C_element147,N_element067,O_element129,P_element018]
  conduct = 2
  density = 1
  expand = 3
  formula = G4_DNA_U
  name = G4_DNA_U
  specific = 4
FEATURE [App::DocumentObjectGroupPython] H_element138  label="H_element : 085"  # scripted group (container) (typed FeaturePython)
  n = 11
  ref = H_element
FEATURE [App::DocumentObjectGroupPython] C_element148  label="C_element : 093"  # scripted group (container) (typed FeaturePython)
  n = 10
  ref = C_element
FEATURE [App::DocumentObjectGroupPython] N_element068  label="N_element : 040"  # scripted group (container) (typed FeaturePython)
  n = 2
  ref = N_element
FEATURE [App::DocumentObjectGroupPython] O_element130  label="O_element : 081"  # scripted group (container) (typed FeaturePython)
  n = 9
  ref = O_element
FEATURE [App::DocumentObjectGroupPython] P_element019  label="P_element : 008"  # scripted group (container) (typed FeaturePython)
  n = 1
  ref = P_element
FEATURE [App::DocumentObjectGroupPython] G4_DNA_MU  # scripted group (container) (typed FeaturePython)
  Dunit = g/cm3
  Dvalue = 1
  Group = -> [H_element138,C_element148,N_element068,O_element130,P_element019]
  conduct = 2
  density = 1
  expand = 3
  formula = G4_DNA_MU
  name = G4_DNA_MU
  specific = 4
FEATURE [App::DocumentObjectGroupPython] BioChemical  # scripted group (container) (typed FeaturePython)
  Group = -> [G4_CYTOSINE,G4_THYMINE,G4_URACIL,G4_DNA_ADENINE,G4_DNA_GUANINE,G4_DNA_CYTOSINE,G4_DNA_THYMINE,G4_DNA_URACIL,G4_DNA_ADENOSINE,G4_DNA_GUANOSINE,G4_DNA_CYTIDINE,G4_DNA_URIDINE,G4_DNA_METHYLURIDINE,G4_DNA_MONOPHOSPHATE,G4_DNA_A,G4_DNA_G,G4_DNA_C,G4_DNA_U,G4_DNA_MU]
FEATURE [App::DocumentObjectGroupPython] G4Materials  # scripted group (container) (typed FeaturePython)
  Group = -> [NIST,Element,HEP,Space,BioChemical]
  version = 1
FEATURE [App::DocumentObjectGroupPython] Geant4  # scripted group (container) (typed FeaturePython)
  Group = -> [G4Isotopes,G4Elements,G4Materials]
FEATURE [App::DocumentObjectGroupPython] Materials  # scripted group (container) (typed FeaturePython)
  Group = -> [Geant4]
FEATURE [Part::FeaturePython] GDMLBox_WorldBox  # WARN: FeaturePython — macro-defined, semantics opaque (R4)
  lunit = 2
  material = 5
  x = 273
  y = 273
  z = 130
FEATURE [Part::FeaturePython] GDMLBox_Box  # WARN: FeaturePython — macro-defined, semantics opaque (R4)
  Placement = pos=(20,0,0) rot=(0,0,1;0rad)
  lunit = 2
  material = 0
  x = 10
  y = 10
  z = 10
FEATURE [Part::FeaturePython] GDMLTube  # WARN: FeaturePython — macro-defined, semantics opaque (R4)
  Placement = pos=(17,-4,0) rot=(0,0,1;0rad)
  aunit = 1
  deltaphi = 90
  lunit = 2
  material = 0
  rmax = 7
  rmin = 5
  startphi = 0
  z = 7
FEATURE [App::Part] LV_Tube
  Group = -> [GDMLTube]
  Origin = -> Origin003
  SkinSurface = 0
FEATURE [App::Part] LV_Box
  Group = -> [GDMLBox_Box,LV_Tube]
  Origin = -> Origin002
FEATURE [Part::FeaturePython] Array  # Draft array (typed FeaturePython)
  AlwaysSyncPlacement = false
  Angle = 180
  ArrayType = 1
  Axis = (0,0,1)
  Base = -> LV_Box
  Center = (0,0,0)
  Count = 5
  ExpandArray = false
  Fuse = false
  IntervalAxis = (0,0,0)
  IntervalX = (100,0,0)
  IntervalY = (0,100,0)
  IntervalZ = (0,0,100)
  NumberCircles = 3
  NumberPolar = 5
  NumberX = 2
  NumberY = 2
  NumberZ = 1
  PlacementList = 5 placements: [(0,0,0),(0,0,0),(0,0,0),(0,0,0),(0,0,0)]
  RadialDistance = 50
  ScaleList = (5) [(1,1,1),(1,1,1),(1,1,1),(1,1,1),(1,1,1)]
  Symmetry = 1
  TangentialDistance = 25
FEATURE [Part::FeaturePython] Array001  # Draft array (typed FeaturePython)
  AlwaysSyncPlacement = false
  Angle = 360
  ArrayType = 0
  Axis = (0,0,1)
  Base = -> Array
  Center = (0,0,0)
  Count = 4
  ExpandArray = false
  Fuse = false
  IntervalAxis = (0,0,0)
  IntervalX = (100,0,0)
  IntervalY = (0,100,0)
  IntervalZ = (0,0,100)
  NumberCircles = 3
  NumberPolar = 5
  NumberX = 2
  NumberY = 2
  NumberZ = 1
  PlacementList = 4 placements: [(0,0,0),(0,100,0),(100,0,0),(100,100,0)]
  RadialDistance = 50
  ScaleList = (4) [(1,1,1),(1,1,1),(1,1,1),(1,1,1)]
  Symmetry = 1
  TangentialDistance = 25
FEATURE [App::Part] Part  label="experiment"
  Group = -> [LV_Box,Array,Array001]
  Origin = -> Origin001
FEATURE [App::Part] worldVOL
  Group = -> [GDMLBox_WorldBox,Part]
  Origin = -> Origin
